FCSTD DOCUMENT  (FreeCAD 0.21R33771 (Git))
Label: key-v4_r
License: All rights reserved
LicenseURL: https://en.wikipedia.org/wiki/All_rights_reserved
objects: Sketcher::SketchObject×6, Part::Part2DObjectPython×3, Part::FeaturePython×2, Spreadsheet::Sheet×1
note: 10 computed .brp shape members not serialized (recipe doc carries the construction recipe); baked Part::Feature solids carry a one-line shape summary decoded from their .brp

FEATURE [Spreadsheet::Sheet] Spreadsheet  label="constants"
  cells = A1(slot_height)=0.6; B1='slot height; A2(base_normal)=1.5; B2='base normal; A3(base_thin)=0.3; B3='base thin ; A4(fillet_small)=0.15; B4='fillet rounding
FEATURE [Part::Part2DObjectPython] Wire  # Draft 2D object (typed FeaturePython)
  Area = 0
  ChamferSize = 0
  Closed = false
  End = (95,2.6,0)
  FilletRadius = 0
  Length = 95.9778
  MakeFace = true
  Points = (6) [(0,0,0),(19,0,0),(38,4.8,0),(57,7,0),(76,4.8,0),(95,2.6,0)]
  Start = (0,0,0)
  Subdivisions = 0
FEATURE [Part::Part2DObjectPython] Wire001  label="main matrix wire"  # Draft 2D object (typed FeaturePython)
  Area = 0
  ChamferSize = 0
  Closed = false
  End = (95,2.6,0)
  FilletRadius = 0
  Length = 323.978
  MakeFace = false
  Points = (18) [(0,0,0),(0,-19,0),(0,-38,0),(19,-38,0),(19,-19,0),(19,0,0),(38,4.8,0),(38,-14.2,0),(38,-33.2,0),(57,-31,0),(57,-12,0),(57,7,0),(76,4.8,0),+5 more]
  Start = (0,0,0)
  Subdivisions = 0
FEATURE [Part::Part2DObjectPython] Wire002  label="horizonal matrix"  # Draft 2D object (typed FeaturePython)
  Area = 0
  ChamferSize = 0
  Closed = false
  End = (95,2.6,0)
  FilletRadius = 0
  Length = 368.271
  MakeFace = true
  Points = (20) [(0,0,0),(0,-19,0),(0,-38,0),(19,-38,0),(19,-19,0),(19,0,0),(38,4.8,0),(38,-14.2,0),(38,-33.2,0),(47,-52.4,0),(66,-52.4,0),(57,-31,0),(57,-12,0),+7 more]
  Start = (0,0,0)
  Subdivisions = 0
FEATURE [Sketcher::SketchObject] Sketch001  label="smd cutout prototype"
  FullyConstrained = true
  sketch-geometry (67):
    g0: LineSegment StartX=-9.5 StartY=-9.5 StartZ=0 EndX=9.5 EndY=-9.5 EndZ=0
    g1: LineSegment StartX=9.5 StartY=-9.5 StartZ=0 EndX=9.5 EndY=9.5 EndZ=0
    g2: LineSegment StartX=9.5 StartY=9.5 StartZ=0 EndX=-9.5 EndY=9.5 EndZ=0
    g3: LineSegment StartX=-9.5 StartY=9.5 StartZ=0 EndX=-9.5 EndY=-9.5 EndZ=0
    g4: Circle CenterX=-3.81 CenterY=2.54 CenterZ=0 NormalX=0 NormalY=0 NormalZ=1 AngleXU=0 Radius=1.5
    g5: Circle CenterX=2.54 CenterY=5.08 CenterZ=0 NormalX=0 NormalY=0 NormalZ=1 AngleXU=0 Radius=1.5
    g6: Circle CenterX=0 CenterY=0 CenterZ=0 NormalX=0 NormalY=0 NormalZ=1 AngleXU=0 Radius=2
    g7: Circle CenterX=5 CenterY=0 CenterZ=0 NormalX=0 NormalY=0 NormalZ=1 AngleXU=0 Radius=1
    g8: Circle CenterX=-5 CenterY=0 CenterZ=0 NormalX=0 NormalY=0 NormalZ=1 AngleXU=0 Radius=1
    g9: GeomPoint X=-8.5 Y=1 Z=0
    g10: GeomPoint X=-8.5 Y=4 Z=0
    g11: GeomPoint X=-6 Y=4 Z=0
    g12: GeomPoint X=-2.5 Y=1 Z=0
    g13: GeomPoint X=-0.4 Y=2.9 Z=0
    g14: GeomPoint X=4.5 Y=2.9 Z=0
    g15: GeomPoint X=4.5 Y=3.6 Z=0
    g16: GeomPoint X=7.1 Y=6.7 Z=0
    g17: GeomPoint X=-4 Y=6.7 Z=0
    g18: LineSegment StartX=-8.5 StartY=1 StartZ=0 EndX=-2.5 EndY=1 EndZ=0
    g19: LineSegment StartX=-8.5 StartY=1 StartZ=0 EndX=-8.5 EndY=4 EndZ=0
    g20: LineSegment StartX=-8.5 StartY=4 StartZ=0 EndX=-6 EndY=4 EndZ=0
    g21: LineSegment StartX=-6 StartY=4 StartZ=0 EndX=-6 EndY=4.7 EndZ=0
    g22: LineSegment StartX=-4 StartY=6.7 StartZ=0 EndX=7.1 EndY=6.7 EndZ=0
    g23: LineSegment StartX=7.1 StartY=6.7 StartZ=0 EndX=7.1 EndY=3.6 EndZ=0
    g24: LineSegment StartX=7.1 StartY=3.6 StartZ=0 EndX=4.5 EndY=3.6 EndZ=0
    g25: LineSegment StartX=4.5 StartY=2.9 StartZ=0 EndX=4.5 EndY=3.6 EndZ=0
    g26: LineSegment StartX=4.5 StartY=2.9 StartZ=0 EndX=-0.4 EndY=2.9 EndZ=0
    g27: ArcOfCircle CenterX=-0.4 CenterY=0.789474 CenterZ=0 NormalX=0 NormalY=0 NormalZ=1 AngleXU=0 Radius=2.11053 StartAngle=1.5708 EndAngle=3.04168
    g28: LineSegment StartX=6.85 StartY=2.35 StartZ=0 EndX=6.85 EndY=-2.35 EndZ=0
    g29: LineSegment StartX=6.85 StartY=-2.35 StartZ=0 EndX=9.15 EndY=-2.35 EndZ=0
    g30: LineSegment StartX=9.15 StartY=-2.35 StartZ=0 EndX=9.15 EndY=2.35 EndZ=0
    g31: ArcOfCircle CenterX=-4 CenterY=4.7 CenterZ=0 NormalX=0 NormalY=0 NormalZ=1 AngleXU=0 Radius=2 StartAngle=1.5708 EndAngle=3.14159
    g32: LineSegment StartX=6.85 StartY=2.35 StartZ=0 EndX=9.15 EndY=2.35 EndZ=0
    g33: LineSegment StartX=-8.8 StartY=0.8 StartZ=0 EndX=-8.8 EndY=4.2 EndZ=0
    g34: LineSegment StartX=-8.3 StartY=4.7 StartZ=0 EndX=-7.1607 EndY=4.7 EndZ=0
    g35: LineSegment StartX=-4 StartY=7.4 StartZ=0 EndX=7.3 EndY=7.4 EndZ=0
    g36: LineSegment StartX=7.8 StartY=6.9 StartZ=0 EndX=7.8 EndY=3.55 EndZ=0
    g37: LineSegment StartX=9.5 StartY=2.55 StartZ=0 EndX=9.5 EndY=-2.55 EndZ=0
    g38: LineSegment StartX=9 StartY=-3.05 StartZ=0 EndX=6.65 EndY=-3.05 EndZ=0
    g39: LineSegment StartX=-8.3 StartY=0.3 StartZ=0 EndX=-7.19089 EndY=0.3 EndZ=0
    g40: ArcOfCircle CenterX=-5 CenterY=0 CenterZ=0 NormalX=0 NormalY=0 NormalZ=1 AngleXU=0 Radius=1.7 StartAngle=3.23263 EndAngle=4.71239
    g41: ArcOfCircle CenterX=0 CenterY=0 CenterZ=0 NormalX=0 NormalY=0 NormalZ=1 AngleXU=0 Radius=2.7 StartAngle=3.89963 EndAngle=5.52514
    g42: LineSegment StartX=-5 StartY=-1.7 StartZ=0 EndX=-2.32379 EndY=-1.7 EndZ=0
    g43: LineSegment StartX=6.15 StartY=-2.55 StartZ=0 EndX=6.15 EndY=-2.2 EndZ=0
    g44: LineSegment StartX=2.32379 StartY=-1.7 StartZ=0 EndX=5.65 EndY=-1.7 EndZ=0
    g45: ArcOfCircle CenterX=-4 CenterY=4.7 CenterZ=0 NormalX=0 NormalY=0 NormalZ=1 AngleXU=0 Radius=2.7 StartAngle=1.5708 EndAngle=2.9847
    g46: ArcOfCircle CenterX=-2.32379 CenterY=-2.2 CenterZ=0 NormalX=0 NormalY=0 NormalZ=1 AngleXU=0 Radius=0.5 StartAngle=0.758041 EndAngle=1.5708
    g47: ArcOfCircle CenterX=2.32379 CenterY=-2.2 CenterZ=0 NormalX=0 NormalY=0 NormalZ=1 AngleXU=0 Radius=0.5 StartAngle=1.5708 EndAngle=2.38355
    g48: ArcOfCircle CenterX=5.65 CenterY=-2.2 CenterZ=0 NormalX=0 NormalY=0 NormalZ=1 AngleXU=0 Radius=0.5 StartAngle=0 EndAngle=1.5708
    g49: GeomPoint X=6.15 Y=-1.7 Z=0
    g50: ArcOfCircle CenterX=6.65 CenterY=-2.55 CenterZ=0 NormalX=0 NormalY=0 NormalZ=1 AngleXU=0 Radius=0.5 StartAngle=3.14159 EndAngle=4.71239
    g51: GeomPoint X=6.15 Y=-3.05 Z=0
    g52: ArcOfCircle CenterX=9 CenterY=-2.55 CenterZ=0 NormalX=0 NormalY=0 NormalZ=1 AngleXU=0 Radius=0.5 StartAngle=4.71239 EndAngle=6.28319
    g53: GeomPoint X=9.5 Y=-3.05 Z=0
    g54: LineSegment StartX=8.3 StartY=3.05 StartZ=0 EndX=9 EndY=3.05 EndZ=0
    g55: ArcOfCircle CenterX=9 CenterY=2.55 CenterZ=0 NormalX=0 NormalY=0 NormalZ=1 AngleXU=0 Radius=0.5 StartAngle=3e-16 EndAngle=1.5708
    g56: GeomPoint X=9.5 Y=3.05 Z=0
    g57: ArcOfCircle CenterX=8.3 CenterY=3.55 CenterZ=0 NormalX=0 NormalY=0 NormalZ=1 AngleXU=0 Radius=0.5 StartAngle=3.14159 EndAngle=4.71239
    g58: GeomPoint X=7.8 Y=3.05 Z=0
    g59: ArcOfCircle CenterX=7.3 CenterY=6.9 CenterZ=0 NormalX=0 NormalY=0 NormalZ=1 AngleXU=0 Radius=0.5 StartAngle=-9e-16 EndAngle=1.5708
    g60: GeomPoint X=7.8 Y=7.4 Z=0
    g61: ArcOfCircle CenterX=-7.1607 CenterY=5.2 CenterZ=0 NormalX=0 NormalY=0 NormalZ=1 AngleXU=0 Radius=0.5 StartAngle=4.71239 EndAngle=6.12629
    g62: ArcOfCircle CenterX=-8.3 CenterY=4.2 CenterZ=0 NormalX=0 NormalY=0 NormalZ=1 AngleXU=0 Radius=0.5 StartAngle=1.5708 EndAngle=3.14159
    g63: GeomPoint X=-8.8 Y=4.7 Z=0
    g64: ArcOfCircle CenterX=-8.3 CenterY=0.8 CenterZ=0 NormalX=0 NormalY=0 NormalZ=1 AngleXU=0 Radius=0.5 StartAngle=3.14159 EndAngle=4.71239
    g65: GeomPoint X=-8.8 Y=0.3 Z=0
    g66: ArcOfCircle CenterX=-7.19089 CenterY=-0.2 CenterZ=0 NormalX=0 NormalY=0 NormalZ=1 AngleXU=0 Radius=0.5 StartAngle=0.0910348 EndAngle=1.5708
  constraints (157):
    c: Coincident(g2,g3)
    c: Horizontal(g0)
    c: Horizontal(g2)
    c: Vertical(g1)
    c: PointOnObject(g7,g-1)
    c: Equal(g4,g5)
    c: Symmetric(g7,g8,g-2)
    c: Equal(g8,g7)
    c: DistanceX(g-1,g5) = 2.54
    c: Distance(g5,g-1) = 5.08
    c: DistanceX(g2,g2) = 19
    c: Equal(g2,g3)
    c: Distance(g4,g-2) = 3.81
    c: Distance(g4,g-1) = 2.54
    c: Distance(g8,g-2) = 5
    c: Distance(g9,g-1) = 1
    c: Coincident(g18,g9)
    c: Coincident(g18,g12)
    c: Horizontal(g18)
    c: Distance(g9,g-2) = 8.5
    c: Coincident(g19,g9)
    c: Coincident(g19,g10)
    c: Vertical(g19)
    c: Distance(g10,g-1) = 4
    c: Coincident(g20,g10)
    c: Coincident(g20,g11)
    c: Horizontal(g20)
    c: Distance(g11,g-2) = 6
    c: Distance(g17,g-2) = 4
    c: DistanceY(g-1,g17) = 6.7
    c: Coincident(g21,g11)
    c: Vertical(g21)
    c: Coincident(g22,g17)
    c: Coincident(g22,g16)
    c: Horizontal(g22)
    c: DistanceX(g-1,g16) = 7.1
    c: Coincident(g23,g16)
    c: Vertical(g23)
    c: Distance(g23,g-1) = 3.6
    c: Coincident(g24,g23)
    c: Coincident(g24,g15)
    c: Coincident(g25,g14)
    c: Coincident(g25,g15)
    c: Coincident(g26,g14)
    c: Coincident(g26,g13)
    c: Horizontal(g24)
    c: Horizontal(g26)
    c: Vertical(g25)
    c: Distance(g-2,g25) = 4.5
    c: Distance(g14,g-1) = 2.9
    c: Distance(g13,g-2) = 0.4
    c: Distance(g12,g-2) = 2.5
    c: Coincident(g27,g13)
    c: Coincident(g27,g12)
    c: Diameter(g5) = 3
    c: Diameter(g8) = 2
    c: Diameter(g6) = 4
    c: Vertical(g30)
    c: Horizontal(g29)
    c: Distance(g28,g-2) = 6.85
    c: Distance(g28,g-1) = 2.35
    c: Symmetric(g28,g28,g-1)
    c: Vertical(g3)
    c: Coincident(g31,g17)
    c: Tangent(g31,g21) = 1.5708
    c: Coincident(g32,g28)
    c: Coincident(g32,g30)
    c: Horizontal(g32)
    c: Coincident(g6,g-1)
    c: Symmetric(g0,g1,g6)
    c: Coincident(g3,g0)
    c: Coincident(g2,g1)
    c: Coincident(g1,g0)
    c: DistanceX(g29,g29) = 2.3
    c: Coincident(g29,g30)
    c: Coincident(g29,g28)
    c: Tangent(g27,g26)
    c: Tangent(g31,g22)
    c: Vertical(g33)
    c: Horizontal(g34)
    c: Horizontal(g35)
    c: Vertical(g36)
    c: PointOnObject(g56,g1)
    c: PointOnObject(g53,g1)
    c: Horizontal(g38)
    c: Horizontal(g39)
    c: Distance(g20,g34) = 0.7
    c: Distance(g65,g19) = 0.3
    c: Distance(g18,g39) = 0.7
    c: Coincident(g40,g8)
    c: Coincident(g41,g6)
    c: Horizontal(g42)
    c: Vertical(g43)
    c: Tangent(g44,g42)
    c: Distance(g28,g43) = 0.7
    c: Distance(g53,g29) = 0.7
    c: Tangent(g42,g40) = -1.5708
    c: Distance(g23,g36) = 0.7
    c: Distance(g35,g22) = 0.7
    c: Coincident(g45,g31)
    c: Tangent(g45,g35) = 1.5708
    c: Tangent(g42,g46) = 1.5708
    c: Tangent(g41,g46) = 1.5708
    c: Tangent(g41,g47) = 1.5708
    c: Tangent(g44,g47) = 1.5708
    c: PointOnObject(g49,g44)
    c: PointOnObject(g49,g43)
    c: Tangent(g44,g48) = 1.5708
    c: Tangent(g43,g48) = -1.5708
    c: PointOnObject(g51,g43)
    c: PointOnObject(g51,g38)
    c: Tangent(g43,g50) = 1.5708
    c: Tangent(g38,g50) = 1.5708
    c: PointOnObject(g53,g38)
    c: PointOnObject(g53,g37)
    c: Tangent(g38,g52) = 1.5708
    c: Tangent(g37,g52) = 1.5708
    c: Horizontal(g54)
    c: Distance(g32,g54) = 0.7
    c: PointOnObject(g56,g37)
    c: PointOnObject(g56,g54)
    c: Tangent(g37,g55) = 1.5708
    c: Tangent(g54,g55) = 1.5708
    c: PointOnObject(g58,g54)
    c: PointOnObject(g58,g36)
    c: Tangent(g54,g57) = -1.5708
    c: Tangent(g36,g57) = -1.5708
    c: PointOnObject(g60,g35)
    c: PointOnObject(g60,g36)
    c: Tangent(g35,g59) = 1.5708
    c: Tangent(g36,g59) = 1.5708
    c: Tangent(g34,g61) = -1.5708
    c: Tangent(g45,g61) = 1.5708
    c: PointOnObject(g63,g34)
    c: PointOnObject(g63,g33)
    c: Tangent(g34,g62) = 1.5708
    c: Tangent(g33,g62) = 1.5708
    c: PointOnObject(g65,g39)
    c: PointOnObject(g65,g33)
    c: Tangent(g39,g64) = -1.5708
    c: Tangent(g33,g64) = 1.5708
    c: Tangent(g40,g66) = 1.5708
    c: Tangent(g39,g66) = 1.5708
    c: Radius(g46) = 0.5
    c: Equal(g66,g64)
    c: Equal(g64,g46)
    c: Equal(g46,g47)
    c: Equal(g47,g48)
    c: Equal(g48,g50)
    c: Equal(g50,g57)
    c: Equal(g57,g59)
    c: Equal(g59,g61)
    c: Equal(g61,g62)
    c: Equal(g57,g55)
    c: Equal(g52,g50)
    c: Distance(g40,g8) = 0.7
    c: Distance(g41,g6) = 0.7
FEATURE [Sketcher::SketchObject] Sketch003  label="smd cutout"
  FullyConstrained = false
  sketch-geometry (61):
    g0: GeomPoint X=-8.5 Y=1 Z=0
    g1: GeomPoint X=-8.5 Y=4 Z=0
    g2: GeomPoint X=-6 Y=4 Z=0
    g3: GeomPoint X=-2.5 Y=1 Z=0
    g4: GeomPoint X=-0.4 Y=2.9 Z=0
    g5: GeomPoint X=4.5 Y=2.9 Z=0
    g6: GeomPoint X=4.5 Y=3.6 Z=0
    g7: GeomPoint X=7.1 Y=6.7 Z=0
    g8: GeomPoint X=-4 Y=6.7 Z=0
    g9: LineSegment StartX=-8.8 StartY=0.8 StartZ=0 EndX=-8.8 EndY=4.2 EndZ=0
    g10: LineSegment StartX=-8.3 StartY=4.7 StartZ=0 EndX=-7.1607 EndY=4.7 EndZ=0
    g11: LineSegment StartX=-4 StartY=7.4 StartZ=0 EndX=7.3 EndY=7.4 EndZ=0
    g12: LineSegment StartX=7.8 StartY=6.9 StartZ=0 EndX=7.8 EndY=3.55 EndZ=0
    g13: LineSegment StartX=9.5 StartY=2.55 StartZ=0 EndX=9.5 EndY=-2.55 EndZ=0
    g14: LineSegment StartX=9 StartY=-3.05 StartZ=0 EndX=6.65 EndY=-3.05 EndZ=0
    g15: LineSegment StartX=-8.3 StartY=0.3 StartZ=0 EndX=-7.19089 EndY=0.3 EndZ=0
    g16: ArcOfCircle CenterX=-5 CenterY=0 CenterZ=0 NormalX=0 NormalY=0 NormalZ=1 AngleXU=0 Radius=1.7 StartAngle=3.23263 EndAngle=4.71239
    g17: ArcOfCircle CenterX=0 CenterY=0 CenterZ=0 NormalX=0 NormalY=0 NormalZ=1 AngleXU=0 Radius=2.7 StartAngle=3.89963 EndAngle=5.52514
    g18: LineSegment StartX=-5 StartY=-1.7 StartZ=0 EndX=-2.32379 EndY=-1.7 EndZ=0
    g19: LineSegment StartX=6.15 StartY=-2.55 StartZ=0 EndX=6.15 EndY=-2.2 EndZ=0
    g20: LineSegment StartX=2.32379 StartY=-1.7 StartZ=0 EndX=5.65 EndY=-1.7 EndZ=0
    g21: ArcOfCircle CenterX=-4 CenterY=4.7 CenterZ=0 NormalX=0 NormalY=0 NormalZ=1 AngleXU=0 Radius=2.7 StartAngle=1.5708 EndAngle=2.9847
    g22: ArcOfCircle CenterX=-2.32379 CenterY=-2.2 CenterZ=0 NormalX=0 NormalY=0 NormalZ=1 AngleXU=0 Radius=0.5 StartAngle=0.758041 EndAngle=1.5708
    g23: ArcOfCircle CenterX=2.32379 CenterY=-2.2 CenterZ=0 NormalX=0 NormalY=0 NormalZ=1 AngleXU=0 Radius=0.5 StartAngle=1.5708 EndAngle=2.38355
    g24: ArcOfCircle CenterX=5.65 CenterY=-2.2 CenterZ=0 NormalX=0 NormalY=0 NormalZ=1 AngleXU=0 Radius=0.5 StartAngle=0 EndAngle=1.5708
    g25: GeomPoint X=6.15 Y=-1.7 Z=0
    g26: ArcOfCircle CenterX=6.65 CenterY=-2.55 CenterZ=0 NormalX=0 NormalY=0 NormalZ=1 AngleXU=0 Radius=0.5 StartAngle=3.14159 EndAngle=4.71239
    g27: GeomPoint X=6.15 Y=-3.05 Z=0
    g28: ArcOfCircle CenterX=9 CenterY=-2.55 CenterZ=0 NormalX=0 NormalY=0 NormalZ=1 AngleXU=0 Radius=0.5 StartAngle=4.71239 EndAngle=6.28319
    g29: GeomPoint X=9.5 Y=-3.05 Z=0
    g30: LineSegment StartX=8.3 StartY=3.05 StartZ=0 EndX=9 EndY=3.05 EndZ=0
    g31: ArcOfCircle CenterX=9 CenterY=2.55 CenterZ=0 NormalX=0 NormalY=0 NormalZ=1 AngleXU=0 Radius=0.5 StartAngle=3e-16 EndAngle=1.5708
    g32: GeomPoint X=9.5 Y=3.05 Z=0
    g33: ArcOfCircle CenterX=8.3 CenterY=3.55 CenterZ=0 NormalX=0 NormalY=0 NormalZ=1 AngleXU=0 Radius=0.5 StartAngle=3.14159 EndAngle=4.71239
    g34: GeomPoint X=7.8 Y=3.05 Z=0
    g35: ArcOfCircle CenterX=7.3 CenterY=6.9 CenterZ=0 NormalX=0 NormalY=0 NormalZ=1 AngleXU=0 Radius=0.5 StartAngle=-9e-16 EndAngle=1.5708
    g36: GeomPoint X=7.8 Y=7.4 Z=0
    g37: ArcOfCircle CenterX=-7.1607 CenterY=5.2 CenterZ=0 NormalX=0 NormalY=0 NormalZ=1 AngleXU=0 Radius=0.5 StartAngle=4.71239 EndAngle=6.12629
    g38: ArcOfCircle CenterX=-8.3 CenterY=4.2 CenterZ=0 NormalX=0 NormalY=0 NormalZ=1 AngleXU=0 Radius=0.5 StartAngle=1.5708 EndAngle=3.14159
    g39: GeomPoint X=-8.8 Y=4.7 Z=0
    g40: ArcOfCircle CenterX=-8.3 CenterY=0.8 CenterZ=0 NormalX=0 NormalY=0 NormalZ=1 AngleXU=0 Radius=0.5 StartAngle=3.14159 EndAngle=4.71239
    g41: GeomPoint X=-8.8 Y=0.3 Z=0
    g42: ArcOfCircle CenterX=-7.19089 CenterY=-0.2 CenterZ=0 NormalX=0 NormalY=0 NormalZ=1 AngleXU=0 Radius=0.5 StartAngle=0.0910348 EndAngle=1.5708
    g43: ArcOfCircle CenterX=-5 CenterY=0 CenterZ=0 NormalX=0 NormalY=0 NormalZ=1 AngleXU=0 Radius=3.2 StartAngle=3.52599 EndAngle=4.71239
    g44: LineSegment StartX=-5 StartY=-3.2 StartZ=0 EndX=-2.72029 EndY=-3.2 EndZ=0
    g45: ArcOfCircle CenterX=0 CenterY=0 CenterZ=0 NormalX=0 NormalY=0 NormalZ=1 AngleXU=0 Radius=4.2 StartAngle=4.00784 EndAngle=5.41694
    g46: LineSegment StartX=2.72029 StartY=-3.2 StartZ=0 EndX=4.75857 EndY=-3.2 EndZ=0
    g47: ArcOfCircle CenterX=6.65 CenterY=-2.55 CenterZ=0 NormalX=0 NormalY=0 NormalZ=1 AngleXU=0 Radius=2 StartAngle=3.4726 EndAngle=4.71239
    g48: LineSegment StartX=9 StartY=-4.55 StartZ=0 EndX=6.65 EndY=-4.55 EndZ=0
    g49: ArcOfCircle CenterX=9 CenterY=-2.55 CenterZ=0 NormalX=0 NormalY=0 NormalZ=1 AngleXU=0 Radius=2 StartAngle=4.71239 EndAngle=6.28319
    g50: LineSegment StartX=11 StartY=2.55 StartZ=0 EndX=11 EndY=-2.55 EndZ=0
    g51: ArcOfCircle CenterX=9 CenterY=2.55 CenterZ=0 NormalX=0 NormalY=0 NormalZ=1 AngleXU=0 Radius=2 StartAngle=0 EndAngle=1.42023
    g52: LineSegment StartX=9.3 StartY=6.9 StartZ=0 EndX=9.3 EndY=4.52737 EndZ=0
    g53: ArcOfCircle CenterX=7.3 CenterY=6.9 CenterZ=0 NormalX=0 NormalY=0 NormalZ=1 AngleXU=0 Radius=2 StartAngle=4e-16 EndAngle=1.5708
    g54: LineSegment StartX=-4 StartY=8.9 StartZ=0 EndX=7.3 EndY=8.9 EndZ=0
    g55: ArcOfCircle CenterX=-4 CenterY=4.7 CenterZ=0 NormalX=0 NormalY=0 NormalZ=1 AngleXU=0 Radius=4.2 StartAngle=1.5708 EndAngle=2.77639
    g56: LineSegment StartX=-8.3 StartY=6.2 StartZ=0 EndX=-7.92301 EndY=6.2 EndZ=0
    g57: ArcOfCircle CenterX=-8.3 CenterY=4.2 CenterZ=0 NormalX=0 NormalY=0 NormalZ=1 AngleXU=0 Radius=2 StartAngle=1.5708 EndAngle=3.14159
    g58: LineSegment StartX=-10.3 StartY=0.8 StartZ=0 EndX=-10.3 EndY=4.2 EndZ=0
    g59: ArcOfCircle CenterX=-8.3 CenterY=0.8 CenterZ=0 NormalX=0 NormalY=0 NormalZ=1 AngleXU=0 Radius=2 StartAngle=3.14159 EndAngle=4.71239
    g60: LineSegment StartX=-8.3 StartY=-1.2 StartZ=0 EndX=-7.96648 EndY=-1.2 EndZ=0
  constraints (137):
    c: Distance(g0,g-1) = 1
    c: Distance(g0,g-2) = 8.5
    c: Distance(g1,g-1) = 4
    c: Distance(g2,g-2) = 6
    c: Distance(g8,g-2) = 4
    c: DistanceY(g-1,g8) = 6.7
    c: DistanceX(g-1,g7) = 7.1
    c: Distance(g5,g-1) = 2.9
    c: Distance(g4,g-2) = 0.4
    c: Distance(g3,g-2) = 2.5
    c: Vertical(g9)
    c: Horizontal(g10)
    c: Horizontal(g11)
    c: Vertical(g12)
    c: Horizontal(g14)
    c: Horizontal(g15)
    c: Distance(g1,g10) = 0.7
    c: Distance(g0,g15) = 0.7
    c: Horizontal(g18)
    c: Vertical(g19)
    c: Tangent(g20,g18)
    c: Tangent(g18,g16) = -1.5708
    c: Distance(g7,g12) = 0.7
    c: Tangent(g21,g11) = 1.5708
    c: Tangent(g18,g22) = 1.5708
    c: Tangent(g17,g22) = 1.5708
    c: Tangent(g17,g23) = 1.5708
    c: Tangent(g20,g23) = 1.5708
    c: PointOnObject(g25,g20)
    c: PointOnObject(g25,g19)
    c: Tangent(g20,g24) = 1.5708
    c: Tangent(g19,g24) = -1.5708
    c: PointOnObject(g27,g19)
    c: PointOnObject(g27,g14)
    c: Tangent(g19,g26) = 1.5708
    c: Tangent(g14,g26) = 1.5708
    c: PointOnObject(g29,g14)
    c: PointOnObject(g29,g13)
    c: Tangent(g14,g28) = 1.5708
    c: Tangent(g13,g28) = 1.5708
    c: Horizontal(g30)
    c: PointOnObject(g32,g13)
    c: PointOnObject(g32,g30)
    c: Tangent(g13,g31) = 1.5708
    c: Tangent(g30,g31) = 1.5708
    c: PointOnObject(g34,g30)
    c: PointOnObject(g34,g12)
    c: Tangent(g30,g33) = -1.5708
    c: Tangent(g12,g33) = -1.5708
    c: PointOnObject(g36,g11)
    c: PointOnObject(g36,g12)
    c: Tangent(g11,g35) = 1.5708
    c: Tangent(g12,g35) = 1.5708
    c: Tangent(g10,g37) = -1.5708
    c: Tangent(g21,g37) = 1.5708
    c: PointOnObject(g39,g10)
    c: PointOnObject(g39,g9)
    c: Tangent(g10,g38) = 1.5708
    c: Tangent(g9,g38) = 1.5708
    c: PointOnObject(g41,g15)
    c: PointOnObject(g41,g9)
    c: Tangent(g15,g40) = -1.5708
    c: Tangent(g9,g40) = 1.5708
    c: Tangent(g16,g42) = 1.5708
    c: Tangent(g15,g42) = 1.5708
    c: Radius(g22) = 0.5
    c: Equal(g42,g40)
    c: Equal(g40,g22)
    c: Equal(g22,g23)
    c: Equal(g23,g24)
    c: Equal(g24,g26)
    c: Equal(g26,g33)
    c: Equal(g33,g35)
    c: Equal(g35,g37)
    c: Equal(g37,g38)
    c: Equal(g33,g31)
    c: Equal(g28,g26)
    c: Tangent(g43,g44) = -1.5708
    c: Coincident(g43,g60)
    c: Coincident(g44,g45)
    c: Coincident(g45,g46)
    c: Coincident(g46,g47)
    c: Tangent(g47,g48) = 1.5708
    c: Tangent(g48,g49) = 1.5708
    c: Tangent(g49,g50) = 1.5708
    c: Tangent(g50,g51) = 1.5708
    c: Coincident(g51,g52)
    c: Tangent(g52,g53) = 1.5708
    c: Tangent(g53,g54) = 1.5708
    c: Tangent(g54,g55) = 1.5708
    c: Coincident(g55,g56)
    c: Tangent(g56,g57) = 1.5708
    c: Tangent(g57,g58) = 1.5708
    c: Tangent(g58,g59) = 1.5708
    c: Tangent(g59,g60) = -1.5708
    c: Block(g55)
    c: Block(g54)
    c: Block(g53)
    c: Block(g52)
    c: Block(g51)
    c: Block(g50)
    c: Block(g49)
    c: Block(g48)
    c: Block(g47)
    c: Block(g46)
    c: Block(g45)
    c: Block(g44)
    c: Block(g43)
    c: Block(g60)
    c: Block(g59)
    c: Block(g58)
    c: Block(g57)
    c: Block(g21)
    c: Block(g37)
    c: Block(g10)
    c: Block(g38)
    c: Block(g9)
    c: Block(g40)
    c: Block(g15)
    c: Block(g42)
    c: Block(g16)
    c: Block(g18)
    c: Block(g22)
    c: Block(g17)
    c: Block(g23)
    c: Block(g20)
    c: Block(g24)
    c: Block(g26)
    c: Block(g19)
    c: Block(g14)
    c: Block(g28)
    c: Block(g13)
    c: Block(g31)
    c: Block(g30)
    c: Block(g33)
    c: Block(g12)
    c: Block(g35)
FEATURE [Sketcher::SketchObject] Sketch004  label="smd cutout offset"
  FullyConstrained = false
  sketch-geometry (61):
    g0: GeomPoint X=-8.5 Y=1 Z=0
    g1: GeomPoint X=-8.5 Y=4 Z=0
    g2: GeomPoint X=-6 Y=4 Z=0
    g3: GeomPoint X=-2.5 Y=1 Z=0
    g4: GeomPoint X=-0.4 Y=2.9 Z=0
    g5: GeomPoint X=4.5 Y=2.9 Z=0
    g6: GeomPoint X=4.5 Y=3.6 Z=0
    g7: GeomPoint X=7.1 Y=6.7 Z=0
    g8: GeomPoint X=-4 Y=6.7 Z=0
    g9: LineSegment StartX=-8.8 StartY=0.8 StartZ=0 EndX=-8.8 EndY=4.2 EndZ=0
    g10: LineSegment StartX=-8.3 StartY=4.7 StartZ=0 EndX=-7.1607 EndY=4.7 EndZ=0
    g11: LineSegment StartX=-4 StartY=7.4 StartZ=0 EndX=7.3 EndY=7.4 EndZ=0
    g12: LineSegment StartX=7.8 StartY=6.9 StartZ=0 EndX=7.8 EndY=3.55 EndZ=0
    g13: LineSegment StartX=9.5 StartY=2.55 StartZ=0 EndX=9.5 EndY=-2.55 EndZ=0
    g14: LineSegment StartX=9 StartY=-3.05 StartZ=0 EndX=6.65 EndY=-3.05 EndZ=0
    g15: LineSegment StartX=-8.3 StartY=0.3 StartZ=0 EndX=-7.19089 EndY=0.3 EndZ=0
    g16: ArcOfCircle CenterX=-5 CenterY=0 CenterZ=0 NormalX=0 NormalY=0 NormalZ=1 AngleXU=0 Radius=1.7 StartAngle=3.23263 EndAngle=4.71239
    g17: ArcOfCircle CenterX=0 CenterY=0 CenterZ=0 NormalX=0 NormalY=0 NormalZ=1 AngleXU=0 Radius=2.7 StartAngle=3.89963 EndAngle=5.52514
    g18: LineSegment StartX=-5 StartY=-1.7 StartZ=0 EndX=-2.32379 EndY=-1.7 EndZ=0
    g19: LineSegment StartX=6.15 StartY=-2.55 StartZ=0 EndX=6.15 EndY=-2.2 EndZ=0
    g20: LineSegment StartX=2.32379 StartY=-1.7 StartZ=0 EndX=5.65 EndY=-1.7 EndZ=0
    g21: ArcOfCircle CenterX=-4 CenterY=4.7 CenterZ=0 NormalX=0 NormalY=0 NormalZ=1 AngleXU=0 Radius=2.7 StartAngle=1.5708 EndAngle=2.9847
    g22: ArcOfCircle CenterX=-2.32379 CenterY=-2.2 CenterZ=0 NormalX=0 NormalY=0 NormalZ=1 AngleXU=0 Radius=0.5 StartAngle=0.758041 EndAngle=1.5708
    g23: ArcOfCircle CenterX=2.32379 CenterY=-2.2 CenterZ=0 NormalX=0 NormalY=0 NormalZ=1 AngleXU=0 Radius=0.5 StartAngle=1.5708 EndAngle=2.38355
    g24: ArcOfCircle CenterX=5.65 CenterY=-2.2 CenterZ=0 NormalX=0 NormalY=0 NormalZ=1 AngleXU=0 Radius=0.5 StartAngle=0 EndAngle=1.5708
    g25: GeomPoint X=6.15 Y=-1.7 Z=0
    g26: ArcOfCircle CenterX=6.65 CenterY=-2.55 CenterZ=0 NormalX=0 NormalY=0 NormalZ=1 AngleXU=0 Radius=0.5 StartAngle=3.14159 EndAngle=4.71239
    g27: GeomPoint X=6.15 Y=-3.05 Z=0
    g28: ArcOfCircle CenterX=9 CenterY=-2.55 CenterZ=0 NormalX=0 NormalY=0 NormalZ=1 AngleXU=0 Radius=0.5 StartAngle=4.71239 EndAngle=6.28319
    g29: GeomPoint X=9.5 Y=-3.05 Z=0
    g30: LineSegment StartX=8.3 StartY=3.05 StartZ=0 EndX=9 EndY=3.05 EndZ=0
    g31: ArcOfCircle CenterX=9 CenterY=2.55 CenterZ=0 NormalX=0 NormalY=0 NormalZ=1 AngleXU=0 Radius=0.5 StartAngle=3e-16 EndAngle=1.5708
    g32: GeomPoint X=9.5 Y=3.05 Z=0
    g33: ArcOfCircle CenterX=8.3 CenterY=3.55 CenterZ=0 NormalX=0 NormalY=0 NormalZ=1 AngleXU=0 Radius=0.5 StartAngle=3.14159 EndAngle=4.71239
    g34: GeomPoint X=7.8 Y=3.05 Z=0
    g35: ArcOfCircle CenterX=7.3 CenterY=6.9 CenterZ=0 NormalX=0 NormalY=0 NormalZ=1 AngleXU=0 Radius=0.5 StartAngle=-9e-16 EndAngle=1.5708
    g36: GeomPoint X=7.8 Y=7.4 Z=0
    g37: ArcOfCircle CenterX=-7.1607 CenterY=5.2 CenterZ=0 NormalX=0 NormalY=0 NormalZ=1 AngleXU=0 Radius=0.5 StartAngle=4.71239 EndAngle=6.12629
    g38: ArcOfCircle CenterX=-8.3 CenterY=4.2 CenterZ=0 NormalX=0 NormalY=0 NormalZ=1 AngleXU=0 Radius=0.5 StartAngle=1.5708 EndAngle=3.14159
    g39: GeomPoint X=-8.8 Y=4.7 Z=0
    g40: ArcOfCircle CenterX=-8.3 CenterY=0.8 CenterZ=0 NormalX=0 NormalY=0 NormalZ=1 AngleXU=0 Radius=0.5 StartAngle=3.14159 EndAngle=4.71239
    g41: GeomPoint X=-8.8 Y=0.3 Z=0
    g42: ArcOfCircle CenterX=-7.19089 CenterY=-0.2 CenterZ=0 NormalX=0 NormalY=0 NormalZ=1 AngleXU=0 Radius=0.5 StartAngle=0.0910348 EndAngle=1.5708
    g43: ArcOfCircle CenterX=-5 CenterY=0 CenterZ=0 NormalX=0 NormalY=0 NormalZ=1 AngleXU=0 Radius=3.2 StartAngle=3.52599 EndAngle=4.71239
    g44: LineSegment StartX=-5 StartY=-3.2 StartZ=0 EndX=-2.72029 EndY=-3.2 EndZ=0
    g45: ArcOfCircle CenterX=0 CenterY=0 CenterZ=0 NormalX=0 NormalY=0 NormalZ=1 AngleXU=0 Radius=4.2 StartAngle=4.00784 EndAngle=5.41694
    g46: LineSegment StartX=2.72029 StartY=-3.2 StartZ=0 EndX=4.75857 EndY=-3.2 EndZ=0
    g47: ArcOfCircle CenterX=6.65 CenterY=-2.55 CenterZ=0 NormalX=0 NormalY=0 NormalZ=1 AngleXU=0 Radius=2 StartAngle=3.4726 EndAngle=4.71239
    g48: LineSegment StartX=9 StartY=-4.55 StartZ=0 EndX=6.65 EndY=-4.55 EndZ=0
    g49: ArcOfCircle CenterX=9 CenterY=-2.55 CenterZ=0 NormalX=0 NormalY=0 NormalZ=1 AngleXU=0 Radius=2 StartAngle=4.71239 EndAngle=6.28319
    g50: LineSegment StartX=11 StartY=2.55 StartZ=0 EndX=11 EndY=-2.55 EndZ=0
    g51: ArcOfCircle CenterX=9 CenterY=2.55 CenterZ=0 NormalX=0 NormalY=0 NormalZ=1 AngleXU=0 Radius=2 StartAngle=0 EndAngle=1.42023
    g52: LineSegment StartX=9.3 StartY=6.9 StartZ=0 EndX=9.3 EndY=4.52737 EndZ=0
    g53: ArcOfCircle CenterX=7.3 CenterY=6.9 CenterZ=0 NormalX=0 NormalY=0 NormalZ=1 AngleXU=0 Radius=2 StartAngle=4e-16 EndAngle=1.5708
    g54: LineSegment StartX=-4 StartY=8.9 StartZ=0 EndX=7.3 EndY=8.9 EndZ=0
    g55: ArcOfCircle CenterX=-4 CenterY=4.7 CenterZ=0 NormalX=0 NormalY=0 NormalZ=1 AngleXU=0 Radius=4.2 StartAngle=1.5708 EndAngle=2.77639
    g56: LineSegment StartX=-8.3 StartY=6.2 StartZ=0 EndX=-7.92301 EndY=6.2 EndZ=0
    g57: ArcOfCircle CenterX=-8.3 CenterY=4.2 CenterZ=0 NormalX=0 NormalY=0 NormalZ=1 AngleXU=0 Radius=2 StartAngle=1.5708 EndAngle=3.14159
    g58: LineSegment StartX=-10.3 StartY=0.8 StartZ=0 EndX=-10.3 EndY=4.2 EndZ=0
    g59: ArcOfCircle CenterX=-8.3 CenterY=0.8 CenterZ=0 NormalX=0 NormalY=0 NormalZ=1 AngleXU=0 Radius=2 StartAngle=3.14159 EndAngle=4.71239
    g60: LineSegment StartX=-8.3 StartY=-1.2 StartZ=0 EndX=-7.96648 EndY=-1.2 EndZ=0
  constraints (137):
    c: Distance(g0,g-1) = 1
    c: Distance(g0,g-2) = 8.5
    c: Distance(g1,g-1) = 4
    c: Distance(g2,g-2) = 6
    c: Distance(g8,g-2) = 4
    c: DistanceY(g-1,g8) = 6.7
    c: DistanceX(g-1,g7) = 7.1
    c: Distance(g5,g-1) = 2.9
    c: Distance(g4,g-2) = 0.4
    c: Distance(g3,g-2) = 2.5
    c: Vertical(g9)
    c: Horizontal(g10)
    c: Horizontal(g11)
    c: Vertical(g12)
    c: Horizontal(g14)
    c: Horizontal(g15)
    c: Distance(g1,g10) = 0.7
    c: Distance(g0,g15) = 0.7
    c: Horizontal(g18)
    c: Vertical(g19)
    c: Tangent(g20,g18)
    c: Tangent(g18,g16) = -1.5708
    c: Distance(g7,g12) = 0.7
    c: Tangent(g21,g11) = 1.5708
    c: Tangent(g18,g22) = 1.5708
    c: Tangent(g17,g22) = 1.5708
    c: Tangent(g17,g23) = 1.5708
    c: Tangent(g20,g23) = 1.5708
    c: PointOnObject(g25,g20)
    c: PointOnObject(g25,g19)
    c: Tangent(g20,g24) = 1.5708
    c: Tangent(g19,g24) = -1.5708
    c: PointOnObject(g27,g19)
    c: PointOnObject(g27,g14)
    c: Tangent(g19,g26) = 1.5708
    c: Tangent(g14,g26) = 1.5708
    c: PointOnObject(g29,g14)
    c: PointOnObject(g29,g13)
    c: Tangent(g14,g28) = 1.5708
    c: Tangent(g13,g28) = 1.5708
    c: Horizontal(g30)
    c: PointOnObject(g32,g13)
    c: PointOnObject(g32,g30)
    c: Tangent(g13,g31) = 1.5708
    c: Tangent(g30,g31) = 1.5708
    c: PointOnObject(g34,g30)
    c: PointOnObject(g34,g12)
    c: Tangent(g30,g33) = -1.5708
    c: Tangent(g12,g33) = -1.5708
    c: PointOnObject(g36,g11)
    c: PointOnObject(g36,g12)
    c: Tangent(g11,g35) = 1.5708
    c: Tangent(g12,g35) = 1.5708
    c: Tangent(g10,g37) = -1.5708
    c: Tangent(g21,g37) = 1.5708
    c: PointOnObject(g39,g10)
    c: PointOnObject(g39,g9)
    c: Tangent(g10,g38) = 1.5708
    c: Tangent(g9,g38) = 1.5708
    c: PointOnObject(g41,g15)
    c: PointOnObject(g41,g9)
    c: Tangent(g15,g40) = -1.5708
    c: Tangent(g9,g40) = 1.5708
    c: Tangent(g16,g42) = 1.5708
    c: Tangent(g15,g42) = 1.5708
    c: Radius(g22) = 0.5
    c: Equal(g42,g40)
    c: Equal(g40,g22)
    c: Equal(g22,g23)
    c: Equal(g23,g24)
    c: Equal(g24,g26)
    c: Equal(g26,g33)
    c: Equal(g33,g35)
    c: Equal(g35,g37)
    c: Equal(g37,g38)
    c: Equal(g33,g31)
    c: Equal(g28,g26)
    c: Tangent(g43,g44) = -1.5708
    c: Coincident(g43,g60)
    c: Coincident(g44,g45)
    c: Coincident(g45,g46)
    c: Coincident(g46,g47)
    c: Tangent(g47,g48) = 1.5708
    c: Tangent(g48,g49) = 1.5708
    c: Tangent(g49,g50) = 1.5708
    c: Tangent(g50,g51) = 1.5708
    c: Coincident(g51,g52)
    c: Tangent(g52,g53) = 1.5708
    c: Tangent(g53,g54) = 1.5708
    c: Tangent(g54,g55) = 1.5708
    c: Coincident(g55,g56)
    c: Tangent(g56,g57) = 1.5708
    c: Tangent(g57,g58) = 1.5708
    c: Tangent(g58,g59) = 1.5708
    c: Tangent(g59,g60) = -1.5708
    c: Block(g55)
    c: Block(g54)
    c: Block(g53)
    c: Block(g52)
    c: Block(g51)
    c: Block(g50)
    c: Block(g49)
    c: Block(g48)
    c: Block(g47)
    c: Block(g46)
    c: Block(g45)
    c: Block(g44)
    c: Block(g43)
    c: Block(g60)
    c: Block(g59)
    c: Block(g58)
    c: Block(g57)
    c: Block(g21)
    c: Block(g37)
    c: Block(g10)
    c: Block(g38)
    c: Block(g9)
    c: Block(g40)
    c: Block(g15)
    c: Block(g42)
    c: Block(g16)
    c: Block(g18)
    c: Block(g22)
    c: Block(g17)
    c: Block(g23)
    c: Block(g20)
    c: Block(g24)
    c: Block(g26)
    c: Block(g19)
    c: Block(g14)
    c: Block(g28)
    c: Block(g13)
    c: Block(g31)
    c: Block(g30)
    c: Block(g33)
    c: Block(g12)
    c: Block(g35)
FEATURE [Part::FeaturePython] PointArray  # Draft array (typed FeaturePython)
  Base = -> Sketch004
  Count = 20
  PointObject = -> Wire002
FEATURE [Sketcher::SketchObject] Sketch  label="smd cutout offset horizontal"
  FullyConstrained = false
  sketch-geometry (312):
    g0: ArcOfCircle CenterX=-5 CenterY=0 CenterZ=0 NormalX=0 NormalY=0 NormalZ=1 AngleXU=0 Radius=3.2 StartAngle=3.52599 EndAngle=4.71239
    g1: LineSegment StartX=-5 StartY=-3.2 StartZ=0 EndX=-2.72029 EndY=-3.2 EndZ=0
    g2: ArcOfCircle CenterX=0 CenterY=0 CenterZ=0 NormalX=0 NormalY=0 NormalZ=1 AngleXU=0 Radius=4.2 StartAngle=4.00784 EndAngle=5.41694
    g3: LineSegment StartX=2.72029 StartY=-3.2 StartZ=0 EndX=4.75857 EndY=-3.2 EndZ=0
    g4: ArcOfCircle CenterX=6.65 CenterY=-2.55 CenterZ=0 NormalX=0 NormalY=0 NormalZ=1 AngleXU=0 Radius=2 StartAngle=3.4726 EndAngle=4.71239
    g5: LineSegment StartX=9 StartY=-4.55 StartZ=0 EndX=6.65 EndY=-4.55 EndZ=0
    g6: ArcOfCircle CenterX=9 CenterY=-2.55 CenterZ=0 NormalX=0 NormalY=0 NormalZ=1 AngleXU=0 Radius=2 StartAngle=4.71239 EndAngle=6.28319
    g7: LineSegment StartX=11 StartY=-1.2 StartZ=0 EndX=11 EndY=-2.55 EndZ=0
    g8: LineSegment StartX=9.3 StartY=6.9 StartZ=0 EndX=9.3 EndY=5.62829 EndZ=0
    g9: ArcOfCircle CenterX=7.3 CenterY=6.9 CenterZ=0 NormalX=0 NormalY=0 NormalZ=1 AngleXU=0 Radius=2 StartAngle=4e-16 EndAngle=1.5708
    g10: LineSegment StartX=-4 StartY=8.9 StartZ=0 EndX=7.3 EndY=8.9 EndZ=0
    g11: ArcOfCircle CenterX=-4 CenterY=4.7 CenterZ=0 NormalX=0 NormalY=0 NormalZ=1 AngleXU=0 Radius=4.2 StartAngle=1.5708 EndAngle=2.77639
    g12: LineSegment StartX=-8.3 StartY=6.2 StartZ=0 EndX=-7.92301 EndY=6.2 EndZ=0
    g13: ArcOfCircle CenterX=-8.3 CenterY=4.2 CenterZ=0 NormalX=0 NormalY=0 NormalZ=1 AngleXU=0 Radius=2 StartAngle=1.5708 EndAngle=3.14159
    g14: LineSegment StartX=-10.3 StartY=0.8 StartZ=0 EndX=-10.3 EndY=4.2 EndZ=0
    g15: ArcOfCircle CenterX=-8.3 CenterY=0.8 CenterZ=0 NormalX=0 NormalY=0 NormalZ=1 AngleXU=0 Radius=2 StartAngle=3.14159 EndAngle=4.71239
    g16: LineSegment StartX=-8.3 StartY=-1.2 StartZ=0 EndX=-7.96648 EndY=-1.2 EndZ=0
    g17: ArcOfCircle CenterX=-5 CenterY=-19 CenterZ=0 NormalX=0 NormalY=0 NormalZ=1 AngleXU=0 Radius=3.2 StartAngle=3.52599 EndAngle=4.71239
    g18: LineSegment StartX=-5 StartY=-22.2 StartZ=0 EndX=-2.72029 EndY=-22.2 EndZ=0
    g19: ArcOfCircle CenterX=0 CenterY=-19 CenterZ=0 NormalX=0 NormalY=0 NormalZ=1 AngleXU=0 Radius=4.2 StartAngle=4.00784 EndAngle=5.41694
    g20: LineSegment StartX=2.72029 StartY=-22.2 StartZ=0 EndX=4.75857 EndY=-22.2 EndZ=0
    g21: ArcOfCircle CenterX=6.65 CenterY=-21.55 CenterZ=0 NormalX=0 NormalY=0 NormalZ=1 AngleXU=0 Radius=2 StartAngle=3.4726 EndAngle=4.71239
    g22: LineSegment StartX=9 StartY=-23.55 StartZ=0 EndX=6.65 EndY=-23.55 EndZ=0
    g23: ArcOfCircle CenterX=9 CenterY=-21.55 CenterZ=0 NormalX=0 NormalY=0 NormalZ=1 AngleXU=0 Radius=2 StartAngle=4.71239 EndAngle=6.28319
    g24: LineSegment StartX=11 StartY=-20.2 StartZ=0 EndX=11 EndY=-21.55 EndZ=0
    g25: LineSegment StartX=9.3 StartY=-12.1 StartZ=0 EndX=9.3 EndY=-13.3717 EndZ=0
    g26: ArcOfCircle CenterX=7.3 CenterY=-12.1 CenterZ=0 NormalX=0 NormalY=0 NormalZ=1 AngleXU=0 Radius=2 StartAngle=4e-16 EndAngle=1.5708
    g27: LineSegment StartX=-4 StartY=-10.1 StartZ=0 EndX=7.3 EndY=-10.1 EndZ=0
    g28: ArcOfCircle CenterX=-4 CenterY=-14.3 CenterZ=0 NormalX=0 NormalY=0 NormalZ=1 AngleXU=0 Radius=4.2 StartAngle=1.5708 EndAngle=2.77639
    g29: LineSegment StartX=-8.3 StartY=-12.8 StartZ=0 EndX=-7.92301 EndY=-12.8 EndZ=0
    g30: ArcOfCircle CenterX=-8.3 CenterY=-14.8 CenterZ=0 NormalX=0 NormalY=0 NormalZ=1 AngleXU=0 Radius=2 StartAngle=1.5708 EndAngle=3.14159
    g31: LineSegment StartX=-10.3 StartY=-18.2 StartZ=0 EndX=-10.3 EndY=-14.8 EndZ=0
    g32: ArcOfCircle CenterX=-8.3 CenterY=-18.2 CenterZ=0 NormalX=0 NormalY=0 NormalZ=1 AngleXU=0 Radius=2 StartAngle=3.14159 EndAngle=4.71239
    g33: LineSegment StartX=-8.3 StartY=-20.2 StartZ=0 EndX=-7.96648 EndY=-20.2 EndZ=0
    g34: ArcOfCircle CenterX=-5 CenterY=-38 CenterZ=0 NormalX=0 NormalY=0 NormalZ=1 AngleXU=0 Radius=3.2 StartAngle=3.52599 EndAngle=4.71239
    g35: LineSegment StartX=-5 StartY=-41.2 StartZ=0 EndX=-2.72029 EndY=-41.2 EndZ=0
    g36: ArcOfCircle CenterX=0 CenterY=-38 CenterZ=0 NormalX=0 NormalY=0 NormalZ=1 AngleXU=0 Radius=4.2 StartAngle=4.00784 EndAngle=5.41694
    g37: LineSegment StartX=2.72029 StartY=-41.2 StartZ=0 EndX=4.75857 EndY=-41.2 EndZ=0
    g38: ArcOfCircle CenterX=6.65 CenterY=-40.55 CenterZ=0 NormalX=0 NormalY=0 NormalZ=1 AngleXU=0 Radius=2 StartAngle=3.4726 EndAngle=4.71239
    g39: LineSegment StartX=9 StartY=-42.55 StartZ=0 EndX=6.65 EndY=-42.55 EndZ=0
    g40: ArcOfCircle CenterX=9 CenterY=-40.55 CenterZ=0 NormalX=0 NormalY=0 NormalZ=1 AngleXU=0 Radius=2 StartAngle=4.71239 EndAngle=6.28319
    g41: LineSegment StartX=11 StartY=-39.2 StartZ=0 EndX=11 EndY=-40.55 EndZ=0
    g42: LineSegment StartX=9.3 StartY=-31.1 StartZ=0 EndX=9.3 EndY=-32.3717 EndZ=0
    g43: ArcOfCircle CenterX=7.3 CenterY=-31.1 CenterZ=0 NormalX=0 NormalY=0 NormalZ=1 AngleXU=0 Radius=2 StartAngle=4e-16 EndAngle=1.5708
    g44: LineSegment StartX=-4 StartY=-29.1 StartZ=0 EndX=7.3 EndY=-29.1 EndZ=0
    g45: ArcOfCircle CenterX=-4 CenterY=-33.3 CenterZ=0 NormalX=0 NormalY=0 NormalZ=1 AngleXU=0 Radius=4.2 StartAngle=1.5708 EndAngle=2.77639
    g46: LineSegment StartX=-8.3 StartY=-31.8 StartZ=0 EndX=-7.92301 EndY=-31.8 EndZ=0
    g47: ArcOfCircle CenterX=-8.3 CenterY=-33.8 CenterZ=0 NormalX=0 NormalY=0 NormalZ=1 AngleXU=0 Radius=2 StartAngle=1.5708 EndAngle=3.14159
    g48: LineSegment StartX=-10.3 StartY=-37.2 StartZ=0 EndX=-10.3 EndY=-33.8 EndZ=0
    g49: ArcOfCircle CenterX=-8.3 CenterY=-37.2 CenterZ=0 NormalX=0 NormalY=0 NormalZ=1 AngleXU=0 Radius=2 StartAngle=3.14159 EndAngle=4.71239
    g50: LineSegment StartX=-8.3 StartY=-39.2 StartZ=0 EndX=-7.96648 EndY=-39.2 EndZ=0
    g51: ArcOfCircle CenterX=14 CenterY=-38 CenterZ=0 NormalX=0 NormalY=0 NormalZ=1 AngleXU=0 Radius=3.2 StartAngle=3.52599 EndAngle=4.71239
    g52: LineSegment StartX=14 StartY=-41.2 StartZ=0 EndX=16.2797 EndY=-41.2 EndZ=0
    g53: ArcOfCircle CenterX=19 CenterY=-38 CenterZ=0 NormalX=0 NormalY=0 NormalZ=1 AngleXU=0 Radius=4.2 StartAngle=4.00784 EndAngle=5.41694
    g54: LineSegment StartX=21.7203 StartY=-41.2 StartZ=0 EndX=23.7586 EndY=-41.2 EndZ=0
    g55: ArcOfCircle CenterX=25.65 CenterY=-40.55 CenterZ=0 NormalX=0 NormalY=0 NormalZ=1 AngleXU=0 Radius=2 StartAngle=3.4726 EndAngle=4.71239
    g56: LineSegment StartX=28 StartY=-42.55 StartZ=0 EndX=25.65 EndY=-42.55 EndZ=0
    g57: ArcOfCircle CenterX=28 CenterY=-40.55 CenterZ=0 NormalX=0 NormalY=0 NormalZ=1 AngleXU=0 Radius=2 StartAngle=4.71239 EndAngle=6.28319
    g58: LineSegment StartX=30 StartY=-35.45 StartZ=0 EndX=30 EndY=-40.55 EndZ=0
    g59: ArcOfCircle CenterX=28 CenterY=-35.45 CenterZ=0 NormalX=0 NormalY=0 NormalZ=1 AngleXU=0 Radius=2 StartAngle=0 EndAngle=0.552715
    g60: ArcOfCircle CenterX=26.3 CenterY=-31.1 CenterZ=0 NormalX=0 NormalY=0 NormalZ=1 AngleXU=0 Radius=2 StartAngle=0.795399 EndAngle=1.5708
    g61: LineSegment StartX=15 StartY=-29.1 StartZ=0 EndX=26.3 EndY=-29.1 EndZ=0
    g62: ArcOfCircle CenterX=15 CenterY=-33.3 CenterZ=0 NormalX=0 NormalY=0 NormalZ=1 AngleXU=0 Radius=4.2 StartAngle=1.5708 EndAngle=2.77639
    g63: LineSegment StartX=10.7 StartY=-31.8 StartZ=0 EndX=11.077 EndY=-31.8 EndZ=0
    g64: ArcOfCircle CenterX=10.7 CenterY=-33.8 CenterZ=0 NormalX=0 NormalY=0 NormalZ=1 AngleXU=0 Radius=2 StartAngle=1.5708 EndAngle=2.34619
    g65: LineSegment StartX=11 StartY=-39.2 StartZ=0 EndX=11.0335 EndY=-39.2 EndZ=0
    g66: ArcOfCircle CenterX=14 CenterY=-19 CenterZ=0 NormalX=0 NormalY=0 NormalZ=1 AngleXU=0 Radius=3.2 StartAngle=3.52599 EndAngle=4.71239
    g67: LineSegment StartX=14 StartY=-22.2 StartZ=0 EndX=16.2797 EndY=-22.2 EndZ=0
    g68: ArcOfCircle CenterX=19 CenterY=-19 CenterZ=0 NormalX=0 NormalY=0 NormalZ=1 AngleXU=0 Radius=4.2 StartAngle=4.00784 EndAngle=5.41694
    g69: LineSegment StartX=21.7203 StartY=-22.2 StartZ=0 EndX=23.7586 EndY=-22.2 EndZ=0
    g70: ArcOfCircle CenterX=25.65 CenterY=-21.55 CenterZ=0 NormalX=0 NormalY=0 NormalZ=1 AngleXU=0 Radius=2 StartAngle=3.4726 EndAngle=4.71239
    g71: LineSegment StartX=28 StartY=-23.55 StartZ=0 EndX=25.65 EndY=-23.55 EndZ=0
    g72: ArcOfCircle CenterX=28 CenterY=-21.55 CenterZ=0 NormalX=0 NormalY=0 NormalZ=1 AngleXU=0 Radius=2 StartAngle=4.71239 EndAngle=6.28319
    g73: LineSegment StartX=30 StartY=-16.45 StartZ=0 EndX=30 EndY=-21.55 EndZ=0
    g74: ArcOfCircle CenterX=28 CenterY=-16.45 CenterZ=0 NormalX=0 NormalY=0 NormalZ=1 AngleXU=0 Radius=2 StartAngle=0 EndAngle=0.552715
    g75: ArcOfCircle CenterX=26.3 CenterY=-12.1 CenterZ=0 NormalX=0 NormalY=0 NormalZ=1 AngleXU=0 Radius=2 StartAngle=0.795399 EndAngle=1.5708
    g76: LineSegment StartX=15 StartY=-10.1 StartZ=0 EndX=26.3 EndY=-10.1 EndZ=0
    g77: ArcOfCircle CenterX=15 CenterY=-14.3 CenterZ=0 NormalX=0 NormalY=0 NormalZ=1 AngleXU=0 Radius=4.2 StartAngle=1.5708 EndAngle=2.77639
    g78: LineSegment StartX=10.7 StartY=-12.8 StartZ=0 EndX=11.077 EndY=-12.8 EndZ=0
    g79: ArcOfCircle CenterX=10.7 CenterY=-14.8 CenterZ=0 NormalX=0 NormalY=0 NormalZ=1 AngleXU=0 Radius=2 StartAngle=1.5708 EndAngle=2.34619
    g80: LineSegment StartX=11 StartY=-20.2 StartZ=0 EndX=11.0335 EndY=-20.2 EndZ=0
    g81: ArcOfCircle CenterX=14 CenterY=0 CenterZ=0 NormalX=0 NormalY=0 NormalZ=1 AngleXU=0 Radius=3.2 StartAngle=3.52599 EndAngle=4.71239
    g82: LineSegment StartX=14 StartY=-3.2 StartZ=0 EndX=16.2797 EndY=-3.2 EndZ=0
    g83: ArcOfCircle CenterX=19 CenterY=0 CenterZ=0 NormalX=0 NormalY=0 NormalZ=1 AngleXU=0 Radius=4.2 StartAngle=4.00784 EndAngle=5.41694
    g84: LineSegment StartX=21.7203 StartY=-3.2 StartZ=0 EndX=23.7586 EndY=-3.2 EndZ=0
    g85: ArcOfCircle CenterX=25.65 CenterY=-2.55 CenterZ=0 NormalX=0 NormalY=0 NormalZ=1 AngleXU=0 Radius=2 StartAngle=3.4726 EndAngle=4.71239
    g86: LineSegment StartX=28 StartY=-4.55 StartZ=0 EndX=25.65 EndY=-4.55 EndZ=0
    g87: ArcOfCircle CenterX=28 CenterY=-2.55 CenterZ=0 NormalX=0 NormalY=0 NormalZ=1 AngleXU=0 Radius=2 StartAngle=4.71239 EndAngle=6.28319
    g88: LineSegment StartX=30 StartY=2.55 StartZ=0 EndX=30 EndY=-2.55 EndZ=0
    g89: ArcOfCircle CenterX=28 CenterY=2.55 CenterZ=0 NormalX=0 NormalY=0 NormalZ=1 AngleXU=0 Radius=2 StartAngle=0 EndAngle=0.552715
    g90: ArcOfCircle CenterX=26.3 CenterY=6.9 CenterZ=0 NormalX=0 NormalY=0 NormalZ=1 AngleXU=0 Radius=2 StartAngle=0.795399 EndAngle=1.5708
    g91: LineSegment StartX=15 StartY=8.9 StartZ=0 EndX=26.3 EndY=8.9 EndZ=0
    g92: ArcOfCircle CenterX=15 CenterY=4.7 CenterZ=0 NormalX=0 NormalY=0 NormalZ=1 AngleXU=0 Radius=4.2 StartAngle=1.5708 EndAngle=2.77639
    g93: LineSegment StartX=10.7 StartY=6.2 StartZ=0 EndX=11.077 EndY=6.2 EndZ=0
    g94: ArcOfCircle CenterX=10.7 CenterY=4.2 CenterZ=0 NormalX=0 NormalY=0 NormalZ=1 AngleXU=0 Radius=2 StartAngle=1.5708 EndAngle=2.34619
    g95: LineSegment StartX=11 StartY=-1.2 StartZ=0 EndX=11.0335 EndY=-1.2 EndZ=0
    g96: ArcOfCircle CenterX=33 CenterY=4.8 CenterZ=0 NormalX=0 NormalY=0 NormalZ=1 AngleXU=0 Radius=3.2 StartAngle=3.52599 EndAngle=4.71239
    g97: LineSegment StartX=33 StartY=1.6 StartZ=0 EndX=35.2797 EndY=1.6 EndZ=0
    g98: ArcOfCircle CenterX=38 CenterY=4.8 CenterZ=0 NormalX=0 NormalY=0 NormalZ=1 AngleXU=0 Radius=4.2 StartAngle=4.00784 EndAngle=5.41694
    g99: LineSegment StartX=40.7203 StartY=1.6 StartZ=0 EndX=42.7586 EndY=1.6 EndZ=0
    g100: ArcOfCircle CenterX=44.65 CenterY=2.25 CenterZ=0 NormalX=0 NormalY=0 NormalZ=1 AngleXU=0 Radius=2 StartAngle=3.4726 EndAngle=4.71239
    g101: LineSegment StartX=47 StartY=0.25 StartZ=0 EndX=44.65 EndY=0.25 EndZ=0
    g102: ArcOfCircle CenterX=47 CenterY=2.25 CenterZ=0 NormalX=0 NormalY=0 NormalZ=1 AngleXU=0 Radius=2 StartAngle=4.71239 EndAngle=6.28319
    g103: LineSegment StartX=49 StartY=5.8 StartZ=0 EndX=49 EndY=2.25 EndZ=0
    g104: ArcOfCircle CenterX=45.3 CenterY=11.7 CenterZ=0 NormalX=0 NormalY=0 NormalZ=1 AngleXU=0 Radius=2 StartAngle=0.391193 EndAngle=1.5708
    g105: LineSegment StartX=34 StartY=13.7 StartZ=0 EndX=45.3 EndY=13.7 EndZ=0
    g106: ArcOfCircle CenterX=34 CenterY=9.5 CenterZ=0 NormalX=0 NormalY=0 NormalZ=1 AngleXU=0 Radius=4.2 StartAngle=1.5708 EndAngle=2.77639
    g107: LineSegment StartX=29.7 StartY=11 StartZ=0 EndX=30.077 EndY=11 EndZ=0
    g108: ArcOfCircle CenterX=29.7 CenterY=9 CenterZ=0 NormalX=0 NormalY=0 NormalZ=1 AngleXU=0 Radius=2 StartAngle=1.5708 EndAngle=3.14159
    g109: LineSegment StartX=27.7 StartY=8.32829 StartZ=0 EndX=27.7 EndY=9 EndZ=0
    g110: LineSegment StartX=29.7 StartY=3.6 StartZ=0 EndX=30.0335 EndY=3.6 EndZ=0
    g111: ArcOfCircle CenterX=33 CenterY=-14.2 CenterZ=0 NormalX=0 NormalY=0 NormalZ=1 AngleXU=0 Radius=3.2 StartAngle=3.52599 EndAngle=4.71239
    g112: LineSegment StartX=33 StartY=-17.4 StartZ=0 EndX=35.2797 EndY=-17.4 EndZ=0
    g113: ArcOfCircle CenterX=38 CenterY=-14.2 CenterZ=0 NormalX=0 NormalY=0 NormalZ=1 AngleXU=0 Radius=4.2 StartAngle=4.00784 EndAngle=5.41694
    g114: LineSegment StartX=40.7203 StartY=-17.4 StartZ=0 EndX=42.7586 EndY=-17.4 EndZ=0
    g115: ArcOfCircle CenterX=44.65 CenterY=-16.75 CenterZ=0 NormalX=0 NormalY=0 NormalZ=1 AngleXU=0 Radius=2 StartAngle=3.4726 EndAngle=4.71239
    g116: LineSegment StartX=47 StartY=-18.75 StartZ=0 EndX=44.65 EndY=-18.75 EndZ=0
    g117: ArcOfCircle CenterX=47 CenterY=-16.75 CenterZ=0 NormalX=0 NormalY=0 NormalZ=1 AngleXU=0 Radius=2 StartAngle=4.71239 EndAngle=6.28319
    g118: LineSegment StartX=49 StartY=-13.2 StartZ=0 EndX=49 EndY=-16.75 EndZ=0
    g119: ArcOfCircle CenterX=45.3 CenterY=-7.3 CenterZ=0 NormalX=0 NormalY=0 NormalZ=1 AngleXU=0 Radius=2 StartAngle=0.391193 EndAngle=1.5708
    g120: LineSegment StartX=34 StartY=-5.3 StartZ=0 EndX=45.3 EndY=-5.3 EndZ=0
    g121: ArcOfCircle CenterX=34 CenterY=-9.5 CenterZ=0 NormalX=0 NormalY=0 NormalZ=1 AngleXU=0 Radius=4.2 StartAngle=1.5708 EndAngle=2.77639
    g122: LineSegment StartX=29.7 StartY=-8 StartZ=0 EndX=30.077 EndY=-8 EndZ=0
    g123: ArcOfCircle CenterX=29.7 CenterY=-10 CenterZ=0 NormalX=0 NormalY=0 NormalZ=1 AngleXU=0 Radius=2 StartAngle=1.5708 EndAngle=3.14159
    g124: LineSegment StartX=27.7 StartY=-10.6717 StartZ=0 EndX=27.7 EndY=-10 EndZ=0
    g125: LineSegment StartX=29.7 StartY=-15.4 StartZ=0 EndX=30.0335 EndY=-15.4 EndZ=0
    g126: ArcOfCircle CenterX=33 CenterY=-33.2 CenterZ=0 NormalX=0 NormalY=0 NormalZ=1 AngleXU=0 Radius=3.2 StartAngle=3.52599 EndAngle=4.71239
    g127: LineSegment StartX=33 StartY=-36.4 StartZ=0 EndX=35.2797 EndY=-36.4 EndZ=0
    g128: ArcOfCircle CenterX=38 CenterY=-33.2 CenterZ=0 NormalX=0 NormalY=0 NormalZ=1 AngleXU=0 Radius=4.2 StartAngle=4.00784 EndAngle=5.41694
    g129: LineSegment StartX=40.7203 StartY=-36.4 StartZ=0 EndX=42.7586 EndY=-36.4 EndZ=0
    g130: ArcOfCircle CenterX=44.65 CenterY=-35.75 CenterZ=0 NormalX=0 NormalY=0 NormalZ=1 AngleXU=0 Radius=2 StartAngle=3.4726 EndAngle=4.71239
    g131: LineSegment StartX=47 StartY=-37.75 StartZ=0 EndX=44.65 EndY=-37.75 EndZ=0
    g132: ArcOfCircle CenterX=47 CenterY=-35.75 CenterZ=0 NormalX=0 NormalY=0 NormalZ=1 AngleXU=0 Radius=2 StartAngle=4.71239 EndAngle=6.28319
    g133: LineSegment StartX=49 StartY=-32.2 StartZ=0 EndX=49 EndY=-35.75 EndZ=0
    g134: ArcOfCircle CenterX=45.3 CenterY=-26.3 CenterZ=0 NormalX=0 NormalY=0 NormalZ=1 AngleXU=0 Radius=2 StartAngle=0.391193 EndAngle=1.5708
    g135: LineSegment StartX=34 StartY=-24.3 StartZ=0 EndX=45.3 EndY=-24.3 EndZ=0
    g136: ArcOfCircle CenterX=34 CenterY=-28.5 CenterZ=0 NormalX=0 NormalY=0 NormalZ=1 AngleXU=0 Radius=4.2 StartAngle=1.5708 EndAngle=2.77639
    g137: LineSegment StartX=29.7 StartY=-27 StartZ=0 EndX=30.077 EndY=-27 EndZ=0
    g138: ArcOfCircle CenterX=29.7 CenterY=-29 CenterZ=0 NormalX=0 NormalY=0 NormalZ=1 AngleXU=0 Radius=2 StartAngle=1.5708 EndAngle=3.14159
    g139: LineSegment StartX=27.7 StartY=-29.6717 StartZ=0 EndX=27.7 EndY=-29 EndZ=0
    g140: LineSegment StartX=29.7 StartY=-34.4 StartZ=0 EndX=30.0335 EndY=-34.4 EndZ=0
    g141: ArcOfCircle CenterX=42 CenterY=-52.4 CenterZ=0 NormalX=0 NormalY=0 NormalZ=1 AngleXU=0 Radius=3.2 StartAngle=3.52599 EndAngle=4.71239
    g142: LineSegment StartX=42 StartY=-55.6 StartZ=0 EndX=44.2797 EndY=-55.6 EndZ=0
    g143: ArcOfCircle CenterX=47 CenterY=-52.4 CenterZ=0 NormalX=0 NormalY=0 NormalZ=1 AngleXU=0 Radius=4.2 StartAngle=4.00784 EndAngle=5.41694
    g144: LineSegment StartX=49.7203 StartY=-55.6 StartZ=0 EndX=51.7586 EndY=-55.6 EndZ=0
    g145: ArcOfCircle CenterX=53.65 CenterY=-54.95 CenterZ=0 NormalX=0 NormalY=0 NormalZ=1 AngleXU=0 Radius=2 StartAngle=3.4726 EndAngle=4.71239
    g146: LineSegment StartX=56 StartY=-56.95 StartZ=0 EndX=53.65 EndY=-56.95 EndZ=0
    g147: ArcOfCircle CenterX=56 CenterY=-54.95 CenterZ=0 NormalX=0 NormalY=0 NormalZ=1 AngleXU=0 Radius=2 StartAngle=4.71239 EndAngle=6.28319
    g148: LineSegment StartX=58 StartY=-53.6 StartZ=0 EndX=58 EndY=-54.95 EndZ=0
    g149: LineSegment StartX=56.3 StartY=-45.5 StartZ=0 EndX=56.3 EndY=-46.7717 EndZ=0
    g150: ArcOfCircle CenterX=54.3 CenterY=-45.5 CenterZ=0 NormalX=0 NormalY=0 NormalZ=1 AngleXU=0 Radius=2 StartAngle=4e-16 EndAngle=1.5708
    g151: LineSegment StartX=43 StartY=-43.5 StartZ=0 EndX=54.3 EndY=-43.5 EndZ=0
    g152: ArcOfCircle CenterX=43 CenterY=-47.7 CenterZ=0 NormalX=0 NormalY=0 NormalZ=1 AngleXU=0 Radius=4.2 StartAngle=1.5708 EndAngle=2.77639
    g153: LineSegment StartX=38.7 StartY=-46.2 StartZ=0 EndX=39.077 EndY=-46.2 EndZ=0
    g154: ArcOfCircle CenterX=38.7 CenterY=-48.2 CenterZ=0 NormalX=0 NormalY=0 NormalZ=1 AngleXU=0 Radius=2 StartAngle=1.5708 EndAngle=3.14159
    g155: LineSegment StartX=36.7 StartY=-51.6 StartZ=0 EndX=36.7 EndY=-48.2 EndZ=0
    g156: ArcOfCircle CenterX=38.7 CenterY=-51.6 CenterZ=0 NormalX=0 NormalY=0 NormalZ=1 AngleXU=0 Radius=2 StartAngle=3.14159 EndAngle=4.71239
    g157: LineSegment StartX=38.7 StartY=-53.6 StartZ=0 EndX=39.0335 EndY=-53.6 EndZ=0
    g158: ArcOfCircle CenterX=61 CenterY=-52.4 CenterZ=0 NormalX=0 NormalY=0 NormalZ=1 AngleXU=0 Radius=3.2 StartAngle=3.52599 EndAngle=4.71239
    g159: LineSegment StartX=61 StartY=-55.6 StartZ=0 EndX=63.2797 EndY=-55.6 EndZ=0
    g160: ArcOfCircle CenterX=66 CenterY=-52.4 CenterZ=0 NormalX=0 NormalY=0 NormalZ=1 AngleXU=0 Radius=4.2 StartAngle=4.00784 EndAngle=5.41694
    g161: LineSegment StartX=68.7203 StartY=-55.6 StartZ=0 EndX=70.7586 EndY=-55.6 EndZ=0
    g162: ArcOfCircle CenterX=72.65 CenterY=-54.95 CenterZ=0 NormalX=0 NormalY=0 NormalZ=1 AngleXU=0 Radius=2 StartAngle=3.4726 EndAngle=4.71239
    g163: LineSegment StartX=75 StartY=-56.95 StartZ=0 EndX=72.65 EndY=-56.95 EndZ=0
    g164: ArcOfCircle CenterX=75 CenterY=-54.95 CenterZ=0 NormalX=0 NormalY=0 NormalZ=1 AngleXU=0 Radius=2 StartAngle=4.71239 EndAngle=6.28319
    g165: LineSegment StartX=77 StartY=-49.85 StartZ=0 EndX=77 EndY=-54.95 EndZ=0
    g166: ArcOfCircle CenterX=75 CenterY=-49.85 CenterZ=0 NormalX=0 NormalY=0 NormalZ=1 AngleXU=0 Radius=2 StartAngle=0 EndAngle=1.42023
    g167: LineSegment StartX=75.3 StartY=-45.5 StartZ=0 EndX=75.3 EndY=-47.8726 EndZ=0
    g168: ArcOfCircle CenterX=73.3 CenterY=-45.5 CenterZ=0 NormalX=0 NormalY=0 NormalZ=1 AngleXU=0 Radius=2 StartAngle=4e-16 EndAngle=1.5708
    g169: LineSegment StartX=62 StartY=-43.5 StartZ=0 EndX=73.3 EndY=-43.5 EndZ=0
    g170: ArcOfCircle CenterX=62 CenterY=-47.7 CenterZ=0 NormalX=0 NormalY=0 NormalZ=1 AngleXU=0 Radius=4.2 StartAngle=1.5708 EndAngle=2.77639
    g171: LineSegment StartX=57.7 StartY=-46.2 StartZ=0 EndX=58.077 EndY=-46.2 EndZ=0
    g172: ArcOfCircle CenterX=57.7 CenterY=-48.2 CenterZ=0 NormalX=0 NormalY=0 NormalZ=1 AngleXU=0 Radius=2 StartAngle=1.5708 EndAngle=2.34619
    g173: LineSegment StartX=58 StartY=-53.6 StartZ=0 EndX=58.0335 EndY=-53.6 EndZ=0
    g174: ArcOfCircle CenterX=52 CenterY=-31 CenterZ=0 NormalX=0 NormalY=0 NormalZ=1 AngleXU=0 Radius=3.2 StartAngle=3.52599 EndAngle=4.71239
    g175: LineSegment StartX=52 StartY=-34.2 StartZ=0 EndX=54.2797 EndY=-34.2 EndZ=0
    g176: ArcOfCircle CenterX=57 CenterY=-31 CenterZ=0 NormalX=0 NormalY=0 NormalZ=1 AngleXU=0 Radius=4.2 StartAngle=4.00784 EndAngle=5.41694
    g177: LineSegment StartX=59.7203 StartY=-34.2 StartZ=0 EndX=61.7586 EndY=-34.2 EndZ=0
    g178: ArcOfCircle CenterX=63.65 CenterY=-33.55 CenterZ=0 NormalX=0 NormalY=0 NormalZ=1 AngleXU=0 Radius=2 StartAngle=3.4726 EndAngle=4.71239
    g179: LineSegment StartX=66 StartY=-35.55 StartZ=0 EndX=63.65 EndY=-35.55 EndZ=0
    g180: ArcOfCircle CenterX=66 CenterY=-33.55 CenterZ=0 NormalX=0 NormalY=0 NormalZ=1 AngleXU=0 Radius=2 StartAngle=4.71239 EndAngle=5.84422
    g181: ArcOfCircle CenterX=66 CenterY=-28.45 CenterZ=0 NormalX=0 NormalY=0 NormalZ=1 AngleXU=0 Radius=2 StartAngle=0.794834 EndAngle=1.42023
    g182: LineSegment StartX=66.3 StartY=-24.1 StartZ=0 EndX=66.3 EndY=-26.4726 EndZ=0
    g183: ArcOfCircle CenterX=64.3 CenterY=-24.1 CenterZ=0 NormalX=0 NormalY=0 NormalZ=1 AngleXU=0 Radius=2 StartAngle=4e-16 EndAngle=1.5708
    g184: LineSegment StartX=53 StartY=-22.1 StartZ=0 EndX=64.3 EndY=-22.1 EndZ=0
    g185: ArcOfCircle CenterX=53 CenterY=-26.3 CenterZ=0 NormalX=0 NormalY=0 NormalZ=1 AngleXU=0 Radius=4.2 StartAngle=1.5708 EndAngle=2.77639
    g186: LineSegment StartX=48.7 StartY=-24.8 StartZ=0 EndX=49.077 EndY=-24.8 EndZ=0
    g187: ArcOfCircle CenterX=48.7 CenterY=-26.8 CenterZ=0 NormalX=0 NormalY=0 NormalZ=1 AngleXU=0 Radius=2 StartAngle=1.5708 EndAngle=2.45837
    g188: LineSegment StartX=49 StartY=-32.2 StartZ=0 EndX=49.0335 EndY=-32.2 EndZ=0
    g189: ArcOfCircle CenterX=52 CenterY=-12 CenterZ=0 NormalX=0 NormalY=0 NormalZ=1 AngleXU=0 Radius=3.2 StartAngle=3.52599 EndAngle=4.71239
    g190: LineSegment StartX=52 StartY=-15.2 StartZ=0 EndX=54.2797 EndY=-15.2 EndZ=0
    g191: ArcOfCircle CenterX=57 CenterY=-12 CenterZ=0 NormalX=0 NormalY=0 NormalZ=1 AngleXU=0 Radius=4.2 StartAngle=4.00784 EndAngle=5.41694
    g192: LineSegment StartX=59.7203 StartY=-15.2 StartZ=0 EndX=61.7586 EndY=-15.2 EndZ=0
    g193: ArcOfCircle CenterX=63.65 CenterY=-14.55 CenterZ=0 NormalX=0 NormalY=0 NormalZ=1 AngleXU=0 Radius=2 StartAngle=3.4726 EndAngle=4.71239
    g194: LineSegment StartX=66 StartY=-16.55 StartZ=0 EndX=63.65 EndY=-16.55 EndZ=0
    g195: ArcOfCircle CenterX=66 CenterY=-14.55 CenterZ=0 NormalX=0 NormalY=0 NormalZ=1 AngleXU=0 Radius=2 StartAngle=4.71239 EndAngle=5.84422
    g196: ArcOfCircle CenterX=66 CenterY=-9.45 CenterZ=0 NormalX=0 NormalY=0 NormalZ=1 AngleXU=0 Radius=2 StartAngle=0.794834 EndAngle=1.42023
    g197: LineSegment StartX=66.3 StartY=-5.1 StartZ=0 EndX=66.3 EndY=-7.47263 EndZ=0
    g198: ArcOfCircle CenterX=64.3 CenterY=-5.1 CenterZ=0 NormalX=0 NormalY=0 NormalZ=1 AngleXU=0 Radius=2 StartAngle=4e-16 EndAngle=1.5708
    g199: LineSegment StartX=53 StartY=-3.1 StartZ=0 EndX=64.3 EndY=-3.1 EndZ=0
    g200: ArcOfCircle CenterX=53 CenterY=-7.3 CenterZ=0 NormalX=0 NormalY=0 NormalZ=1 AngleXU=0 Radius=4.2 StartAngle=1.5708 EndAngle=2.77639
    g201: LineSegment StartX=48.7 StartY=-5.8 StartZ=0 EndX=49.077 EndY=-5.8 EndZ=0
    g202: ArcOfCircle CenterX=48.7 CenterY=-7.8 CenterZ=0 NormalX=0 NormalY=0 NormalZ=1 AngleXU=0 Radius=2 StartAngle=1.5708 EndAngle=2.45837
    g203: LineSegment StartX=49 StartY=-13.2 StartZ=0 EndX=49.0335 EndY=-13.2 EndZ=0
    g204: ArcOfCircle CenterX=52 CenterY=7 CenterZ=0 NormalX=0 NormalY=0 NormalZ=1 AngleXU=0 Radius=3.2 StartAngle=3.52599 EndAngle=4.71239
    g205: LineSegment StartX=52 StartY=3.8 StartZ=0 EndX=54.2797 EndY=3.8 EndZ=0
    g206: ArcOfCircle CenterX=57 CenterY=7 CenterZ=0 NormalX=0 NormalY=0 NormalZ=1 AngleXU=0 Radius=4.2 StartAngle=4.00784 EndAngle=5.41694
    g207: LineSegment StartX=59.7203 StartY=3.8 StartZ=0 EndX=61.7586 EndY=3.8 EndZ=0
    g208: ArcOfCircle CenterX=63.65 CenterY=4.45 CenterZ=0 NormalX=0 NormalY=0 NormalZ=1 AngleXU=0 Radius=2 StartAngle=3.4726 EndAngle=4.71239
    g209: LineSegment StartX=66 StartY=2.45 StartZ=0 EndX=63.65 EndY=2.45 EndZ=0
    g210: ArcOfCircle CenterX=66 CenterY=4.45 CenterZ=0 NormalX=0 NormalY=0 NormalZ=1 AngleXU=0 Radius=2 StartAngle=4.71239 EndAngle=5.84422
    g211: ArcOfCircle CenterX=66 CenterY=9.55 CenterZ=0 NormalX=0 NormalY=0 NormalZ=1 AngleXU=0 Radius=2 StartAngle=0.794834 EndAngle=1.42023
    g212: LineSegment StartX=66.3 StartY=13.9 StartZ=0 EndX=66.3 EndY=11.5274 EndZ=0
    g213: ArcOfCircle CenterX=64.3 CenterY=13.9 CenterZ=0 NormalX=0 NormalY=0 NormalZ=1 AngleXU=0 Radius=2 StartAngle=4e-16 EndAngle=1.5708
    g214: LineSegment StartX=53 StartY=15.9 StartZ=0 EndX=64.3 EndY=15.9 EndZ=0
    g215: ArcOfCircle CenterX=53 CenterY=11.7 CenterZ=0 NormalX=0 NormalY=0 NormalZ=1 AngleXU=0 Radius=4.2 StartAngle=1.5708 EndAngle=2.77639
    g216: LineSegment StartX=48.7 StartY=13.2 StartZ=0 EndX=49.077 EndY=13.2 EndZ=0
    g217: ArcOfCircle CenterX=48.7 CenterY=11.2 CenterZ=0 NormalX=0 NormalY=0 NormalZ=1 AngleXU=0 Radius=2 StartAngle=1.5708 EndAngle=2.45837
    g218: LineSegment StartX=49 StartY=5.8 StartZ=0 EndX=49.0335 EndY=5.8 EndZ=0
    g219: ArcOfCircle CenterX=71 CenterY=4.8 CenterZ=0 NormalX=0 NormalY=0 NormalZ=1 AngleXU=0 Radius=3.2 StartAngle=3.52599 EndAngle=4.71239
    g220: LineSegment StartX=71 StartY=1.6 StartZ=0 EndX=73.2797 EndY=1.6 EndZ=0
    g221: ArcOfCircle CenterX=76 CenterY=4.8 CenterZ=0 NormalX=0 NormalY=0 NormalZ=1 AngleXU=0 Radius=4.2 StartAngle=4.00784 EndAngle=5.41694
    g222: LineSegment StartX=78.7203 StartY=1.6 StartZ=0 EndX=80.7586 EndY=1.6 EndZ=0
    g223: ArcOfCircle CenterX=82.65 CenterY=2.25 CenterZ=0 NormalX=0 NormalY=0 NormalZ=1 AngleXU=0 Radius=2 StartAngle=3.4726 EndAngle=4.71239
    g224: LineSegment StartX=85 StartY=0.25 StartZ=0 EndX=82.65 EndY=0.25 EndZ=0
    g225: ArcOfCircle CenterX=85 CenterY=2.25 CenterZ=0 NormalX=0 NormalY=0 NormalZ=1 AngleXU=0 Radius=2 StartAngle=4.71239 EndAngle=5.84422
    g226: ArcOfCircle CenterX=85 CenterY=7.35 CenterZ=0 NormalX=0 NormalY=0 NormalZ=1 AngleXU=0 Radius=2 StartAngle=0.794834 EndAngle=1.42023
    g227: LineSegment StartX=85.3 StartY=11.7 StartZ=0 EndX=85.3 EndY=9.32737 EndZ=0
    g228: ArcOfCircle CenterX=83.3 CenterY=11.7 CenterZ=0 NormalX=0 NormalY=0 NormalZ=1 AngleXU=0 Radius=2 StartAngle=4e-16 EndAngle=1.5708
    g229: LineSegment StartX=72 StartY=13.7 StartZ=0 EndX=83.3 EndY=13.7 EndZ=0
    g230: ArcOfCircle CenterX=72 CenterY=9.5 CenterZ=0 NormalX=0 NormalY=0 NormalZ=1 AngleXU=0 Radius=4.2 StartAngle=1.5708 EndAngle=2.77639
    g231: LineSegment StartX=67.7 StartY=11 StartZ=0 EndX=68.077 EndY=11 EndZ=0
    g232: ArcOfCircle CenterX=67.7 CenterY=9 CenterZ=0 NormalX=0 NormalY=0 NormalZ=1 AngleXU=0 Radius=2 StartAngle=1.5708 EndAngle=1.72096
    g233: LineSegment StartX=67.8104 StartY=3.6 StartZ=0 EndX=68.0335 EndY=3.6 EndZ=0
    g234: ArcOfCircle CenterX=71 CenterY=-14.2 CenterZ=0 NormalX=0 NormalY=0 NormalZ=1 AngleXU=0 Radius=3.2 StartAngle=3.52599 EndAngle=4.71239
    g235: LineSegment StartX=71 StartY=-17.4 StartZ=0 EndX=73.2797 EndY=-17.4 EndZ=0
    g236: ArcOfCircle CenterX=76 CenterY=-14.2 CenterZ=0 NormalX=0 NormalY=0 NormalZ=1 AngleXU=0 Radius=4.2 StartAngle=4.00784 EndAngle=5.41694
    g237: LineSegment StartX=78.7203 StartY=-17.4 StartZ=0 EndX=80.7586 EndY=-17.4 EndZ=0
    g238: ArcOfCircle CenterX=82.65 CenterY=-16.75 CenterZ=0 NormalX=0 NormalY=0 NormalZ=1 AngleXU=0 Radius=2 StartAngle=3.4726 EndAngle=4.71239
    g239: LineSegment StartX=85 StartY=-18.75 StartZ=0 EndX=82.65 EndY=-18.75 EndZ=0
    g240: ArcOfCircle CenterX=85 CenterY=-16.75 CenterZ=0 NormalX=0 NormalY=0 NormalZ=1 AngleXU=0 Radius=2 StartAngle=4.71239 EndAngle=5.84422
    g241: ArcOfCircle CenterX=85 CenterY=-11.65 CenterZ=0 NormalX=0 NormalY=0 NormalZ=1 AngleXU=0 Radius=2 StartAngle=0.794834 EndAngle=1.42023
    g242: LineSegment StartX=85.3 StartY=-7.3 StartZ=0 EndX=85.3 EndY=-9.67263 EndZ=0
    g243: ArcOfCircle CenterX=83.3 CenterY=-7.3 CenterZ=0 NormalX=0 NormalY=0 NormalZ=1 AngleXU=0 Radius=2 StartAngle=4e-16 EndAngle=1.5708
    g244: LineSegment StartX=72 StartY=-5.3 StartZ=0 EndX=83.3 EndY=-5.3 EndZ=0
    g245: ArcOfCircle CenterX=72 CenterY=-9.5 CenterZ=0 NormalX=0 NormalY=0 NormalZ=1 AngleXU=0 Radius=4.2 StartAngle=1.5708 EndAngle=2.77639
    g246: LineSegment StartX=67.7 StartY=-8 StartZ=0 EndX=68.077 EndY=-8 EndZ=0
    g247: ArcOfCircle CenterX=67.7 CenterY=-10 CenterZ=0 NormalX=0 NormalY=0 NormalZ=1 AngleXU=0 Radius=2 StartAngle=1.5708 EndAngle=1.72096
    g248: LineSegment StartX=67.8104 StartY=-15.4 StartZ=0 EndX=68.0335 EndY=-15.4 EndZ=0
    g249: ArcOfCircle CenterX=71 CenterY=-33.2 CenterZ=0 NormalX=0 NormalY=0 NormalZ=1 AngleXU=0 Radius=3.2 StartAngle=3.52599 EndAngle=4.71239
    g250: LineSegment StartX=71 StartY=-36.4 StartZ=0 EndX=73.2797 EndY=-36.4 EndZ=0
    g251: ArcOfCircle CenterX=76 CenterY=-33.2 CenterZ=0 NormalX=0 NormalY=0 NormalZ=1 AngleXU=0 Radius=4.2 StartAngle=4.00784 EndAngle=5.41694
    g252: LineSegment StartX=78.7203 StartY=-36.4 StartZ=0 EndX=80.7586 EndY=-36.4 EndZ=0
    g253: ArcOfCircle CenterX=82.65 CenterY=-35.75 CenterZ=0 NormalX=0 NormalY=0 NormalZ=1 AngleXU=0 Radius=2 StartAngle=3.4726 EndAngle=4.71239
    g254: LineSegment StartX=85 StartY=-37.75 StartZ=0 EndX=82.65 EndY=-37.75 EndZ=0
    g255: ArcOfCircle CenterX=85 CenterY=-35.75 CenterZ=0 NormalX=0 NormalY=0 NormalZ=1 AngleXU=0 Radius=2 StartAngle=4.71239 EndAngle=5.84422
    g256: ArcOfCircle CenterX=85 CenterY=-30.65 CenterZ=0 NormalX=0 NormalY=0 NormalZ=1 AngleXU=0 Radius=2 StartAngle=0.794834 EndAngle=1.42023
    g257: LineSegment StartX=85.3 StartY=-26.3 StartZ=0 EndX=85.3 EndY=-28.6726 EndZ=0
    g258: ArcOfCircle CenterX=83.3 CenterY=-26.3 CenterZ=0 NormalX=0 NormalY=0 NormalZ=1 AngleXU=0 Radius=2 StartAngle=4e-16 EndAngle=1.5708
    g259: LineSegment StartX=72 StartY=-24.3 StartZ=0 EndX=83.3 EndY=-24.3 EndZ=0
    g260: ArcOfCircle CenterX=72 CenterY=-28.5 CenterZ=0 NormalX=0 NormalY=0 NormalZ=1 AngleXU=0 Radius=4.2 StartAngle=1.5708 EndAngle=2.77639
    g261: LineSegment StartX=67.7 StartY=-27 StartZ=0 EndX=68.077 EndY=-27 EndZ=0
    g262: ArcOfCircle CenterX=67.7 CenterY=-29 CenterZ=0 NormalX=0 NormalY=0 NormalZ=1 AngleXU=0 Radius=2 StartAngle=1.5708 EndAngle=1.72096
    g263: LineSegment StartX=67.8104 StartY=-34.4 StartZ=0 EndX=68.0335 EndY=-34.4 EndZ=0
    g264: ArcOfCircle CenterX=90 CenterY=-35.4 CenterZ=0 NormalX=0 NormalY=0 NormalZ=1 AngleXU=0 Radius=3.2 StartAngle=3.52599 EndAngle=4.71239
    g265: LineSegment StartX=90 StartY=-38.6 StartZ=0 EndX=92.2797 EndY=-38.6 EndZ=0
    g266: ArcOfCircle CenterX=95 CenterY=-35.4 CenterZ=0 NormalX=0 NormalY=0 NormalZ=1 AngleXU=0 Radius=4.2 StartAngle=4.00784 EndAngle=5.41694
    g267: LineSegment StartX=97.7203 StartY=-38.6 StartZ=0 EndX=99.7586 EndY=-38.6 EndZ=0
    g268: ArcOfCircle CenterX=101.65 CenterY=-37.95 CenterZ=0 NormalX=0 NormalY=0 NormalZ=1 AngleXU=0 Radius=2 StartAngle=3.4726 EndAngle=4.71239
    g269: LineSegment StartX=104 StartY=-39.95 StartZ=0 EndX=101.65 EndY=-39.95 EndZ=0
    g270: ArcOfCircle CenterX=104 CenterY=-37.95 CenterZ=0 NormalX=0 NormalY=0 NormalZ=1 AngleXU=0 Radius=2 StartAngle=4.71239 EndAngle=6.28319
    g271: LineSegment StartX=106 StartY=-32.85 StartZ=0 EndX=106 EndY=-37.95 EndZ=0
    g272: ArcOfCircle CenterX=104 CenterY=-32.85 CenterZ=0 NormalX=0 NormalY=0 NormalZ=1 AngleXU=0 Radius=2 StartAngle=0 EndAngle=1.42023
    g273: LineSegment StartX=104.3 StartY=-28.5 StartZ=0 EndX=104.3 EndY=-30.8726 EndZ=0
    g274: ArcOfCircle CenterX=102.3 CenterY=-28.5 CenterZ=0 NormalX=0 NormalY=0 NormalZ=1 AngleXU=0 Radius=2 StartAngle=4e-16 EndAngle=1.5708
    g275: LineSegment StartX=91 StartY=-26.5 StartZ=0 EndX=102.3 EndY=-26.5 EndZ=0
    g276: ArcOfCircle CenterX=91 CenterY=-30.7 CenterZ=0 NormalX=0 NormalY=0 NormalZ=1 AngleXU=0 Radius=4.2 StartAngle=1.5708 EndAngle=2.77639
    g277: LineSegment StartX=86.7 StartY=-29.2 StartZ=0 EndX=87.077 EndY=-29.2 EndZ=0
    g278: ArcOfCircle CenterX=86.7 CenterY=-31.2 CenterZ=0 NormalX=0 NormalY=0 NormalZ=1 AngleXU=0 Radius=2 StartAngle=1.5708 EndAngle=1.72096
    g279: LineSegment StartX=86.8104 StartY=-36.6 StartZ=0 EndX=87.0335 EndY=-36.6 EndZ=0
    g280: ArcOfCircle CenterX=90 CenterY=-16.4 CenterZ=0 NormalX=0 NormalY=0 NormalZ=1 AngleXU=0 Radius=3.2 StartAngle=3.52599 EndAngle=4.71239
    g281: LineSegment StartX=90 StartY=-19.6 StartZ=0 EndX=92.2797 EndY=-19.6 EndZ=0
    g282: ArcOfCircle CenterX=95 CenterY=-16.4 CenterZ=0 NormalX=0 NormalY=0 NormalZ=1 AngleXU=0 Radius=4.2 StartAngle=4.00784 EndAngle=5.41694
    g283: LineSegment StartX=97.7203 StartY=-19.6 StartZ=0 EndX=99.7586 EndY=-19.6 EndZ=0
    g284: ArcOfCircle CenterX=101.65 CenterY=-18.95 CenterZ=0 NormalX=0 NormalY=0 NormalZ=1 AngleXU=0 Radius=2 StartAngle=3.4726 EndAngle=4.71239
    g285: LineSegment StartX=104 StartY=-20.95 StartZ=0 EndX=101.65 EndY=-20.95 EndZ=0
    g286: ArcOfCircle CenterX=104 CenterY=-18.95 CenterZ=0 NormalX=0 NormalY=0 NormalZ=1 AngleXU=0 Radius=2 StartAngle=4.71239 EndAngle=6.28319
    g287: LineSegment StartX=106 StartY=-13.85 StartZ=0 EndX=106 EndY=-18.95 EndZ=0
    g288: ArcOfCircle CenterX=104 CenterY=-13.85 CenterZ=0 NormalX=0 NormalY=0 NormalZ=1 AngleXU=0 Radius=2 StartAngle=0 EndAngle=1.42023
    g289: LineSegment StartX=104.3 StartY=-9.5 StartZ=0 EndX=104.3 EndY=-11.8726 EndZ=0
    g290: ArcOfCircle CenterX=102.3 CenterY=-9.5 CenterZ=0 NormalX=0 NormalY=0 NormalZ=1 AngleXU=0 Radius=2 StartAngle=4e-16 EndAngle=1.5708
    g291: LineSegment StartX=91 StartY=-7.5 StartZ=0 EndX=102.3 EndY=-7.5 EndZ=0
    g292: ArcOfCircle CenterX=91 CenterY=-11.7 CenterZ=0 NormalX=0 NormalY=0 NormalZ=1 AngleXU=0 Radius=4.2 StartAngle=1.5708 EndAngle=2.77639
    g293: LineSegment StartX=86.7 StartY=-10.2 StartZ=0 EndX=87.077 EndY=-10.2 EndZ=0
    g294: ArcOfCircle CenterX=86.7 CenterY=-12.2 CenterZ=0 NormalX=0 NormalY=0 NormalZ=1 AngleXU=0 Radius=2 StartAngle=1.5708 EndAngle=1.72096
    g295: LineSegment StartX=86.8104 StartY=-17.6 StartZ=0 EndX=87.0335 EndY=-17.6 EndZ=0
    g296: ArcOfCircle CenterX=90 CenterY=2.6 CenterZ=0 NormalX=0 NormalY=0 NormalZ=1 AngleXU=0 Radius=3.2 StartAngle=3.52599 EndAngle=4.71239
    g297: LineSegment StartX=90 StartY=-0.6 StartZ=0 EndX=92.2797 EndY=-0.6 EndZ=0
    g298: ArcOfCircle CenterX=95 CenterY=2.6 CenterZ=0 NormalX=0 NormalY=0 NormalZ=1 AngleXU=0 Radius=4.2 StartAngle=4.00784 EndAngle=5.41694
    g299: LineSegment StartX=97.7203 StartY=-0.6 StartZ=0 EndX=99.7586 EndY=-0.6 EndZ=0
    g300: ArcOfCircle CenterX=101.65 CenterY=0.05 CenterZ=0 NormalX=0 NormalY=0 NormalZ=1 AngleXU=0 Radius=2 StartAngle=3.4726 EndAngle=4.71239
    g301: LineSegment StartX=104 StartY=-1.95 StartZ=0 EndX=101.65 EndY=-1.95 EndZ=0
    g302: ArcOfCircle CenterX=104 CenterY=0.05 CenterZ=0 NormalX=0 NormalY=0 NormalZ=1 AngleXU=0 Radius=2 StartAngle=4.71239 EndAngle=6.28319
    g303: LineSegment StartX=106 StartY=5.15 StartZ=0 EndX=106 EndY=0.05 EndZ=0
    g304: ArcOfCircle CenterX=104 CenterY=5.15 CenterZ=0 NormalX=0 NormalY=0 NormalZ=1 AngleXU=0 Radius=2 StartAngle=0 EndAngle=1.42023
    g305: LineSegment StartX=104.3 StartY=9.5 StartZ=0 EndX=104.3 EndY=7.12737 EndZ=0
    g306: ArcOfCircle CenterX=102.3 CenterY=9.5 CenterZ=0 NormalX=0 NormalY=0 NormalZ=1 AngleXU=0 Radius=2 StartAngle=4e-16 EndAngle=1.5708
    g307: LineSegment StartX=91 StartY=11.5 StartZ=0 EndX=102.3 EndY=11.5 EndZ=0
    g308: ArcOfCircle CenterX=91 CenterY=7.3 CenterZ=0 NormalX=0 NormalY=0 NormalZ=1 AngleXU=0 Radius=4.2 StartAngle=1.5708 EndAngle=2.77639
    g309: LineSegment StartX=86.7 StartY=8.8 StartZ=0 EndX=87.077 EndY=8.8 EndZ=0
    g310: ArcOfCircle CenterX=86.7 CenterY=6.8 CenterZ=0 NormalX=0 NormalY=0 NormalZ=1 AngleXU=0 Radius=2 StartAngle=1.5708 EndAngle=1.72096
    g311: LineSegment StartX=86.8104 StartY=1.4 StartZ=0 EndX=87.0335 EndY=1.4 EndZ=0
  constraints (467):
    c: Coincident(g0,g1)
    c: Horizontal(g1)
    c: Coincident(g1,g2)
    c: Coincident(g2,g3)
    c: Horizontal(g3)
    c: Coincident(g3,g4)
    c: Coincident(g4,g5)
    c: Horizontal(g5)
    c: Coincident(g5,g6)
    c: Coincident(g6,g7)
    c: Vertical(g7)
    c: Vertical(g8)
    c: Coincident(g8,g9)
    c: Coincident(g9,g10)
    c: Horizontal(g10)
    c: Coincident(g10,g11)
    c: Coincident(g11,g12)
    c: Horizontal(g12)
    c: Coincident(g12,g13)
    c: Coincident(g13,g14)
    c: Vertical(g14)
    c: Coincident(g14,g15)
    c: Coincident(g15,g16)
    c: Horizontal(g16)
    c: Coincident(g16,g0)
    c: Coincident(g17,g18)
    c: Horizontal(g18)
    c: Coincident(g18,g19)
    c: Coincident(g19,g20)
    c: Horizontal(g20)
    c: Coincident(g20,g21)
    c: Coincident(g21,g22)
    c: Horizontal(g22)
    c: Coincident(g22,g23)
    c: Coincident(g23,g24)
    c: Vertical(g24)
    c: Vertical(g25)
    c: Coincident(g25,g26)
    c: Coincident(g26,g27)
    c: Horizontal(g27)
    c: Coincident(g27,g28)
    c: Coincident(g28,g29)
    c: Horizontal(g29)
    c: Coincident(g29,g30)
    c: Coincident(g30,g31)
    c: Vertical(g31)
    c: Coincident(g31,g32)
    c: Coincident(g32,g33)
    c: Horizontal(g33)
    c: Coincident(g33,g17)
    c: Coincident(g34,g35)
    c: Horizontal(g35)
    c: Coincident(g35,g36)
    c: Coincident(g36,g37)
    c: Horizontal(g37)
    c: Coincident(g37,g38)
    c: Coincident(g38,g39)
    c: Horizontal(g39)
    c: Coincident(g39,g40)
    c: Coincident(g40,g41)
    c: Vertical(g41)
    c: Vertical(g42)
    c: Coincident(g42,g43)
    c: Coincident(g43,g44)
    c: Horizontal(g44)
    c: Coincident(g44,g45)
    c: Coincident(g45,g46)
    c: Horizontal(g46)
    c: Coincident(g46,g47)
    c: Coincident(g47,g48)
    c: Vertical(g48)
    c: Coincident(g48,g49)
    c: Coincident(g49,g50)
    c: Horizontal(g50)
    c: Coincident(g50,g34)
    c: Coincident(g51,g52)
    c: Horizontal(g52)
    c: Coincident(g52,g53)
    c: Coincident(g53,g54)
    c: Horizontal(g54)
    c: Coincident(g54,g55)
    c: Coincident(g55,g56)
    c: Horizontal(g56)
    c: Coincident(g56,g57)
    c: Coincident(g57,g58)
    c: Vertical(g58)
    c: Coincident(g58,g59)
    c: Coincident(g60,g61)
    c: Horizontal(g61)
    c: Coincident(g61,g62)
    c: Coincident(g62,g63)
    c: Horizontal(g63)
    c: Coincident(g63,g64)
    c: Horizontal(g65)
    c: Coincident(g65,g51)
    c: Coincident(g66,g67)
    c: Horizontal(g67)
    c: Coincident(g67,g68)
    c: Coincident(g68,g69)
    c: Horizontal(g69)
    c: Coincident(g69,g70)
    c: Coincident(g70,g71)
    c: Horizontal(g71)
    c: Coincident(g71,g72)
    c: Coincident(g72,g73)
    c: Vertical(g73)
    c: Coincident(g73,g74)
    c: Coincident(g75,g76)
    c: Horizontal(g76)
    c: Coincident(g76,g77)
    c: Coincident(g77,g78)
    c: Horizontal(g78)
    c: Coincident(g78,g79)
    c: Horizontal(g80)
    c: Coincident(g80,g66)
    c: Coincident(g81,g82)
    c: Horizontal(g82)
    c: Coincident(g82,g83)
    c: Coincident(g83,g84)
    c: Horizontal(g84)
    c: Coincident(g84,g85)
    c: Coincident(g85,g86)
    c: Horizontal(g86)
    c: Coincident(g86,g87)
    c: Coincident(g87,g88)
    c: Vertical(g88)
    c: Coincident(g88,g89)
    c: Coincident(g90,g91)
    c: Horizontal(g91)
    c: Coincident(g91,g92)
    c: Coincident(g92,g93)
    c: Horizontal(g93)
    c: Coincident(g93,g94)
    c: Horizontal(g95)
    c: Coincident(g95,g81)
    c: Coincident(g96,g97)
    c: Horizontal(g97)
    c: Coincident(g97,g98)
    c: Coincident(g98,g99)
    c: Horizontal(g99)
    c: Coincident(g99,g100)
    c: Coincident(g100,g101)
    c: Horizontal(g101)
    c: Coincident(g101,g102)
    c: Coincident(g102,g103)
    c: Vertical(g103)
    c: Coincident(g104,g105)
    c: Horizontal(g105)
    c: Coincident(g105,g106)
    c: Coincident(g106,g107)
    c: Horizontal(g107)
    c: Coincident(g107,g108)
    c: Coincident(g108,g109)
    c: Vertical(g109)
    c: Horizontal(g110)
    c: Coincident(g110,g96)
    c: Coincident(g111,g112)
    c: Horizontal(g112)
    c: Coincident(g112,g113)
    c: Coincident(g113,g114)
    c: Horizontal(g114)
    c: Coincident(g114,g115)
    c: Coincident(g115,g116)
    c: Horizontal(g116)
    c: Coincident(g116,g117)
    c: Coincident(g117,g118)
    c: Vertical(g118)
    c: Coincident(g119,g120)
    c: Horizontal(g120)
    c: Coincident(g120,g121)
    c: Coincident(g121,g122)
    c: Horizontal(g122)
    c: Coincident(g122,g123)
    c: Coincident(g123,g124)
    c: Vertical(g124)
    c: Horizontal(g125)
    c: Coincident(g125,g111)
    c: Coincident(g126,g127)
    c: Horizontal(g127)
    c: Coincident(g127,g128)
    c: Coincident(g128,g129)
    c: Horizontal(g129)
    c: Coincident(g129,g130)
    c: Coincident(g130,g131)
    c: Horizontal(g131)
    c: Coincident(g131,g132)
    c: Coincident(g132,g133)
    c: Vertical(g133)
    c: Coincident(g134,g135)
    c: Horizontal(g135)
    c: Coincident(g135,g136)
    c: Coincident(g136,g137)
    c: Horizontal(g137)
    c: Coincident(g137,g138)
    c: Coincident(g138,g139)
    c: Vertical(g139)
    c: Horizontal(g140)
    c: Coincident(g140,g126)
    c: Coincident(g141,g142)
    c: Horizontal(g142)
    c: Coincident(g142,g143)
    c: Coincident(g143,g144)
    c: Horizontal(g144)
    c: Coincident(g144,g145)
    c: Coincident(g145,g146)
    c: Horizontal(g146)
    c: Coincident(g146,g147)
    c: Coincident(g147,g148)
    c: Vertical(g148)
    c: Vertical(g149)
    c: Coincident(g149,g150)
    c: Coincident(g150,g151)
    c: Horizontal(g151)
    c: Coincident(g151,g152)
    c: Coincident(g152,g153)
    c: Horizontal(g153)
    c: Coincident(g153,g154)
    c: Coincident(g154,g155)
    c: Vertical(g155)
    c: Coincident(g155,g156)
    c: Coincident(g156,g157)
    c: Horizontal(g157)
    c: Coincident(g157,g141)
    c: Coincident(g158,g159)
    c: Horizontal(g159)
    c: Coincident(g159,g160)
    c: Coincident(g160,g161)
    c: Horizontal(g161)
    c: Coincident(g161,g162)
    c: Coincident(g162,g163)
    c: Horizontal(g163)
    c: Coincident(g163,g164)
    c: Coincident(g164,g165)
    c: Vertical(g165)
    c: Coincident(g165,g166)
    c: Coincident(g166,g167)
    c: Vertical(g167)
    c: Coincident(g167,g168)
    c: Coincident(g168,g169)
    c: Horizontal(g169)
    c: Coincident(g169,g170)
    c: Coincident(g170,g171)
    c: Horizontal(g171)
    c: Coincident(g171,g172)
    c: Horizontal(g173)
    c: Coincident(g173,g158)
    c: Coincident(g174,g175)
    c: Horizontal(g175)
    c: Coincident(g175,g176)
    c: Coincident(g176,g177)
    c: Horizontal(g177)
    c: Coincident(g177,g178)
    c: Coincident(g178,g179)
    c: Horizontal(g179)
    c: Coincident(g179,g180)
    c: Coincident(g181,g182)
    c: Vertical(g182)
    c: Coincident(g182,g183)
    c: Coincident(g183,g184)
    c: Horizontal(g184)
    c: Coincident(g184,g185)
    c: Coincident(g185,g186)
    c: Horizontal(g186)
    c: Coincident(g186,g187)
    c: Horizontal(g188)
    c: Coincident(g188,g174)
    c: Coincident(g189,g190)
    c: Horizontal(g190)
    c: Coincident(g190,g191)
    c: Coincident(g191,g192)
    c: Horizontal(g192)
    c: Coincident(g192,g193)
    c: Coincident(g193,g194)
    c: Horizontal(g194)
    c: Coincident(g194,g195)
    c: Coincident(g196,g197)
    c: Vertical(g197)
    c: Coincident(g197,g198)
    c: Coincident(g198,g199)
    c: Horizontal(g199)
    c: Coincident(g199,g200)
    c: Coincident(g200,g201)
    c: Horizontal(g201)
    c: Coincident(g201,g202)
    c: Horizontal(g203)
    c: Coincident(g203,g189)
    c: Coincident(g204,g205)
    c: Horizontal(g205)
    c: Coincident(g205,g206)
    c: Coincident(g206,g207)
    c: Horizontal(g207)
    c: Coincident(g207,g208)
    c: Coincident(g208,g209)
    c: Horizontal(g209)
    c: Coincident(g209,g210)
    c: Coincident(g211,g212)
    c: Vertical(g212)
    c: Coincident(g212,g213)
    c: Coincident(g213,g214)
    c: Horizontal(g214)
    c: Coincident(g214,g215)
    c: Coincident(g215,g216)
    c: Horizontal(g216)
    c: Coincident(g216,g217)
    c: Horizontal(g218)
    c: Coincident(g218,g204)
    c: Coincident(g219,g220)
    c: Horizontal(g220)
    c: Coincident(g220,g221)
    c: Coincident(g221,g222)
    c: Horizontal(g222)
    c: Coincident(g222,g223)
    c: Coincident(g223,g224)
    c: Horizontal(g224)
    c: Coincident(g224,g225)
    c: Coincident(g226,g227)
    c: Vertical(g227)
    c: Coincident(g227,g228)
    c: Coincident(g228,g229)
    c: Horizontal(g229)
    c: Coincident(g229,g230)
    c: Coincident(g230,g231)
    c: Horizontal(g231)
    c: Coincident(g231,g232)
    c: Horizontal(g233)
    c: Coincident(g233,g219)
    c: Coincident(g234,g235)
    c: Horizontal(g235)
    c: Coincident(g235,g236)
    c: Coincident(g236,g237)
    c: Horizontal(g237)
    c: Coincident(g237,g238)
    c: Coincident(g238,g239)
    c: Horizontal(g239)
    c: Coincident(g239,g240)
    c: Coincident(g241,g242)
    c: Vertical(g242)
    c: Coincident(g242,g243)
    c: Coincident(g243,g244)
    c: Horizontal(g244)
    c: Coincident(g244,g245)
    c: Coincident(g245,g246)
    c: Horizontal(g246)
    c: Coincident(g246,g247)
    c: Horizontal(g248)
    c: Coincident(g248,g234)
    c: Coincident(g249,g250)
    c: Horizontal(g250)
    c: Coincident(g250,g251)
    c: Coincident(g251,g252)
    c: Horizontal(g252)
    c: Coincident(g252,g253)
    c: Coincident(g253,g254)
    c: Horizontal(g254)
    c: Coincident(g254,g255)
    c: Coincident(g256,g257)
    c: Vertical(g257)
    c: Coincident(g257,g258)
    c: Coincident(g258,g259)
    c: Horizontal(g259)
    c: Coincident(g259,g260)
    c: Coincident(g260,g261)
    c: Horizontal(g261)
    c: Coincident(g261,g262)
    c: Horizontal(g263)
    c: Coincident(g263,g249)
    c: Coincident(g264,g265)
    c: Horizontal(g265)
    c: Coincident(g265,g266)
    c: Coincident(g266,g267)
    c: Horizontal(g267)
    c: Coincident(g267,g268)
    c: Coincident(g268,g269)
    c: Horizontal(g269)
    c: Coincident(g269,g270)
    c: Coincident(g270,g271)
    c: Vertical(g271)
    c: Coincident(g271,g272)
    c: Coincident(g272,g273)
    c: Vertical(g273)
    c: Coincident(g273,g274)
    c: Coincident(g274,g275)
    c: Horizontal(g275)
    c: Coincident(g275,g276)
    c: Coincident(g276,g277)
    c: Horizontal(g277)
    c: Coincident(g277,g278)
    c: Horizontal(g279)
    c: Coincident(g279,g264)
    c: Coincident(g280,g281)
    c: Horizontal(g281)
    c: Coincident(g281,g282)
    c: Coincident(g282,g283)
    c: Horizontal(g283)
    c: Coincident(g283,g284)
    c: Coincident(g284,g285)
    c: Horizontal(g285)
    c: Coincident(g285,g286)
    c: Coincident(g286,g287)
    c: Vertical(g287)
    c: Coincident(g287,g288)
    c: Coincident(g288,g289)
    c: Vertical(g289)
    c: Coincident(g289,g290)
    c: Coincident(g290,g291)
    c: Horizontal(g291)
    c: Coincident(g291,g292)
    c: Coincident(g292,g293)
    c: Horizontal(g293)
    c: Coincident(g293,g294)
    c: Horizontal(g295)
    c: Coincident(g295,g280)
    c: Coincident(g296,g297)
    c: Horizontal(g297)
    c: Coincident(g297,g298)
    c: Coincident(g298,g299)
    c: Horizontal(g299)
    c: Coincident(g299,g300)
    c: Coincident(g300,g301)
    c: Horizontal(g301)
    c: Coincident(g301,g302)
    c: Coincident(g302,g303)
    c: Vertical(g303)
    c: Coincident(g303,g304)
    c: Coincident(g304,g305)
    c: Vertical(g305)
    c: Coincident(g305,g306)
    c: Coincident(g306,g307)
    c: Horizontal(g307)
    c: Coincident(g307,g308)
    c: Coincident(g308,g309)
    c: Horizontal(g309)
    c: Coincident(g309,g310)
    c: Horizontal(g311)
    c: Coincident(g311,g296)
    c: Coincident(g8,g94)
    c: Coincident(g95,g7)
    c: Coincident(g109,g90)
    c: PointOnObject(g89,g110)
    c: Coincident(g217,g104)
    c: Coincident(g218,g103)
    c: Coincident(g211,g232)
    c: Coincident(g233,g210)
    c: Coincident(g226,g310)
    c: Coincident(g311,g225)
    c: Coincident(g241,g294)
    c: Coincident(g240,g295)
    c: Coincident(g195,g248)
    c: Coincident(g196,g247)
    c: Coincident(g118,g203)
    c: Coincident(g119,g202)
    c: PointOnObject(g74,g125)
    c: Coincident(g75,g124)
    c: Coincident(g25,g79)
    c: Coincident(g24,g80)
    c: Coincident(g41,g65)
    c: Coincident(g64,g42)
    c: Coincident(g60,g139)
    c: PointOnObject(g59,g140)
    c: Coincident(g133,g188)
    c: Coincident(g187,g134)
    c: Coincident(g262,g181)
    c: Coincident(g263,g180)
    c: Coincident(g278,g256)
    c: Coincident(g255,g279)
    c: Coincident(g149,g172)
    c: Coincident(g148,g173)
FEATURE [Sketcher::SketchObject] Sketch005
  FullyConstrained = false
  sketch-geometry (1):
    g0: LineSegment StartX=-66.423 StartY=17.6018 StartZ=0 EndX=18.1002 EndY=-66.9214 EndZ=0
  constraints (1):
    c: Angle(g0,g-2) = 2.35619
FEATURE [Part::FeaturePython] Array  label="diagonal array"  # Draft array (typed FeaturePython)
  AlwaysSyncPlacement = false
  Angle = 360
  ArrayType = 0
  Axis = (0,0,1)
  Base = -> Sketch005
  Center = (0,0,0)
  Count = 99
  ExpandArray = false
  Fuse = false
  IntervalAxis = (0,0,0)
  IntervalX = (2.12,0,0)
  IntervalY = (0,100,0)
  IntervalZ = (0,0,100)
  NumberCircles = 3
  NumberPolar = 5
  NumberX = 99
  NumberY = 1
  NumberZ = 1
  PlacementList = 99 placements: arithmetic series from (0,0,0) step (2.12,0,0) to (207.76,0,0)
  RadialDistance = 50
  ScaleList = (99) [(1,1,1),(1,1,1),(1,1,1),(1,1,1),(1,1,1),(1,1,1),(1,1,1),(1,1,1),(1,1,1),(1,1,1),(1,1,1),(1,1,1),(1,1,1),(1,1,1),(1,1,1),(1,1,1),(1,1,1),(1,1,1),+81 more]
  Symmetry = 1
  TangentialDistance = 25
FEATURE [Sketcher::SketchObject] Sketch006  label="fill "
  FullyConstrained = false
  sketch-geometry (631):
    g0: LineSegment StartX=-66.423 StartY=17.6018 StartZ=0 EndX=18.1002 EndY=-66.9214 EndZ=0
    g1: LineSegment StartX=-64.303 StartY=17.6018 StartZ=0 EndX=-10.3 EndY=-36.4012 EndZ=0
    g2: LineSegment StartX=-62.183 StartY=17.6018 StartZ=0 EndX=-10.3 EndY=-34.2812 EndZ=0
    g3: LineSegment StartX=-60.063 StartY=17.6018 StartZ=0 EndX=-9.88325 EndY=-32.578 EndZ=0
    g4: LineSegment StartX=-57.943 StartY=17.6018 StartZ=0 EndX=-8.52817 EndY=-31.8131 EndZ=0
    g5: LineSegment StartX=-55.823 StartY=17.6018 StartZ=0 EndX=-7.39452 EndY=-30.8267 EndZ=0
    g6: LineSegment StartX=-53.703 StartY=17.6018 StartZ=0 EndX=-6.30935 EndY=-29.7919 EndZ=0
    g7: LineSegment StartX=-51.583 StartY=17.6018 StartZ=0 EndX=-4.80363 EndY=-29.1776 EndZ=0
    g8: LineSegment StartX=-49.463 StartY=17.6018 StartZ=0 EndX=-2.76123 EndY=-29.1 EndZ=0
    g9: LineSegment StartX=-47.343 StartY=17.6018 StartZ=0 EndX=-0.641226 EndY=-29.1 EndZ=0
    g10: LineSegment StartX=-45.223 StartY=17.6018 StartZ=0 EndX=-10.3 EndY=-17.3212 EndZ=0
    g11: LineSegment StartX=-43.103 StartY=17.6018 StartZ=0 EndX=-10.3 EndY=-15.2012 EndZ=0
    g12: LineSegment StartX=-40.983 StartY=17.6018 StartZ=0 EndX=-9.84782 EndY=-13.5334 EndZ=0
    g13: LineSegment StartX=-38.863 StartY=17.6018 StartZ=0 EndX=-8.4552 EndY=-12.806 EndZ=0
    g14: LineSegment StartX=-36.743 StartY=17.6018 StartZ=0 EndX=-7.36053 EndY=-11.7807 EndZ=0
    g15: LineSegment StartX=-34.623 StartY=17.6018 StartZ=0 EndX=-6.26082 EndY=-10.7604 EndZ=0
    g16: LineSegment StartX=-32.503 StartY=17.6018 StartZ=0 EndX=-4.7362 EndY=-10.165 EndZ=0
    g17: LineSegment StartX=-30.383 StartY=17.6018 StartZ=0 EndX=-2.68123 EndY=-10.1 EndZ=0
    g18: LineSegment StartX=-28.263 StartY=17.6018 StartZ=0 EndX=-0.561226 EndY=-10.1 EndZ=0
    g19: LineSegment StartX=-26.143 StartY=17.6018 StartZ=0 EndX=-10.3 EndY=1.75877 EndZ=0
    g20: LineSegment StartX=-24.023 StartY=17.6018 StartZ=0 EndX=-10.3 EndY=3.87877 EndZ=0
    g21: LineSegment StartX=-21.903 StartY=17.6018 StartZ=0 EndX=-9.81124 EndY=5.51002 EndZ=0
    g22: LineSegment StartX=-19.783 StartY=17.6018 StartZ=0 EndX=-8.37964 EndY=6.19841 EndZ=0
    g23: LineSegment StartX=-17.663 StartY=17.6018 StartZ=0 EndX=-7.32597 EndY=7.26474 EndZ=0
    g24: LineSegment StartX=-15.543 StartY=17.6018 StartZ=0 EndX=-6.21171 EndY=8.27048 EndZ=0
    g25: LineSegment StartX=-13.423 StartY=17.6018 StartZ=0 EndX=-4.6678 EndY=8.84657 EndZ=0
    g26: LineSegment StartX=-11.303 StartY=17.6018 StartZ=0 EndX=-2.60123 EndY=8.9 EndZ=0
    g27: LineSegment StartX=-9.18299 StartY=17.6018 StartZ=0 EndX=-0.481226 EndY=8.9 EndZ=0
    g28: LineSegment StartX=-7.06299 StartY=17.6018 StartZ=0 EndX=1.63877 EndY=8.9 EndZ=0
    g29: LineSegment StartX=-4.94299 StartY=17.6018 StartZ=0 EndX=3.75877 EndY=8.9 EndZ=0
    g30: LineSegment StartX=-2.82299 StartY=17.6018 StartZ=0 EndX=5.87877 EndY=8.9 EndZ=0
    g31: LineSegment StartX=-0.702992 StartY=17.6018 StartZ=0 EndX=8.22612 EndY=8.67265 EndZ=0
    g32: LineSegment StartX=1.41701 StartY=17.6018 StartZ=0 EndX=11.7091 EndY=7.30964 EndZ=0
    g33: LineSegment StartX=3.53701 StartY=17.6018 StartZ=0 EndX=12.838 EndY=8.30079 EndZ=0
    g34: LineSegment StartX=5.65701 StartY=17.6018 StartZ=0 EndX=14.4016 EndY=8.85716 EndZ=0
    g35: LineSegment StartX=7.77701 StartY=17.6018 StartZ=0 EndX=16.4788 EndY=8.9 EndZ=0
    g36: LineSegment StartX=9.89701 StartY=17.6018 StartZ=0 EndX=18.5988 EndY=8.9 EndZ=0
    g37: LineSegment StartX=12.017 StartY=17.6018 StartZ=0 EndX=20.7188 EndY=8.9 EndZ=0
    g38: LineSegment StartX=14.137 StartY=17.6018 StartZ=0 EndX=22.8388 EndY=8.9 EndZ=0
    g39: LineSegment StartX=16.257 StartY=17.6018 StartZ=0 EndX=24.9588 EndY=8.9 EndZ=0
    g40: LineSegment StartX=18.377 StartY=17.6018 StartZ=0 EndX=27.4256 EndY=8.55321 EndZ=0
    g41: LineSegment StartX=20.497 StartY=17.6018 StartZ=0 EndX=28.0175 EndY=10.0813 EndZ=0
    g42: LineSegment StartX=22.617 StartY=17.6018 StartZ=0 EndX=29.2664 EndY=10.9524 EndZ=0
    g43: LineSegment StartX=24.737 StartY=17.6018 StartZ=0 EndX=30.5068 EndY=11.8319 EndZ=0
    g44: LineSegment StartX=26.857 StartY=17.6018 StartZ=0 EndX=31.5485 EndY=12.9103 EndZ=0
    g45: LineSegment StartX=28.977 StartY=17.6018 StartZ=0 EndX=32.9996 EndY=13.5791 EndZ=0
    g46: LineSegment StartX=31.097 StartY=17.6018 StartZ=0 EndX=34.9988 EndY=13.7 EndZ=0
    g47: LineSegment StartX=33.217 StartY=17.6018 StartZ=0 EndX=37.1188 EndY=13.7 EndZ=0
    g48: LineSegment StartX=35.337 StartY=17.6018 StartZ=0 EndX=39.2388 EndY=13.7 EndZ=0
    g49: LineSegment StartX=37.457 StartY=17.6018 StartZ=0 EndX=41.3588 EndY=13.7 EndZ=0
    g50: LineSegment StartX=39.577 StartY=17.6018 StartZ=0 EndX=43.4788 EndY=13.7 EndZ=0
    g51: LineSegment StartX=41.697 StartY=17.6018 StartZ=0 EndX=45.6254 EndY=13.6733 EndZ=0
    g52: LineSegment StartX=43.817 StartY=17.6018 StartZ=0 EndX=48.2664 EndY=13.1524 EndZ=0
    g53: LineSegment StartX=45.937 StartY=17.6018 StartZ=0 EndX=49.5068 EndY=14.0319 EndZ=0
    g54: LineSegment StartX=48.057 StartY=17.6018 StartZ=0 EndX=50.5485 EndY=15.1103 EndZ=0
    g55: LineSegment StartX=50.177 StartY=17.6018 StartZ=0 EndX=51.9996 EndY=15.7791 EndZ=0
    g56: LineSegment StartX=52.297 StartY=17.6018 StartZ=0 EndX=53.9988 EndY=15.9 EndZ=0
    g57: LineSegment StartX=54.417 StartY=17.6018 StartZ=0 EndX=56.1188 EndY=15.9 EndZ=0
    g58: LineSegment StartX=56.537 StartY=17.6018 StartZ=0 EndX=58.2388 EndY=15.9 EndZ=0
    g59: LineSegment StartX=58.657 StartY=17.6018 StartZ=0 EndX=60.3588 EndY=15.9 EndZ=0
    g60: LineSegment StartX=60.777 StartY=17.6018 StartZ=0 EndX=62.4788 EndY=15.9 EndZ=0
    g61: LineSegment StartX=62.897 StartY=17.6018 StartZ=0 EndX=64.6254 EndY=15.8733 EndZ=0
    g62: LineSegment StartX=65.017 StartY=17.6018 StartZ=0 EndX=69.6427 EndY=12.9761 EndZ=0
    g63: LineSegment StartX=67.137 StartY=17.6018 StartZ=0 EndX=71.1299 EndY=13.6089 EndZ=0
    g64: LineSegment StartX=69.257 StartY=17.6018 StartZ=0 EndX=73.1588 EndY=13.7 EndZ=0
    g65: LineSegment StartX=71.377 StartY=17.6018 StartZ=0 EndX=75.2788 EndY=13.7 EndZ=0
    g66: LineSegment StartX=73.497 StartY=17.6018 StartZ=0 EndX=77.3988 EndY=13.7 EndZ=0
    g67: LineSegment StartX=75.617 StartY=17.6018 StartZ=0 EndX=79.5188 EndY=13.7 EndZ=0
    g68: LineSegment StartX=77.737 StartY=17.6018 StartZ=0 EndX=81.6388 EndY=13.7 EndZ=0
    g69: LineSegment StartX=79.857 StartY=17.6018 StartZ=0 EndX=83.8304 EndY=13.6284 EndZ=0
    g70: LineSegment StartX=81.977 StartY=17.6018 StartZ=0 EndX=88.7392 EndY=10.8396 EndZ=0
    g71: LineSegment StartX=84.097 StartY=17.6018 StartZ=0 EndX=90.2638 EndY=11.435 EndZ=0
    g72: LineSegment StartX=86.217 StartY=17.6018 StartZ=0 EndX=92.3188 EndY=11.5 EndZ=0
    g73: LineSegment StartX=88.337 StartY=17.6018 StartZ=0 EndX=94.4388 EndY=11.5 EndZ=0
    g74: LineSegment StartX=90.457 StartY=17.6018 StartZ=0 EndX=96.5588 EndY=11.5 EndZ=0
    g75: LineSegment StartX=92.577 StartY=17.6018 StartZ=0 EndX=98.6788 EndY=11.5 EndZ=0
    g76: LineSegment StartX=94.697 StartY=17.6018 StartZ=0 EndX=100.799 EndY=11.5 EndZ=0
    g77: LineSegment StartX=96.817 StartY=17.6018 StartZ=0 EndX=103.075 EndY=11.3437 EndZ=0
    g78: LineSegment StartX=98.937 StartY=17.6018 StartZ=0 EndX=183.46 EndY=-66.9214 EndZ=0
    g79: LineSegment StartX=101.057 StartY=17.6018 StartZ=0 EndX=185.58 EndY=-66.9214 EndZ=0
    g80: LineSegment StartX=103.177 StartY=17.6018 StartZ=0 EndX=187.7 EndY=-66.9214 EndZ=0
    g81: LineSegment StartX=105.297 StartY=17.6018 StartZ=0 EndX=189.82 EndY=-66.9214 EndZ=0
    g82: LineSegment StartX=107.417 StartY=17.6018 StartZ=0 EndX=191.94 EndY=-66.9214 EndZ=0
    g83: LineSegment StartX=109.537 StartY=17.6018 StartZ=0 EndX=194.06 EndY=-66.9214 EndZ=0
    g84: LineSegment StartX=111.657 StartY=17.6018 StartZ=0 EndX=196.18 EndY=-66.9214 EndZ=0
    g85: LineSegment StartX=113.777 StartY=17.6018 StartZ=0 EndX=198.3 EndY=-66.9214 EndZ=0
    g86: LineSegment StartX=115.897 StartY=17.6018 StartZ=0 EndX=200.42 EndY=-66.9214 EndZ=0
    g87: LineSegment StartX=118.017 StartY=17.6018 StartZ=0 EndX=202.54 EndY=-66.9214 EndZ=0
    g88: LineSegment StartX=120.137 StartY=17.6018 StartZ=0 EndX=204.66 EndY=-66.9214 EndZ=0
    g89: LineSegment StartX=122.257 StartY=17.6018 StartZ=0 EndX=206.78 EndY=-66.9214 EndZ=0
    g90: LineSegment StartX=124.377 StartY=17.6018 StartZ=0 EndX=208.9 EndY=-66.9214 EndZ=0
    g91: LineSegment StartX=126.497 StartY=17.6018 StartZ=0 EndX=211.02 EndY=-66.9214 EndZ=0
    g92: LineSegment StartX=128.617 StartY=17.6018 StartZ=0 EndX=213.14 EndY=-66.9214 EndZ=0
    g93: LineSegment StartX=130.737 StartY=17.6018 StartZ=0 EndX=215.26 EndY=-66.9214 EndZ=0
    g94: LineSegment StartX=132.857 StartY=17.6018 StartZ=0 EndX=217.38 EndY=-66.9214 EndZ=0
    g95: LineSegment StartX=134.977 StartY=17.6018 StartZ=0 EndX=219.5 EndY=-66.9214 EndZ=0
    g96: LineSegment StartX=137.097 StartY=17.6018 StartZ=0 EndX=221.62 EndY=-66.9214 EndZ=0
    g97: LineSegment StartX=139.217 StartY=17.6018 StartZ=0 EndX=223.74 EndY=-66.9214 EndZ=0
    g98: LineSegment StartX=141.337 StartY=17.6018 StartZ=0 EndX=225.86 EndY=-66.9214 EndZ=0
    g99: ArcOfCircle CenterX=-5 CenterY=0 CenterZ=0 NormalX=0 NormalY=0 NormalZ=1 AngleXU=0 Radius=3.2 StartAngle=3.52599 EndAngle=4.71239
    g100: LineSegment StartX=-5 StartY=-3.2 StartZ=0 EndX=-2.72029 EndY=-3.2 EndZ=0
    g101: ArcOfCircle CenterX=0 CenterY=0 CenterZ=0 NormalX=0 NormalY=0 NormalZ=1 AngleXU=0 Radius=4.2 StartAngle=4.00784 EndAngle=5.41694
    g102: LineSegment StartX=2.72029 StartY=-3.2 StartZ=0 EndX=4.75857 EndY=-3.2 EndZ=0
    g103: ArcOfCircle CenterX=6.65 CenterY=-2.55 CenterZ=0 NormalX=0 NormalY=0 NormalZ=1 AngleXU=0 Radius=2 StartAngle=3.4726 EndAngle=4.71239
    g104: LineSegment StartX=9 StartY=-4.55 StartZ=0 EndX=6.65 EndY=-4.55 EndZ=0
    g105: ArcOfCircle CenterX=9 CenterY=-2.55 CenterZ=0 NormalX=0 NormalY=0 NormalZ=1 AngleXU=0 Radius=2 StartAngle=4.71239 EndAngle=6.28319
    g106: LineSegment StartX=11 StartY=-1.2 StartZ=0 EndX=11 EndY=-2.55 EndZ=0
    g107: LineSegment StartX=9.3 StartY=6.9 StartZ=0 EndX=9.3 EndY=5.62829 EndZ=0
    g108: ArcOfCircle CenterX=7.3 CenterY=6.9 CenterZ=0 NormalX=0 NormalY=0 NormalZ=1 AngleXU=0 Radius=2 StartAngle=4e-16 EndAngle=1.5708
    g109: LineSegment StartX=-4 StartY=8.9 StartZ=0 EndX=7.3 EndY=8.9 EndZ=0
    g110: ArcOfCircle CenterX=-4 CenterY=4.7 CenterZ=0 NormalX=0 NormalY=0 NormalZ=1 AngleXU=0 Radius=4.2 StartAngle=1.5708 EndAngle=2.77639
    g111: LineSegment StartX=-8.3 StartY=6.2 StartZ=0 EndX=-7.92301 EndY=6.2 EndZ=0
    g112: ArcOfCircle CenterX=-8.3 CenterY=4.2 CenterZ=0 NormalX=0 NormalY=0 NormalZ=1 AngleXU=0 Radius=2 StartAngle=1.5708 EndAngle=3.14159
    g113: LineSegment StartX=-10.3 StartY=0.8 StartZ=0 EndX=-10.3 EndY=4.2 EndZ=0
    g114: ArcOfCircle CenterX=-8.3 CenterY=0.8 CenterZ=0 NormalX=0 NormalY=0 NormalZ=1 AngleXU=0 Radius=2 StartAngle=3.14159 EndAngle=4.71239
    g115: LineSegment StartX=-8.3 StartY=-1.2 StartZ=0 EndX=-7.96648 EndY=-1.2 EndZ=0
    g116: ArcOfCircle CenterX=-5 CenterY=-19 CenterZ=0 NormalX=0 NormalY=0 NormalZ=1 AngleXU=0 Radius=3.2 StartAngle=3.52599 EndAngle=4.71239
    g117: LineSegment StartX=-5 StartY=-22.2 StartZ=0 EndX=-2.72029 EndY=-22.2 EndZ=0
    g118: ArcOfCircle CenterX=0 CenterY=-19 CenterZ=0 NormalX=0 NormalY=0 NormalZ=1 AngleXU=0 Radius=4.2 StartAngle=4.00784 EndAngle=5.41694
    g119: LineSegment StartX=2.72029 StartY=-22.2 StartZ=0 EndX=4.75857 EndY=-22.2 EndZ=0
    g120: ArcOfCircle CenterX=6.65 CenterY=-21.55 CenterZ=0 NormalX=0 NormalY=0 NormalZ=1 AngleXU=0 Radius=2 StartAngle=3.4726 EndAngle=4.71239
    g121: LineSegment StartX=9 StartY=-23.55 StartZ=0 EndX=6.65 EndY=-23.55 EndZ=0
    g122: ArcOfCircle CenterX=9 CenterY=-21.55 CenterZ=0 NormalX=0 NormalY=0 NormalZ=1 AngleXU=0 Radius=2 StartAngle=4.71239 EndAngle=6.28319
    g123: LineSegment StartX=11 StartY=-20.2 StartZ=0 EndX=11 EndY=-21.55 EndZ=0
    g124: LineSegment StartX=9.3 StartY=-12.1 StartZ=0 EndX=9.3 EndY=-13.3717 EndZ=0
    g125: ArcOfCircle CenterX=7.3 CenterY=-12.1 CenterZ=0 NormalX=0 NormalY=0 NormalZ=1 AngleXU=0 Radius=2 StartAngle=4e-16 EndAngle=1.5708
    g126: LineSegment StartX=-4 StartY=-10.1 StartZ=0 EndX=7.3 EndY=-10.1 EndZ=0
    g127: ArcOfCircle CenterX=-4 CenterY=-14.3 CenterZ=0 NormalX=0 NormalY=0 NormalZ=1 AngleXU=0 Radius=4.2 StartAngle=1.5708 EndAngle=2.77639
    g128: LineSegment StartX=-8.3 StartY=-12.8 StartZ=0 EndX=-7.92301 EndY=-12.8 EndZ=0
    g129: ArcOfCircle CenterX=-8.3 CenterY=-14.8 CenterZ=0 NormalX=0 NormalY=0 NormalZ=1 AngleXU=0 Radius=2 StartAngle=1.5708 EndAngle=3.14159
    g130: LineSegment StartX=-10.3 StartY=-18.2 StartZ=0 EndX=-10.3 EndY=-14.8 EndZ=0
    g131: ArcOfCircle CenterX=-8.3 CenterY=-18.2 CenterZ=0 NormalX=0 NormalY=0 NormalZ=1 AngleXU=0 Radius=2 StartAngle=3.14159 EndAngle=4.71239
    g132: LineSegment StartX=-8.3 StartY=-20.2 StartZ=0 EndX=-7.96648 EndY=-20.2 EndZ=0
    g133: ArcOfCircle CenterX=-5 CenterY=-38 CenterZ=0 NormalX=0 NormalY=0 NormalZ=1 AngleXU=0 Radius=3.2 StartAngle=3.52599 EndAngle=4.71239
    g134: LineSegment StartX=-5 StartY=-41.2 StartZ=0 EndX=-2.72029 EndY=-41.2 EndZ=0
    g135: ArcOfCircle CenterX=0 CenterY=-38 CenterZ=0 NormalX=0 NormalY=0 NormalZ=1 AngleXU=0 Radius=4.2 StartAngle=4.00784 EndAngle=5.41694
    g136: LineSegment StartX=2.72029 StartY=-41.2 StartZ=0 EndX=4.75857 EndY=-41.2 EndZ=0
    g137: ArcOfCircle CenterX=6.65 CenterY=-40.55 CenterZ=0 NormalX=0 NormalY=0 NormalZ=1 AngleXU=0 Radius=2 StartAngle=3.4726 EndAngle=4.71239
    g138: LineSegment StartX=9 StartY=-42.55 StartZ=0 EndX=6.65 EndY=-42.55 EndZ=0
    g139: ArcOfCircle CenterX=9 CenterY=-40.55 CenterZ=0 NormalX=0 NormalY=0 NormalZ=1 AngleXU=0 Radius=2 StartAngle=4.71239 EndAngle=6.28319
    g140: LineSegment StartX=11 StartY=-39.2 StartZ=0 EndX=11 EndY=-40.55 EndZ=0
    g141: LineSegment StartX=9.3 StartY=-31.1 StartZ=0 EndX=9.3 EndY=-32.3717 EndZ=0
    g142: ArcOfCircle CenterX=7.3 CenterY=-31.1 CenterZ=0 NormalX=0 NormalY=0 NormalZ=1 AngleXU=0 Radius=2 StartAngle=4e-16 EndAngle=1.5708
    g143: LineSegment StartX=-4 StartY=-29.1 StartZ=0 EndX=7.3 EndY=-29.1 EndZ=0
    g144: ArcOfCircle CenterX=-4 CenterY=-33.3 CenterZ=0 NormalX=0 NormalY=0 NormalZ=1 AngleXU=0 Radius=4.2 StartAngle=1.5708 EndAngle=2.77639
    g145: LineSegment StartX=-8.3 StartY=-31.8 StartZ=0 EndX=-7.92301 EndY=-31.8 EndZ=0
    g146: ArcOfCircle CenterX=-8.3 CenterY=-33.8 CenterZ=0 NormalX=0 NormalY=0 NormalZ=1 AngleXU=0 Radius=2 StartAngle=1.5708 EndAngle=3.14159
    g147: LineSegment StartX=-10.3 StartY=-37.2 StartZ=0 EndX=-10.3 EndY=-33.8 EndZ=0
    g148: ArcOfCircle CenterX=-8.3 CenterY=-37.2 CenterZ=0 NormalX=0 NormalY=0 NormalZ=1 AngleXU=0 Radius=2 StartAngle=3.14159 EndAngle=4.71239
    g149: LineSegment StartX=-8.3 StartY=-39.2 StartZ=0 EndX=-7.96648 EndY=-39.2 EndZ=0
    g150: ArcOfCircle CenterX=14 CenterY=-38 CenterZ=0 NormalX=0 NormalY=0 NormalZ=1 AngleXU=0 Radius=3.2 StartAngle=3.52599 EndAngle=4.71239
    g151: LineSegment StartX=14 StartY=-41.2 StartZ=0 EndX=16.2797 EndY=-41.2 EndZ=0
    g152: ArcOfCircle CenterX=19 CenterY=-38 CenterZ=0 NormalX=0 NormalY=0 NormalZ=1 AngleXU=0 Radius=4.2 StartAngle=4.00784 EndAngle=5.41694
    g153: LineSegment StartX=21.7203 StartY=-41.2 StartZ=0 EndX=23.7586 EndY=-41.2 EndZ=0
    g154: ArcOfCircle CenterX=25.65 CenterY=-40.55 CenterZ=0 NormalX=0 NormalY=0 NormalZ=1 AngleXU=0 Radius=2 StartAngle=3.4726 EndAngle=4.71239
    g155: LineSegment StartX=28 StartY=-42.55 StartZ=0 EndX=25.65 EndY=-42.55 EndZ=0
    g156: ArcOfCircle CenterX=28 CenterY=-40.55 CenterZ=0 NormalX=0 NormalY=0 NormalZ=1 AngleXU=0 Radius=2 StartAngle=4.71239 EndAngle=6.28319
    g157: LineSegment StartX=30 StartY=-35.45 StartZ=0 EndX=30 EndY=-40.55 EndZ=0
    g158: ArcOfCircle CenterX=28 CenterY=-35.45 CenterZ=0 NormalX=0 NormalY=0 NormalZ=1 AngleXU=0 Radius=2 StartAngle=0 EndAngle=0.552715
    g159: ArcOfCircle CenterX=26.3 CenterY=-31.1 CenterZ=0 NormalX=0 NormalY=0 NormalZ=1 AngleXU=0 Radius=2 StartAngle=0.795399 EndAngle=1.5708
    g160: LineSegment StartX=15 StartY=-29.1 StartZ=0 EndX=26.3 EndY=-29.1 EndZ=0
    g161: ArcOfCircle CenterX=15 CenterY=-33.3 CenterZ=0 NormalX=0 NormalY=0 NormalZ=1 AngleXU=0 Radius=4.2 StartAngle=1.5708 EndAngle=2.77639
    g162: LineSegment StartX=10.7 StartY=-31.8 StartZ=0 EndX=11.077 EndY=-31.8 EndZ=0
    g163: ArcOfCircle CenterX=10.7 CenterY=-33.8 CenterZ=0 NormalX=0 NormalY=0 NormalZ=1 AngleXU=0 Radius=2 StartAngle=1.5708 EndAngle=2.34619
    g164: LineSegment StartX=11 StartY=-39.2 StartZ=0 EndX=11.0335 EndY=-39.2 EndZ=0
    g165: ArcOfCircle CenterX=14 CenterY=-19 CenterZ=0 NormalX=0 NormalY=0 NormalZ=1 AngleXU=0 Radius=3.2 StartAngle=3.52599 EndAngle=4.71239
    g166: LineSegment StartX=14 StartY=-22.2 StartZ=0 EndX=16.2797 EndY=-22.2 EndZ=0
    g167: ArcOfCircle CenterX=19 CenterY=-19 CenterZ=0 NormalX=0 NormalY=0 NormalZ=1 AngleXU=0 Radius=4.2 StartAngle=4.00784 EndAngle=5.41694
    g168: LineSegment StartX=21.7203 StartY=-22.2 StartZ=0 EndX=23.7586 EndY=-22.2 EndZ=0
    g169: ArcOfCircle CenterX=25.65 CenterY=-21.55 CenterZ=0 NormalX=0 NormalY=0 NormalZ=1 AngleXU=0 Radius=2 StartAngle=3.4726 EndAngle=4.71239
    g170: LineSegment StartX=28 StartY=-23.55 StartZ=0 EndX=25.65 EndY=-23.55 EndZ=0
    g171: ArcOfCircle CenterX=28 CenterY=-21.55 CenterZ=0 NormalX=0 NormalY=0 NormalZ=1 AngleXU=0 Radius=2 StartAngle=4.71239 EndAngle=6.28319
    g172: LineSegment StartX=30 StartY=-16.45 StartZ=0 EndX=30 EndY=-21.55 EndZ=0
    g173: ArcOfCircle CenterX=28 CenterY=-16.45 CenterZ=0 NormalX=0 NormalY=0 NormalZ=1 AngleXU=0 Radius=2 StartAngle=0 EndAngle=0.552715
    g174: ArcOfCircle CenterX=26.3 CenterY=-12.1 CenterZ=0 NormalX=0 NormalY=0 NormalZ=1 AngleXU=0 Radius=2 StartAngle=0.795399 EndAngle=1.5708
    g175: LineSegment StartX=15 StartY=-10.1 StartZ=0 EndX=26.3 EndY=-10.1 EndZ=0
    g176: ArcOfCircle CenterX=15 CenterY=-14.3 CenterZ=0 NormalX=0 NormalY=0 NormalZ=1 AngleXU=0 Radius=4.2 StartAngle=1.5708 EndAngle=2.77639
    g177: LineSegment StartX=10.7 StartY=-12.8 StartZ=0 EndX=11.077 EndY=-12.8 EndZ=0
    g178: ArcOfCircle CenterX=10.7 CenterY=-14.8 CenterZ=0 NormalX=0 NormalY=0 NormalZ=1 AngleXU=0 Radius=2 StartAngle=1.5708 EndAngle=2.34619
    g179: LineSegment StartX=11 StartY=-20.2 StartZ=0 EndX=11.0335 EndY=-20.2 EndZ=0
    g180: ArcOfCircle CenterX=14 CenterY=0 CenterZ=0 NormalX=0 NormalY=0 NormalZ=1 AngleXU=0 Radius=3.2 StartAngle=3.52599 EndAngle=4.71239
    g181: LineSegment StartX=14 StartY=-3.2 StartZ=0 EndX=16.2797 EndY=-3.2 EndZ=0
    g182: ArcOfCircle CenterX=19 CenterY=0 CenterZ=0 NormalX=0 NormalY=0 NormalZ=1 AngleXU=0 Radius=4.2 StartAngle=4.00784 EndAngle=5.41694
    g183: LineSegment StartX=21.7203 StartY=-3.2 StartZ=0 EndX=23.7586 EndY=-3.2 EndZ=0
    g184: ArcOfCircle CenterX=25.65 CenterY=-2.55 CenterZ=0 NormalX=0 NormalY=0 NormalZ=1 AngleXU=0 Radius=2 StartAngle=3.4726 EndAngle=4.71239
    g185: LineSegment StartX=28 StartY=-4.55 StartZ=0 EndX=25.65 EndY=-4.55 EndZ=0
    g186: ArcOfCircle CenterX=28 CenterY=-2.55 CenterZ=0 NormalX=0 NormalY=0 NormalZ=1 AngleXU=0 Radius=2 StartAngle=4.71239 EndAngle=6.28319
    g187: LineSegment StartX=30 StartY=2.55 StartZ=0 EndX=30 EndY=-2.55 EndZ=0
    g188: ArcOfCircle CenterX=28 CenterY=2.55 CenterZ=0 NormalX=0 NormalY=0 NormalZ=1 AngleXU=0 Radius=2 StartAngle=0 EndAngle=0.552715
    g189: ArcOfCircle CenterX=26.3 CenterY=6.9 CenterZ=0 NormalX=0 NormalY=0 NormalZ=1 AngleXU=0 Radius=2 StartAngle=0.795399 EndAngle=1.5708
    g190: LineSegment StartX=15 StartY=8.9 StartZ=0 EndX=26.3 EndY=8.9 EndZ=0
    g191: ArcOfCircle CenterX=15 CenterY=4.7 CenterZ=0 NormalX=0 NormalY=0 NormalZ=1 AngleXU=0 Radius=4.2 StartAngle=1.5708 EndAngle=2.77639
    g192: LineSegment StartX=10.7 StartY=6.2 StartZ=0 EndX=11.077 EndY=6.2 EndZ=0
    g193: ArcOfCircle CenterX=10.7 CenterY=4.2 CenterZ=0 NormalX=0 NormalY=0 NormalZ=1 AngleXU=0 Radius=2 StartAngle=1.5708 EndAngle=2.34619
    g194: LineSegment StartX=11 StartY=-1.2 StartZ=0 EndX=11.0335 EndY=-1.2 EndZ=0
    g195: ArcOfCircle CenterX=33 CenterY=4.8 CenterZ=0 NormalX=0 NormalY=0 NormalZ=1 AngleXU=0 Radius=3.2 StartAngle=3.52599 EndAngle=4.71239
    g196: LineSegment StartX=33 StartY=1.6 StartZ=0 EndX=35.2797 EndY=1.6 EndZ=0
    g197: ArcOfCircle CenterX=38 CenterY=4.8 CenterZ=0 NormalX=0 NormalY=0 NormalZ=1 AngleXU=0 Radius=4.2 StartAngle=4.00784 EndAngle=5.41694
    g198: LineSegment StartX=40.7203 StartY=1.6 StartZ=0 EndX=42.7586 EndY=1.6 EndZ=0
    g199: ArcOfCircle CenterX=44.65 CenterY=2.25 CenterZ=0 NormalX=0 NormalY=0 NormalZ=1 AngleXU=0 Radius=2 StartAngle=3.4726 EndAngle=4.71239
    g200: LineSegment StartX=47 StartY=0.25 StartZ=0 EndX=44.65 EndY=0.25 EndZ=0
    g201: ArcOfCircle CenterX=47 CenterY=2.25 CenterZ=0 NormalX=0 NormalY=0 NormalZ=1 AngleXU=0 Radius=2 StartAngle=4.71239 EndAngle=6.28319
    g202: LineSegment StartX=49 StartY=5.8 StartZ=0 EndX=49 EndY=2.25 EndZ=0
    g203: ArcOfCircle CenterX=45.3 CenterY=11.7 CenterZ=0 NormalX=0 NormalY=0 NormalZ=1 AngleXU=0 Radius=2 StartAngle=0.391193 EndAngle=1.5708
    g204: LineSegment StartX=34 StartY=13.7 StartZ=0 EndX=45.3 EndY=13.7 EndZ=0
    g205: ArcOfCircle CenterX=34 CenterY=9.5 CenterZ=0 NormalX=0 NormalY=0 NormalZ=1 AngleXU=0 Radius=4.2 StartAngle=1.5708 EndAngle=2.77639
    g206: LineSegment StartX=29.7 StartY=11 StartZ=0 EndX=30.077 EndY=11 EndZ=0
    g207: ArcOfCircle CenterX=29.7 CenterY=9 CenterZ=0 NormalX=0 NormalY=0 NormalZ=1 AngleXU=0 Radius=2 StartAngle=1.5708 EndAngle=3.14159
    g208: LineSegment StartX=27.7 StartY=8.32829 StartZ=0 EndX=27.7 EndY=9 EndZ=0
    g209: LineSegment StartX=29.7 StartY=3.6 StartZ=0 EndX=30.0335 EndY=3.6 EndZ=0
    g210: ArcOfCircle CenterX=33 CenterY=-14.2 CenterZ=0 NormalX=0 NormalY=0 NormalZ=1 AngleXU=0 Radius=3.2 StartAngle=3.52599 EndAngle=4.71239
    g211: LineSegment StartX=33 StartY=-17.4 StartZ=0 EndX=35.2797 EndY=-17.4 EndZ=0
    g212: ArcOfCircle CenterX=38 CenterY=-14.2 CenterZ=0 NormalX=0 NormalY=0 NormalZ=1 AngleXU=0 Radius=4.2 StartAngle=4.00784 EndAngle=5.41694
    g213: LineSegment StartX=40.7203 StartY=-17.4 StartZ=0 EndX=42.7586 EndY=-17.4 EndZ=0
    g214: ArcOfCircle CenterX=44.65 CenterY=-16.75 CenterZ=0 NormalX=0 NormalY=0 NormalZ=1 AngleXU=0 Radius=2 StartAngle=3.4726 EndAngle=4.71239
    g215: LineSegment StartX=47 StartY=-18.75 StartZ=0 EndX=44.65 EndY=-18.75 EndZ=0
    g216: ArcOfCircle CenterX=47 CenterY=-16.75 CenterZ=0 NormalX=0 NormalY=0 NormalZ=1 AngleXU=0 Radius=2 StartAngle=4.71239 EndAngle=6.28319
    g217: LineSegment StartX=49 StartY=-13.2 StartZ=0 EndX=49 EndY=-16.75 EndZ=0
    g218: ArcOfCircle CenterX=45.3 CenterY=-7.3 CenterZ=0 NormalX=0 NormalY=0 NormalZ=1 AngleXU=0 Radius=2 StartAngle=0.391193 EndAngle=1.5708
    g219: LineSegment StartX=34 StartY=-5.3 StartZ=0 EndX=45.3 EndY=-5.3 EndZ=0
    g220: ArcOfCircle CenterX=34 CenterY=-9.5 CenterZ=0 NormalX=0 NormalY=0 NormalZ=1 AngleXU=0 Radius=4.2 StartAngle=1.5708 EndAngle=2.77639
    g221: LineSegment StartX=29.7 StartY=-8 StartZ=0 EndX=30.077 EndY=-8 EndZ=0
    g222: ArcOfCircle CenterX=29.7 CenterY=-10 CenterZ=0 NormalX=0 NormalY=0 NormalZ=1 AngleXU=0 Radius=2 StartAngle=1.5708 EndAngle=3.14159
    g223: LineSegment StartX=27.7 StartY=-10.6717 StartZ=0 EndX=27.7 EndY=-10 EndZ=0
    g224: LineSegment StartX=29.7 StartY=-15.4 StartZ=0 EndX=30.0335 EndY=-15.4 EndZ=0
    g225: ArcOfCircle CenterX=33 CenterY=-33.2 CenterZ=0 NormalX=0 NormalY=0 NormalZ=1 AngleXU=0 Radius=3.2 StartAngle=3.52599 EndAngle=4.71239
    g226: LineSegment StartX=33 StartY=-36.4 StartZ=0 EndX=35.2797 EndY=-36.4 EndZ=0
    g227: ArcOfCircle CenterX=38 CenterY=-33.2 CenterZ=0 NormalX=0 NormalY=0 NormalZ=1 AngleXU=0 Radius=4.2 StartAngle=4.00784 EndAngle=5.41694
    g228: LineSegment StartX=40.7203 StartY=-36.4 StartZ=0 EndX=42.7586 EndY=-36.4 EndZ=0
    g229: ArcOfCircle CenterX=44.65 CenterY=-35.75 CenterZ=0 NormalX=0 NormalY=0 NormalZ=1 AngleXU=0 Radius=2 StartAngle=3.4726 EndAngle=4.71239
    g230: LineSegment StartX=47 StartY=-37.75 StartZ=0 EndX=44.65 EndY=-37.75 EndZ=0
    g231: ArcOfCircle CenterX=47 CenterY=-35.75 CenterZ=0 NormalX=0 NormalY=0 NormalZ=1 AngleXU=0 Radius=2 StartAngle=4.71239 EndAngle=6.28319
    g232: LineSegment StartX=49 StartY=-32.2 StartZ=0 EndX=49 EndY=-35.75 EndZ=0
    g233: ArcOfCircle CenterX=45.3 CenterY=-26.3 CenterZ=0 NormalX=0 NormalY=0 NormalZ=1 AngleXU=0 Radius=2 StartAngle=0.391193 EndAngle=1.5708
    g234: LineSegment StartX=34 StartY=-24.3 StartZ=0 EndX=45.3 EndY=-24.3 EndZ=0
    g235: ArcOfCircle CenterX=34 CenterY=-28.5 CenterZ=0 NormalX=0 NormalY=0 NormalZ=1 AngleXU=0 Radius=4.2 StartAngle=1.5708 EndAngle=2.77639
    g236: LineSegment StartX=29.7 StartY=-27 StartZ=0 EndX=30.077 EndY=-27 EndZ=0
    g237: ArcOfCircle CenterX=29.7 CenterY=-29 CenterZ=0 NormalX=0 NormalY=0 NormalZ=1 AngleXU=0 Radius=2 StartAngle=1.5708 EndAngle=3.14159
    g238: LineSegment StartX=27.7 StartY=-29.6717 StartZ=0 EndX=27.7 EndY=-29 EndZ=0
    g239: LineSegment StartX=29.7 StartY=-34.4 StartZ=0 EndX=30.0335 EndY=-34.4 EndZ=0
    g240: ArcOfCircle CenterX=42 CenterY=-52.4 CenterZ=0 NormalX=0 NormalY=0 NormalZ=1 AngleXU=0 Radius=3.2 StartAngle=3.52599 EndAngle=4.71239
    g241: LineSegment StartX=42 StartY=-55.6 StartZ=0 EndX=44.2797 EndY=-55.6 EndZ=0
    g242: ArcOfCircle CenterX=47 CenterY=-52.4 CenterZ=0 NormalX=0 NormalY=0 NormalZ=1 AngleXU=0 Radius=4.2 StartAngle=4.00784 EndAngle=5.41694
    g243: LineSegment StartX=49.7203 StartY=-55.6 StartZ=0 EndX=51.7586 EndY=-55.6 EndZ=0
    g244: ArcOfCircle CenterX=53.65 CenterY=-54.95 CenterZ=0 NormalX=0 NormalY=0 NormalZ=1 AngleXU=0 Radius=2 StartAngle=3.4726 EndAngle=4.71239
    g245: LineSegment StartX=56 StartY=-56.95 StartZ=0 EndX=53.65 EndY=-56.95 EndZ=0
    g246: ArcOfCircle CenterX=56 CenterY=-54.95 CenterZ=0 NormalX=0 NormalY=0 NormalZ=1 AngleXU=0 Radius=2 StartAngle=4.71239 EndAngle=6.28319
    g247: LineSegment StartX=58 StartY=-53.6 StartZ=0 EndX=58 EndY=-54.95 EndZ=0
    g248: LineSegment StartX=56.3 StartY=-45.5 StartZ=0 EndX=56.3 EndY=-46.7717 EndZ=0
    g249: ArcOfCircle CenterX=54.3 CenterY=-45.5 CenterZ=0 NormalX=0 NormalY=0 NormalZ=1 AngleXU=0 Radius=2 StartAngle=4e-16 EndAngle=1.5708
    g250: LineSegment StartX=43 StartY=-43.5 StartZ=0 EndX=54.3 EndY=-43.5 EndZ=0
    g251: ArcOfCircle CenterX=43 CenterY=-47.7 CenterZ=0 NormalX=0 NormalY=0 NormalZ=1 AngleXU=0 Radius=4.2 StartAngle=1.5708 EndAngle=2.77639
    g252: LineSegment StartX=38.7 StartY=-46.2 StartZ=0 EndX=39.077 EndY=-46.2 EndZ=0
    g253: ArcOfCircle CenterX=38.7 CenterY=-48.2 CenterZ=0 NormalX=0 NormalY=0 NormalZ=1 AngleXU=0 Radius=2 StartAngle=1.5708 EndAngle=3.14159
    g254: LineSegment StartX=36.7 StartY=-51.6 StartZ=0 EndX=36.7 EndY=-48.2 EndZ=0
    g255: ArcOfCircle CenterX=38.7 CenterY=-51.6 CenterZ=0 NormalX=0 NormalY=0 NormalZ=1 AngleXU=0 Radius=2 StartAngle=3.14159 EndAngle=4.71239
    g256: LineSegment StartX=38.7 StartY=-53.6 StartZ=0 EndX=39.0335 EndY=-53.6 EndZ=0
    g257: ArcOfCircle CenterX=61 CenterY=-52.4 CenterZ=0 NormalX=0 NormalY=0 NormalZ=1 AngleXU=0 Radius=3.2 StartAngle=3.52599 EndAngle=4.71239
    g258: LineSegment StartX=61 StartY=-55.6 StartZ=0 EndX=63.2797 EndY=-55.6 EndZ=0
    g259: ArcOfCircle CenterX=66 CenterY=-52.4 CenterZ=0 NormalX=0 NormalY=0 NormalZ=1 AngleXU=0 Radius=4.2 StartAngle=4.00784 EndAngle=5.41694
    g260: LineSegment StartX=68.7203 StartY=-55.6 StartZ=0 EndX=70.7586 EndY=-55.6 EndZ=0
    g261: ArcOfCircle CenterX=72.65 CenterY=-54.95 CenterZ=0 NormalX=0 NormalY=0 NormalZ=1 AngleXU=0 Radius=2 StartAngle=3.4726 EndAngle=4.71239
    g262: LineSegment StartX=75 StartY=-56.95 StartZ=0 EndX=72.65 EndY=-56.95 EndZ=0
    g263: ArcOfCircle CenterX=75 CenterY=-54.95 CenterZ=0 NormalX=0 NormalY=0 NormalZ=1 AngleXU=0 Radius=2 StartAngle=4.71239 EndAngle=6.28319
    g264: LineSegment StartX=77 StartY=-49.85 StartZ=0 EndX=77 EndY=-54.95 EndZ=0
    g265: ArcOfCircle CenterX=75 CenterY=-49.85 CenterZ=0 NormalX=0 NormalY=0 NormalZ=1 AngleXU=0 Radius=2 StartAngle=0 EndAngle=1.42023
    g266: LineSegment StartX=75.3 StartY=-45.5 StartZ=0 EndX=75.3 EndY=-47.8726 EndZ=0
    g267: ArcOfCircle CenterX=73.3 CenterY=-45.5 CenterZ=0 NormalX=0 NormalY=0 NormalZ=1 AngleXU=0 Radius=2 StartAngle=4e-16 EndAngle=1.5708
    g268: LineSegment StartX=62 StartY=-43.5 StartZ=0 EndX=73.3 EndY=-43.5 EndZ=0
    g269: ArcOfCircle CenterX=62 CenterY=-47.7 CenterZ=0 NormalX=0 NormalY=0 NormalZ=1 AngleXU=0 Radius=4.2 StartAngle=1.5708 EndAngle=2.77639
    g270: LineSegment StartX=57.7 StartY=-46.2 StartZ=0 EndX=58.077 EndY=-46.2 EndZ=0
    g271: ArcOfCircle CenterX=57.7 CenterY=-48.2 CenterZ=0 NormalX=0 NormalY=0 NormalZ=1 AngleXU=0 Radius=2 StartAngle=1.5708 EndAngle=2.34619
    g272: LineSegment StartX=58 StartY=-53.6 StartZ=0 EndX=58.0335 EndY=-53.6 EndZ=0
    g273: ArcOfCircle CenterX=52 CenterY=-31 CenterZ=0 NormalX=0 NormalY=0 NormalZ=1 AngleXU=0 Radius=3.2 StartAngle=3.52599 EndAngle=4.71239
    g274: LineSegment StartX=52 StartY=-34.2 StartZ=0 EndX=54.2797 EndY=-34.2 EndZ=0
    g275: ArcOfCircle CenterX=57 CenterY=-31 CenterZ=0 NormalX=0 NormalY=0 NormalZ=1 AngleXU=0 Radius=4.2 StartAngle=4.00784 EndAngle=5.41694
    g276: LineSegment StartX=59.7203 StartY=-34.2 StartZ=0 EndX=61.7586 EndY=-34.2 EndZ=0
    g277: ArcOfCircle CenterX=63.65 CenterY=-33.55 CenterZ=0 NormalX=0 NormalY=0 NormalZ=1 AngleXU=0 Radius=2 StartAngle=3.4726 EndAngle=4.71239
    g278: LineSegment StartX=66 StartY=-35.55 StartZ=0 EndX=63.65 EndY=-35.55 EndZ=0
    g279: ArcOfCircle CenterX=66 CenterY=-33.55 CenterZ=0 NormalX=0 NormalY=0 NormalZ=1 AngleXU=0 Radius=2 StartAngle=4.71239 EndAngle=5.84422
    g280: ArcOfCircle CenterX=66 CenterY=-28.45 CenterZ=0 NormalX=0 NormalY=0 NormalZ=1 AngleXU=0 Radius=2 StartAngle=0.794834 EndAngle=1.42023
    g281: LineSegment StartX=66.3 StartY=-24.1 StartZ=0 EndX=66.3 EndY=-26.4726 EndZ=0
    g282: ArcOfCircle CenterX=64.3 CenterY=-24.1 CenterZ=0 NormalX=0 NormalY=0 NormalZ=1 AngleXU=0 Radius=2 StartAngle=4e-16 EndAngle=1.5708
    g283: LineSegment StartX=53 StartY=-22.1 StartZ=0 EndX=64.3 EndY=-22.1 EndZ=0
    g284: ArcOfCircle CenterX=53 CenterY=-26.3 CenterZ=0 NormalX=0 NormalY=0 NormalZ=1 AngleXU=0 Radius=4.2 StartAngle=1.5708 EndAngle=2.77639
    g285: LineSegment StartX=48.7 StartY=-24.8 StartZ=0 EndX=49.077 EndY=-24.8 EndZ=0
    g286: ArcOfCircle CenterX=48.7 CenterY=-26.8 CenterZ=0 NormalX=0 NormalY=0 NormalZ=1 AngleXU=0 Radius=2 StartAngle=1.5708 EndAngle=2.45837
    g287: LineSegment StartX=49 StartY=-32.2 StartZ=0 EndX=49.0335 EndY=-32.2 EndZ=0
    g288: ArcOfCircle CenterX=52 CenterY=-12 CenterZ=0 NormalX=0 NormalY=0 NormalZ=1 AngleXU=0 Radius=3.2 StartAngle=3.52599 EndAngle=4.71239
    g289: LineSegment StartX=52 StartY=-15.2 StartZ=0 EndX=54.2797 EndY=-15.2 EndZ=0
    g290: ArcOfCircle CenterX=57 CenterY=-12 CenterZ=0 NormalX=0 NormalY=0 NormalZ=1 AngleXU=0 Radius=4.2 StartAngle=4.00784 EndAngle=5.41694
    g291: LineSegment StartX=59.7203 StartY=-15.2 StartZ=0 EndX=61.7586 EndY=-15.2 EndZ=0
    g292: ArcOfCircle CenterX=63.65 CenterY=-14.55 CenterZ=0 NormalX=0 NormalY=0 NormalZ=1 AngleXU=0 Radius=2 StartAngle=3.4726 EndAngle=4.71239
    g293: LineSegment StartX=66 StartY=-16.55 StartZ=0 EndX=63.65 EndY=-16.55 EndZ=0
    g294: ArcOfCircle CenterX=66 CenterY=-14.55 CenterZ=0 NormalX=0 NormalY=0 NormalZ=1 AngleXU=0 Radius=2 StartAngle=4.71239 EndAngle=5.84422
    g295: ArcOfCircle CenterX=66 CenterY=-9.45 CenterZ=0 NormalX=0 NormalY=0 NormalZ=1 AngleXU=0 Radius=2 StartAngle=0.794834 EndAngle=1.42023
    g296: LineSegment StartX=66.3 StartY=-5.1 StartZ=0 EndX=66.3 EndY=-7.47263 EndZ=0
    g297: ArcOfCircle CenterX=64.3 CenterY=-5.1 CenterZ=0 NormalX=0 NormalY=0 NormalZ=1 AngleXU=0 Radius=2 StartAngle=4e-16 EndAngle=1.5708
    g298: LineSegment StartX=53 StartY=-3.1 StartZ=0 EndX=64.3 EndY=-3.1 EndZ=0
    g299: ArcOfCircle CenterX=53 CenterY=-7.3 CenterZ=0 NormalX=0 NormalY=0 NormalZ=1 AngleXU=0 Radius=4.2 StartAngle=1.5708 EndAngle=2.77639
    g300: LineSegment StartX=48.7 StartY=-5.8 StartZ=0 EndX=49.077 EndY=-5.8 EndZ=0
    g301: ArcOfCircle CenterX=48.7 CenterY=-7.8 CenterZ=0 NormalX=0 NormalY=0 NormalZ=1 AngleXU=0 Radius=2 StartAngle=1.5708 EndAngle=2.45837
    g302: LineSegment StartX=49 StartY=-13.2 StartZ=0 EndX=49.0335 EndY=-13.2 EndZ=0
    g303: ArcOfCircle CenterX=52 CenterY=7 CenterZ=0 NormalX=0 NormalY=0 NormalZ=1 AngleXU=0 Radius=3.2 StartAngle=3.52599 EndAngle=4.71239
    g304: LineSegment StartX=52 StartY=3.8 StartZ=0 EndX=54.2797 EndY=3.8 EndZ=0
    g305: ArcOfCircle CenterX=57 CenterY=7 CenterZ=0 NormalX=0 NormalY=0 NormalZ=1 AngleXU=0 Radius=4.2 StartAngle=4.00784 EndAngle=5.41694
    g306: LineSegment StartX=59.7203 StartY=3.8 StartZ=0 EndX=61.7586 EndY=3.8 EndZ=0
    g307: ArcOfCircle CenterX=63.65 CenterY=4.45 CenterZ=0 NormalX=0 NormalY=0 NormalZ=1 AngleXU=0 Radius=2 StartAngle=3.4726 EndAngle=4.71239
    g308: LineSegment StartX=66 StartY=2.45 StartZ=0 EndX=63.65 EndY=2.45 EndZ=0
    g309: ArcOfCircle CenterX=66 CenterY=4.45 CenterZ=0 NormalX=0 NormalY=0 NormalZ=1 AngleXU=0 Radius=2 StartAngle=4.71239 EndAngle=5.84422
    g310: ArcOfCircle CenterX=66 CenterY=9.55 CenterZ=0 NormalX=0 NormalY=0 NormalZ=1 AngleXU=0 Radius=2 StartAngle=0.794834 EndAngle=1.42023
    g311: LineSegment StartX=66.3 StartY=13.9 StartZ=0 EndX=66.3 EndY=11.5274 EndZ=0
    g312: ArcOfCircle CenterX=64.3 CenterY=13.9 CenterZ=0 NormalX=0 NormalY=0 NormalZ=1 AngleXU=0 Radius=2 StartAngle=4e-16 EndAngle=1.5708
    g313: LineSegment StartX=53 StartY=15.9 StartZ=0 EndX=64.3 EndY=15.9 EndZ=0
    g314: ArcOfCircle CenterX=53 CenterY=11.7 CenterZ=0 NormalX=0 NormalY=0 NormalZ=1 AngleXU=0 Radius=4.2 StartAngle=1.5708 EndAngle=2.77639
    g315: LineSegment StartX=48.7 StartY=13.2 StartZ=0 EndX=49.077 EndY=13.2 EndZ=0
    g316: ArcOfCircle CenterX=48.7 CenterY=11.2 CenterZ=0 NormalX=0 NormalY=0 NormalZ=1 AngleXU=0 Radius=2 StartAngle=1.5708 EndAngle=2.45837
    g317: LineSegment StartX=49 StartY=5.8 StartZ=0 EndX=49.0335 EndY=5.8 EndZ=0
    g318: ArcOfCircle CenterX=71 CenterY=4.8 CenterZ=0 NormalX=0 NormalY=0 NormalZ=1 AngleXU=0 Radius=3.2 StartAngle=3.52599 EndAngle=4.71239
    g319: LineSegment StartX=71 StartY=1.6 StartZ=0 EndX=73.2797 EndY=1.6 EndZ=0
    g320: ArcOfCircle CenterX=76 CenterY=4.8 CenterZ=0 NormalX=0 NormalY=0 NormalZ=1 AngleXU=0 Radius=4.2 StartAngle=4.00784 EndAngle=5.41694
    g321: LineSegment StartX=78.7203 StartY=1.6 StartZ=0 EndX=80.7586 EndY=1.6 EndZ=0
    g322: ArcOfCircle CenterX=82.65 CenterY=2.25 CenterZ=0 NormalX=0 NormalY=0 NormalZ=1 AngleXU=0 Radius=2 StartAngle=3.4726 EndAngle=4.71239
    g323: LineSegment StartX=85 StartY=0.25 StartZ=0 EndX=82.65 EndY=0.25 EndZ=0
    g324: ArcOfCircle CenterX=85 CenterY=2.25 CenterZ=0 NormalX=0 NormalY=0 NormalZ=1 AngleXU=0 Radius=2 StartAngle=4.71239 EndAngle=5.84422
    g325: ArcOfCircle CenterX=85 CenterY=7.35 CenterZ=0 NormalX=0 NormalY=0 NormalZ=1 AngleXU=0 Radius=2 StartAngle=0.794834 EndAngle=1.42023
    g326: LineSegment StartX=85.3 StartY=11.7 StartZ=0 EndX=85.3 EndY=9.32737 EndZ=0
    g327: ArcOfCircle CenterX=83.3 CenterY=11.7 CenterZ=0 NormalX=0 NormalY=0 NormalZ=1 AngleXU=0 Radius=2 StartAngle=4e-16 EndAngle=1.5708
    g328: LineSegment StartX=72 StartY=13.7 StartZ=0 EndX=83.3 EndY=13.7 EndZ=0
    g329: ArcOfCircle CenterX=72 CenterY=9.5 CenterZ=0 NormalX=0 NormalY=0 NormalZ=1 AngleXU=0 Radius=4.2 StartAngle=1.5708 EndAngle=2.77639
    g330: LineSegment StartX=67.7 StartY=11 StartZ=0 EndX=68.077 EndY=11 EndZ=0
    g331: ArcOfCircle CenterX=67.7 CenterY=9 CenterZ=0 NormalX=0 NormalY=0 NormalZ=1 AngleXU=0 Radius=2 StartAngle=1.5708 EndAngle=1.72096
    g332: LineSegment StartX=67.8104 StartY=3.6 StartZ=0 EndX=68.0335 EndY=3.6 EndZ=0
    g333: ArcOfCircle CenterX=71 CenterY=-14.2 CenterZ=0 NormalX=0 NormalY=0 NormalZ=1 AngleXU=0 Radius=3.2 StartAngle=3.52599 EndAngle=4.71239
    g334: LineSegment StartX=71 StartY=-17.4 StartZ=0 EndX=73.2797 EndY=-17.4 EndZ=0
    g335: ArcOfCircle CenterX=76 CenterY=-14.2 CenterZ=0 NormalX=0 NormalY=0 NormalZ=1 AngleXU=0 Radius=4.2 StartAngle=4.00784 EndAngle=5.41694
    g336: LineSegment StartX=78.7203 StartY=-17.4 StartZ=0 EndX=80.7586 EndY=-17.4 EndZ=0
    g337: ArcOfCircle CenterX=82.65 CenterY=-16.75 CenterZ=0 NormalX=0 NormalY=0 NormalZ=1 AngleXU=0 Radius=2 StartAngle=3.4726 EndAngle=4.71239
    g338: LineSegment StartX=85 StartY=-18.75 StartZ=0 EndX=82.65 EndY=-18.75 EndZ=0
    g339: ArcOfCircle CenterX=85 CenterY=-16.75 CenterZ=0 NormalX=0 NormalY=0 NormalZ=1 AngleXU=0 Radius=2 StartAngle=4.71239 EndAngle=5.84422
    g340: ArcOfCircle CenterX=85 CenterY=-11.65 CenterZ=0 NormalX=0 NormalY=0 NormalZ=1 AngleXU=0 Radius=2 StartAngle=0.794834 EndAngle=1.42023
    g341: LineSegment StartX=85.3 StartY=-7.3 StartZ=0 EndX=85.3 EndY=-9.67263 EndZ=0
    g342: ArcOfCircle CenterX=83.3 CenterY=-7.3 CenterZ=0 NormalX=0 NormalY=0 NormalZ=1 AngleXU=0 Radius=2 StartAngle=4e-16 EndAngle=1.5708
    g343: LineSegment StartX=72 StartY=-5.3 StartZ=0 EndX=83.3 EndY=-5.3 EndZ=0
    g344: ArcOfCircle CenterX=72 CenterY=-9.5 CenterZ=0 NormalX=0 NormalY=0 NormalZ=1 AngleXU=0 Radius=4.2 StartAngle=1.5708 EndAngle=2.77639
    g345: LineSegment StartX=67.7 StartY=-8 StartZ=0 EndX=68.077 EndY=-8 EndZ=0
    g346: ArcOfCircle CenterX=67.7 CenterY=-10 CenterZ=0 NormalX=0 NormalY=0 NormalZ=1 AngleXU=0 Radius=2 StartAngle=1.5708 EndAngle=1.72096
    g347: LineSegment StartX=67.8104 StartY=-15.4 StartZ=0 EndX=68.0335 EndY=-15.4 EndZ=0
    g348: ArcOfCircle CenterX=71 CenterY=-33.2 CenterZ=0 NormalX=0 NormalY=0 NormalZ=1 AngleXU=0 Radius=3.2 StartAngle=3.52599 EndAngle=4.71239
    g349: LineSegment StartX=71 StartY=-36.4 StartZ=0 EndX=73.2797 EndY=-36.4 EndZ=0
    g350: ArcOfCircle CenterX=76 CenterY=-33.2 CenterZ=0 NormalX=0 NormalY=0 NormalZ=1 AngleXU=0 Radius=4.2 StartAngle=4.00784 EndAngle=5.41694
    g351: LineSegment StartX=78.7203 StartY=-36.4 StartZ=0 EndX=80.7586 EndY=-36.4 EndZ=0
    g352: ArcOfCircle CenterX=82.65 CenterY=-35.75 CenterZ=0 NormalX=0 NormalY=0 NormalZ=1 AngleXU=0 Radius=2 StartAngle=3.4726 EndAngle=4.71239
    g353: LineSegment StartX=85 StartY=-37.75 StartZ=0 EndX=82.65 EndY=-37.75 EndZ=0
    g354: ArcOfCircle CenterX=85 CenterY=-35.75 CenterZ=0 NormalX=0 NormalY=0 NormalZ=1 AngleXU=0 Radius=2 StartAngle=4.71239 EndAngle=5.84422
    g355: ArcOfCircle CenterX=85 CenterY=-30.65 CenterZ=0 NormalX=0 NormalY=0 NormalZ=1 AngleXU=0 Radius=2 StartAngle=0.794834 EndAngle=1.42023
    g356: LineSegment StartX=85.3 StartY=-26.3 StartZ=0 EndX=85.3 EndY=-28.6726 EndZ=0
    g357: ArcOfCircle CenterX=83.3 CenterY=-26.3 CenterZ=0 NormalX=0 NormalY=0 NormalZ=1 AngleXU=0 Radius=2 StartAngle=4e-16 EndAngle=1.5708
    g358: LineSegment StartX=72 StartY=-24.3 StartZ=0 EndX=83.3 EndY=-24.3 EndZ=0
    g359: ArcOfCircle CenterX=72 CenterY=-28.5 CenterZ=0 NormalX=0 NormalY=0 NormalZ=1 AngleXU=0 Radius=4.2 StartAngle=1.5708 EndAngle=2.77639
    g360: LineSegment StartX=67.7 StartY=-27 StartZ=0 EndX=68.077 EndY=-27 EndZ=0
    g361: ArcOfCircle CenterX=67.7 CenterY=-29 CenterZ=0 NormalX=0 NormalY=0 NormalZ=1 AngleXU=0 Radius=2 StartAngle=1.5708 EndAngle=1.72096
    g362: LineSegment StartX=67.8104 StartY=-34.4 StartZ=0 EndX=68.0335 EndY=-34.4 EndZ=0
    g363: ArcOfCircle CenterX=90 CenterY=-35.4 CenterZ=0 NormalX=0 NormalY=0 NormalZ=1 AngleXU=0 Radius=3.2 StartAngle=3.52599 EndAngle=4.71239
    g364: LineSegment StartX=90 StartY=-38.6 StartZ=0 EndX=92.2797 EndY=-38.6 EndZ=0
    g365: ArcOfCircle CenterX=95 CenterY=-35.4 CenterZ=0 NormalX=0 NormalY=0 NormalZ=1 AngleXU=0 Radius=4.2 StartAngle=4.00784 EndAngle=5.41694
    g366: LineSegment StartX=97.7203 StartY=-38.6 StartZ=0 EndX=99.7586 EndY=-38.6 EndZ=0
    g367: ArcOfCircle CenterX=101.65 CenterY=-37.95 CenterZ=0 NormalX=0 NormalY=0 NormalZ=1 AngleXU=0 Radius=2 StartAngle=3.4726 EndAngle=4.71239
    g368: LineSegment StartX=104 StartY=-39.95 StartZ=0 EndX=101.65 EndY=-39.95 EndZ=0
    g369: ArcOfCircle CenterX=104 CenterY=-37.95 CenterZ=0 NormalX=0 NormalY=0 NormalZ=1 AngleXU=0 Radius=2 StartAngle=4.71239 EndAngle=6.28319
    g370: LineSegment StartX=106 StartY=-32.85 StartZ=0 EndX=106 EndY=-37.95 EndZ=0
    g371: ArcOfCircle CenterX=104 CenterY=-32.85 CenterZ=0 NormalX=0 NormalY=0 NormalZ=1 AngleXU=0 Radius=2 StartAngle=0 EndAngle=1.42023
    g372: LineSegment StartX=104.3 StartY=-28.5 StartZ=0 EndX=104.3 EndY=-30.8726 EndZ=0
    g373: ArcOfCircle CenterX=102.3 CenterY=-28.5 CenterZ=0 NormalX=0 NormalY=0 NormalZ=1 AngleXU=0 Radius=2 StartAngle=4e-16 EndAngle=1.5708
    g374: LineSegment StartX=91 StartY=-26.5 StartZ=0 EndX=102.3 EndY=-26.5 EndZ=0
    g375: ArcOfCircle CenterX=91 CenterY=-30.7 CenterZ=0 NormalX=0 NormalY=0 NormalZ=1 AngleXU=0 Radius=4.2 StartAngle=1.5708 EndAngle=2.77639
    g376: LineSegment StartX=86.7 StartY=-29.2 StartZ=0 EndX=87.077 EndY=-29.2 EndZ=0
    g377: ArcOfCircle CenterX=86.7 CenterY=-31.2 CenterZ=0 NormalX=0 NormalY=0 NormalZ=1 AngleXU=0 Radius=2 StartAngle=1.5708 EndAngle=1.72096
    g378: LineSegment StartX=86.8104 StartY=-36.6 StartZ=0 EndX=87.0335 EndY=-36.6 EndZ=0
    g379: ArcOfCircle CenterX=90 CenterY=-16.4 CenterZ=0 NormalX=0 NormalY=0 NormalZ=1 AngleXU=0 Radius=3.2 StartAngle=3.52599 EndAngle=4.71239
    g380: LineSegment StartX=90 StartY=-19.6 StartZ=0 EndX=92.2797 EndY=-19.6 EndZ=0
    g381: ArcOfCircle CenterX=95 CenterY=-16.4 CenterZ=0 NormalX=0 NormalY=0 NormalZ=1 AngleXU=0 Radius=4.2 StartAngle=4.00784 EndAngle=5.41694
    g382: LineSegment StartX=97.7203 StartY=-19.6 StartZ=0 EndX=99.7586 EndY=-19.6 EndZ=0
    g383: ArcOfCircle CenterX=101.65 CenterY=-18.95 CenterZ=0 NormalX=0 NormalY=0 NormalZ=1 AngleXU=0 Radius=2 StartAngle=3.4726 EndAngle=4.71239
    g384: LineSegment StartX=104 StartY=-20.95 StartZ=0 EndX=101.65 EndY=-20.95 EndZ=0
    g385: ArcOfCircle CenterX=104 CenterY=-18.95 CenterZ=0 NormalX=0 NormalY=0 NormalZ=1 AngleXU=0 Radius=2 StartAngle=4.71239 EndAngle=6.28319
    g386: LineSegment StartX=106 StartY=-13.85 StartZ=0 EndX=106 EndY=-18.95 EndZ=0
    g387: ArcOfCircle CenterX=104 CenterY=-13.85 CenterZ=0 NormalX=0 NormalY=0 NormalZ=1 AngleXU=0 Radius=2 StartAngle=0 EndAngle=1.42023
    g388: LineSegment StartX=104.3 StartY=-9.5 StartZ=0 EndX=104.3 EndY=-11.8726 EndZ=0
    g389: ArcOfCircle CenterX=102.3 CenterY=-9.5 CenterZ=0 NormalX=0 NormalY=0 NormalZ=1 AngleXU=0 Radius=2 StartAngle=4e-16 EndAngle=1.5708
    g390: LineSegment StartX=91 StartY=-7.5 StartZ=0 EndX=102.3 EndY=-7.5 EndZ=0
    g391: ArcOfCircle CenterX=91 CenterY=-11.7 CenterZ=0 NormalX=0 NormalY=0 NormalZ=1 AngleXU=0 Radius=4.2 StartAngle=1.5708 EndAngle=2.77639
    g392: LineSegment StartX=86.7 StartY=-10.2 StartZ=0 EndX=87.077 EndY=-10.2 EndZ=0
    g393: ArcOfCircle CenterX=86.7 CenterY=-12.2 CenterZ=0 NormalX=0 NormalY=0 NormalZ=1 AngleXU=0 Radius=2 StartAngle=1.5708 EndAngle=1.72096
    g394: LineSegment StartX=86.8104 StartY=-17.6 StartZ=0 EndX=87.0335 EndY=-17.6 EndZ=0
    g395: ArcOfCircle CenterX=90 CenterY=2.6 CenterZ=0 NormalX=0 NormalY=0 NormalZ=1 AngleXU=0 Radius=3.2 StartAngle=3.52599 EndAngle=4.71239
    g396: LineSegment StartX=90 StartY=-0.6 StartZ=0 EndX=92.2797 EndY=-0.6 EndZ=0
    g397: ArcOfCircle CenterX=95 CenterY=2.6 CenterZ=0 NormalX=0 NormalY=0 NormalZ=1 AngleXU=0 Radius=4.2 StartAngle=4.00784 EndAngle=5.41694
    g398: LineSegment StartX=97.7203 StartY=-0.6 StartZ=0 EndX=99.7586 EndY=-0.6 EndZ=0
    g399: ArcOfCircle CenterX=101.65 CenterY=0.05 CenterZ=0 NormalX=0 NormalY=0 NormalZ=1 AngleXU=0 Radius=2 StartAngle=3.4726 EndAngle=4.71239
    ... +231 more geometry lines
  constraints (907):
    c: Coincident(g99,g100)
    c: Horizontal(g100)
    c: Coincident(g100,g101)
    c: Coincident(g101,g102)
    c: Horizontal(g102)
    c: Coincident(g102,g103)
    c: Coincident(g103,g104)
    c: Horizontal(g104)
    c: Coincident(g104,g105)
    c: Coincident(g105,g106)
    c: Vertical(g106)
    c: Vertical(g107)
    c: Coincident(g107,g108)
    c: Coincident(g108,g109)
    c: Horizontal(g109)
    c: Coincident(g109,g110)
    c: Coincident(g110,g111)
    c: Horizontal(g111)
    c: Coincident(g111,g112)
    c: Coincident(g112,g113)
    c: Vertical(g113)
    c: Coincident(g113,g114)
    c: Coincident(g114,g115)
    c: Horizontal(g115)
    c: Coincident(g115,g99)
    c: Coincident(g116,g117)
    c: Horizontal(g117)
    c: Coincident(g117,g118)
    c: Coincident(g118,g119)
    c: Horizontal(g119)
    c: Coincident(g119,g120)
    c: Coincident(g120,g121)
    c: Horizontal(g121)
    c: Coincident(g121,g122)
    c: Coincident(g122,g123)
    c: Vertical(g123)
    c: Vertical(g124)
    c: Coincident(g124,g125)
    c: Coincident(g125,g126)
    c: Horizontal(g126)
    c: Coincident(g126,g127)
    c: Coincident(g127,g128)
    c: Horizontal(g128)
    c: Coincident(g128,g129)
    c: Coincident(g129,g130)
    c: Vertical(g130)
    c: Coincident(g130,g131)
    c: Coincident(g131,g132)
    c: Horizontal(g132)
    c: Coincident(g132,g116)
    c: Coincident(g133,g134)
    c: Horizontal(g134)
    c: Coincident(g134,g135)
    c: Coincident(g135,g136)
    c: Horizontal(g136)
    c: Coincident(g136,g137)
    c: Coincident(g137,g138)
    c: Horizontal(g138)
    c: Coincident(g138,g139)
    c: Coincident(g139,g140)
    c: Vertical(g140)
    c: Vertical(g141)
    c: Coincident(g141,g142)
    c: Coincident(g142,g143)
    c: Horizontal(g143)
    c: Coincident(g143,g144)
    c: Coincident(g144,g145)
    c: Horizontal(g145)
    c: Coincident(g145,g146)
    c: Coincident(g146,g147)
    c: Vertical(g147)
    c: Coincident(g147,g148)
    c: Coincident(g148,g149)
    c: Horizontal(g149)
    c: Coincident(g149,g133)
    c: Coincident(g150,g151)
    c: Horizontal(g151)
    c: Coincident(g151,g152)
    c: Coincident(g152,g153)
    c: Horizontal(g153)
    c: Coincident(g153,g154)
    c: Coincident(g154,g155)
    c: Horizontal(g155)
    c: Coincident(g155,g156)
    c: Coincident(g156,g157)
    c: Vertical(g157)
    c: Coincident(g157,g158)
    c: Coincident(g159,g160)
    c: Horizontal(g160)
    c: Coincident(g160,g161)
    c: Coincident(g161,g162)
    c: Horizontal(g162)
    c: Coincident(g162,g163)
    c: Horizontal(g164)
    c: Coincident(g164,g150)
    c: Coincident(g165,g166)
    c: Horizontal(g166)
    c: Coincident(g166,g167)
    c: Coincident(g167,g168)
    c: Horizontal(g168)
    c: Coincident(g168,g169)
    c: Coincident(g169,g170)
    c: Horizontal(g170)
    c: Coincident(g170,g171)
    c: Coincident(g171,g172)
    c: Vertical(g172)
    c: Coincident(g172,g173)
    c: Coincident(g174,g175)
    c: Horizontal(g175)
    c: Coincident(g175,g176)
    c: Coincident(g176,g177)
    c: Horizontal(g177)
    c: Coincident(g177,g178)
    c: Horizontal(g179)
    c: Coincident(g179,g165)
    c: Coincident(g180,g181)
    c: Horizontal(g181)
    c: Coincident(g181,g182)
    c: Coincident(g182,g183)
    c: Horizontal(g183)
    c: Coincident(g183,g184)
    c: Coincident(g184,g185)
    c: Horizontal(g185)
    c: Coincident(g185,g186)
    c: Coincident(g186,g187)
    c: Vertical(g187)
    c: Coincident(g187,g188)
    c: Coincident(g189,g190)
    c: Horizontal(g190)
    c: Coincident(g190,g191)
    c: Coincident(g191,g192)
    c: Horizontal(g192)
    c: Coincident(g192,g193)
    c: Horizontal(g194)
    c: Coincident(g194,g180)
    c: Coincident(g195,g196)
    c: Horizontal(g196)
    c: Coincident(g196,g197)
    c: Coincident(g197,g198)
    c: Horizontal(g198)
    c: Coincident(g198,g199)
    c: Coincident(g199,g200)
    c: Horizontal(g200)
    c: Coincident(g200,g201)
    c: Coincident(g201,g202)
    c: Vertical(g202)
    c: Coincident(g203,g204)
    c: Horizontal(g204)
    c: Coincident(g204,g205)
    c: Coincident(g205,g206)
    c: Horizontal(g206)
    c: Coincident(g206,g207)
    c: Coincident(g207,g208)
    c: Vertical(g208)
    c: Horizontal(g209)
    c: Coincident(g209,g195)
    c: Coincident(g210,g211)
    c: Horizontal(g211)
    c: Coincident(g211,g212)
    c: Coincident(g212,g213)
    c: Horizontal(g213)
    c: Coincident(g213,g214)
    c: Coincident(g214,g215)
    c: Horizontal(g215)
    c: Coincident(g215,g216)
    c: Coincident(g216,g217)
    c: Vertical(g217)
    c: Coincident(g218,g219)
    c: Horizontal(g219)
    c: Coincident(g219,g220)
    c: Coincident(g220,g221)
    c: Horizontal(g221)
    c: Coincident(g221,g222)
    c: Coincident(g222,g223)
    c: Vertical(g223)
    c: Horizontal(g224)
    c: Coincident(g224,g210)
    c: Coincident(g225,g226)
    c: Horizontal(g226)
    c: Coincident(g226,g227)
    c: Coincident(g227,g228)
    c: Horizontal(g228)
    c: Coincident(g228,g229)
    c: Coincident(g229,g230)
    c: Horizontal(g230)
    c: Coincident(g230,g231)
    c: Coincident(g231,g232)
    c: Vertical(g232)
    c: Coincident(g233,g234)
    c: Horizontal(g234)
    c: Coincident(g234,g235)
    c: Coincident(g235,g236)
    c: Horizontal(g236)
    c: Coincident(g236,g237)
    c: Coincident(g237,g238)
    c: Vertical(g238)
    c: Horizontal(g239)
    c: Coincident(g239,g225)
    c: Coincident(g240,g241)
    c: Horizontal(g241)
    c: Coincident(g241,g242)
    c: Coincident(g242,g243)
    c: Horizontal(g243)
    c: Coincident(g243,g244)
    c: Coincident(g244,g245)
    c: Horizontal(g245)
    c: Coincident(g245,g246)
    c: Coincident(g246,g247)
    c: Vertical(g247)
    c: Vertical(g248)
    c: Coincident(g248,g249)
    c: Coincident(g249,g250)
    c: Horizontal(g250)
    c: Coincident(g250,g251)
    c: Coincident(g251,g252)
    c: Horizontal(g252)
    c: Coincident(g252,g253)
    c: Coincident(g253,g254)
    c: Vertical(g254)
    c: Coincident(g254,g255)
    c: Coincident(g255,g256)
    c: Horizontal(g256)
    c: Coincident(g256,g240)
    c: Coincident(g257,g258)
    c: Horizontal(g258)
    c: Coincident(g258,g259)
    c: Coincident(g259,g260)
    c: Horizontal(g260)
    c: Coincident(g260,g261)
    c: Coincident(g261,g262)
    c: Horizontal(g262)
    c: Coincident(g262,g263)
    c: Coincident(g263,g264)
    c: Vertical(g264)
    c: Coincident(g264,g265)
    c: Coincident(g265,g266)
    c: Vertical(g266)
    c: Coincident(g266,g267)
    c: Coincident(g267,g268)
    c: Horizontal(g268)
    c: Coincident(g268,g269)
    c: Coincident(g269,g270)
    c: Horizontal(g270)
    c: Coincident(g270,g271)
    c: Horizontal(g272)
    c: Coincident(g272,g257)
    c: Coincident(g273,g274)
    c: Horizontal(g274)
    c: Coincident(g274,g275)
    c: Coincident(g275,g276)
    c: Horizontal(g276)
    c: Coincident(g276,g277)
    c: Coincident(g277,g278)
    c: Horizontal(g278)
    c: Coincident(g278,g279)
    c: Coincident(g280,g281)
    c: Vertical(g281)
    c: Coincident(g281,g282)
    c: Coincident(g282,g283)
    c: Horizontal(g283)
    c: Coincident(g283,g284)
    c: Coincident(g284,g285)
    c: Horizontal(g285)
    c: Coincident(g285,g286)
    c: Horizontal(g287)
    c: Coincident(g287,g273)
    c: Coincident(g288,g289)
    c: Horizontal(g289)
    c: Coincident(g289,g290)
    c: Coincident(g290,g291)
    c: Horizontal(g291)
    c: Coincident(g291,g292)
    c: Coincident(g292,g293)
    c: Horizontal(g293)
    c: Coincident(g293,g294)
    c: Coincident(g295,g296)
    c: Vertical(g296)
    c: Coincident(g296,g297)
    c: Coincident(g297,g298)
    c: Horizontal(g298)
    c: Coincident(g298,g299)
    c: Coincident(g299,g300)
    c: Horizontal(g300)
    c: Coincident(g300,g301)
    c: Horizontal(g302)
    c: Coincident(g302,g288)
    c: Coincident(g303,g304)
    c: Horizontal(g304)
    c: Coincident(g304,g305)
    c: Coincident(g305,g306)
    c: Horizontal(g306)
    c: Coincident(g306,g307)
    c: Coincident(g307,g308)
    c: Horizontal(g308)
    c: Coincident(g308,g309)
    c: Coincident(g310,g311)
    c: Vertical(g311)
    c: Coincident(g311,g312)
    c: Coincident(g312,g313)
    c: Horizontal(g313)
    c: Coincident(g313,g314)
    c: Coincident(g314,g315)
    c: Horizontal(g315)
    c: Coincident(g315,g316)
    c: Horizontal(g317)
    c: Coincident(g317,g303)
    c: Coincident(g318,g319)
    c: Horizontal(g319)
    c: Coincident(g319,g320)
    c: Coincident(g320,g321)
    c: Horizontal(g321)
    c: Coincident(g321,g322)
    c: Coincident(g322,g323)
    c: Horizontal(g323)
    c: Coincident(g323,g324)
    c: Coincident(g325,g326)
    c: Vertical(g326)
    c: Coincident(g326,g327)
    c: Coincident(g327,g328)
    c: Horizontal(g328)
    c: Coincident(g328,g329)
    c: Coincident(g329,g330)
    c: Horizontal(g330)
    c: Coincident(g330,g331)
    c: Horizontal(g332)
    c: Coincident(g332,g318)
    c: Coincident(g333,g334)
    c: Horizontal(g334)
    c: Coincident(g334,g335)
    c: Coincident(g335,g336)
    c: Horizontal(g336)
    c: Coincident(g336,g337)
    c: Coincident(g337,g338)
    c: Horizontal(g338)
    c: Coincident(g338,g339)
    c: Coincident(g340,g341)
    c: Vertical(g341)
    c: Coincident(g341,g342)
    c: Coincident(g342,g343)
    c: Horizontal(g343)
    c: Coincident(g343,g344)
    c: Coincident(g344,g345)
    c: Horizontal(g345)
    c: Coincident(g345,g346)
    c: Horizontal(g347)
    c: Coincident(g347,g333)
    c: Coincident(g348,g349)
    c: Horizontal(g349)
    c: Coincident(g349,g350)
    c: Coincident(g350,g351)
    c: Horizontal(g351)
    c: Coincident(g351,g352)
    c: Coincident(g352,g353)
    c: Horizontal(g353)
    c: Coincident(g353,g354)
    c: Coincident(g355,g356)
    c: Vertical(g356)
    c: Coincident(g356,g357)
    c: Coincident(g357,g358)
    c: Horizontal(g358)
    c: Coincident(g358,g359)
    c: Coincident(g359,g360)
    c: Horizontal(g360)
    c: Coincident(g360,g361)
    c: Horizontal(g362)
    c: Coincident(g362,g348)
    c: Coincident(g363,g364)
    c: Horizontal(g364)
    c: Coincident(g364,g365)
    c: Coincident(g365,g366)
    c: Horizontal(g366)
    c: Coincident(g366,g367)
    c: Coincident(g367,g368)
    c: Horizontal(g368)
    c: Coincident(g368,g369)
    c: Coincident(g369,g370)
    c: Vertical(g370)
    c: Coincident(g370,g371)
    c: Coincident(g371,g372)
    c: Vertical(g372)
    c: Coincident(g372,g373)
    c: Coincident(g373,g374)
    c: Horizontal(g374)
    c: Coincident(g374,g375)
    c: Coincident(g375,g376)
    c: Horizontal(g376)
    c: Coincident(g376,g377)
    c: Horizontal(g378)
    c: Coincident(g378,g363)
    c: Coincident(g379,g380)
    c: Horizontal(g380)
    c: Coincident(g380,g381)
    c: Coincident(g381,g382)
    c: Horizontal(g382)
    c: Coincident(g382,g383)
    c: Coincident(g383,g384)
    c: Horizontal(g384)
    c: Coincident(g384,g385)
    c: Coincident(g385,g386)
    c: Vertical(g386)
    c: Coincident(g386,g387)
    c: Coincident(g387,g388)
    c: Vertical(g388)
    c: Coincident(g388,g389)
    c: Coincident(g389,g390)
    c: Horizontal(g390)
    c: Coincident(g390,g391)
    c: Coincident(g391,g392)
    c: Horizontal(g392)
    c: Coincident(g392,g393)
    c: Horizontal(g394)
    c: Coincident(g394,g379)
    c: Coincident(g395,g396)
    c: Horizontal(g396)
    c: Coincident(g396,g397)
    c: Coincident(g397,g398)
    c: Horizontal(g398)
    c: Coincident(g398,g399)
    c: Coincident(g399,g400)
    c: Horizontal(g400)
    c: Coincident(g400,g401)
    c: Coincident(g401,g402)
    c: Vertical(g402)
    c: Coincident(g402,g403)
    c: Coincident(g403,g404)
    c: Vertical(g404)
    c: Coincident(g404,g405)
    c: Coincident(g405,g406)
    c: Horizontal(g406)
    c: Coincident(g406,g407)
    c: Coincident(g407,g408)
    c: Horizontal(g408)
    c: Coincident(g408,g409)
    c: Horizontal(g410)
    c: Coincident(g410,g395)
    c: Coincident(g107,g193)
    c: Coincident(g194,g106)
    c: Coincident(g208,g189)
    c: PointOnObject(g188,g209)
    c: Coincident(g316,g203)
    c: Coincident(g317,g202)
    c: Coincident(g310,g331)
    c: Coincident(g332,g309)
    c: Coincident(g325,g409)
    c: Coincident(g410,g324)
    c: Coincident(g340,g393)
    c: Coincident(g339,g394)
    c: Coincident(g294,g347)
    c: Coincident(g295,g346)
    c: Coincident(g217,g302)
    c: Coincident(g218,g301)
    c: PointOnObject(g173,g224)
    c: Coincident(g174,g223)
    c: Coincident(g124,g178)
    c: Coincident(g123,g179)
    c: Coincident(g140,g164)
    c: Coincident(g163,g141)
    c: Coincident(g159,g238)
    c: PointOnObject(g158,g239)
    c: Coincident(g232,g287)
    c: Coincident(g286,g233)
    c: Coincident(g361,g280)
    c: Coincident(g362,g279)
    c: Coincident(g377,g355)
    c: Coincident(g354,g378)
    c: Coincident(g248,g271)
    c: Coincident(g247,g272)
    c: PointOnObject(g25,g110)
    c: PointOnObject(g411,g104)
    c: PointOnObject(g26,g109)
    c: PointOnObject(g412,g105)
    c: PointOnObject(g27,g109)
    c: PointOnObject(g413,g105)
    c: PointOnObject(g24,g110)
    c: PointOnObject(g414,g103)
    c: PointOnObject(g23,g110)
    c: PointOnObject(g415,g102)
    c: PointOnObject(g22,g112)
    c: PointOnObject(g416,g101)
    c: PointOnObject(g21,g112)
    c: PointOnObject(g417,g101)
    c: PointOnObject(g20,g113)
    c: PointOnObject(g418,g100)
    c: PointOnObject(g19,g113)
    c: PointOnObject(g419,g99)
    c: PointOnObject(g28,g109)
    c: PointOnObject(g420,g180)
    c: PointOnObject(g29,g109)
    c: PointOnObject(g421,g181)
    c: PointOnObject(g30,g109)
    c: PointOnObject(g422,g182)
    c: PointOnObject(g630,g193)
    c: PointOnObject(g423,g182)
    c: PointOnObject(g32,g191)
    c: PointOnObject(g424,g183)
    c: PointOnObject(g33,g191)
    c: PointOnObject(g425,g185)
    c: PointOnObject(g34,g191)
    c: PointOnObject(g426,g185)
    c: PointOnObject(g35,g190)
    c: PointOnObject(g427,g186)
    c: PointOnObject(g36,g190)
    c: PointOnObject(g428,g187)
    c: PointOnObject(g37,g190)
    c: PointOnObject(g429,g187)
    c: PointOnObject(g38,g190)
    c: PointOnObject(g430,g187)
    c: PointOnObject(g39,g190)
    c: PointOnObject(g431,g195)
    c: PointOnObject(g40,g189)
    c: PointOnObject(g432,g196)
    c: PointOnObject(g41,g207)
    c: PointOnObject(g433,g197)
    c: PointOnObject(g42,g207)
    c: PointOnObject(g434,g197)
    c: PointOnObject(g43,g205)
    c: PointOnObject(g435,g198)
    c: PointOnObject(g44,g205)
    c: PointOnObject(g436,g199)
    c: PointOnObject(g45,g205)
    c: PointOnObject(g437,g200)
    c: PointOnObject(g46,g204)
    c: PointOnObject(g438,g201)
    c: PointOnObject(g47,g204)
    c: PointOnObject(g439,g201)
    c: PointOnObject(g48,g204)
    c: PointOnObject(g440,g202)
    c: PointOnObject(g49,g204)
    c: PointOnObject(g441,g303)
    c: PointOnObject(g50,g204)
    c: PointOnObject(g442,g304)
    c: PointOnObject(g51,g203)
    c: PointOnObject(g443,g305)
    c: PointOnObject(g52,g316)
    c: PointOnObject(g444,g305)
    c: PointOnObject(g53,g314)
    c: PointOnObject(g445,g306)
    c: PointOnObject(g54,g314)
    c: PointOnObject(g446,g307)
    c: PointOnObject(g55,g314)
    c: PointOnObject(g447,g308)
    c: PointOnObject(g56,g313)
    c: PointOnObject(g448,g309)
    c: PointOnObject(g57,g313)
    c: PointOnObject(g449,g318)
    c: PointOnObject(g58,g313)
    c: PointOnObject(g450,g319)
    c: PointOnObject(g59,g313)
    c: PointOnObject(g451,g320)
    c: PointOnObject(g60,g313)
    c: PointOnObject(g452,g311)
    c: PointOnObject(g452,g331)
    c: PointOnObject(g453,g320)
    c: PointOnObject(g455,g329)
    c: PointOnObject(g454,g321)
    c: PointOnObject(g61,g312)
    c: PointOnObject(g455,g312)
    c: PointOnObject(g62,g329)
    c: PointOnObject(g456,g322)
    c: PointOnObject(g63,g329)
    c: PointOnObject(g457,g323)
    c: PointOnObject(g64,g328)
    c: PointOnObject(g458,g324)
    c: PointOnObject(g65,g328)
    c: PointOnObject(g459,g395)
    c: PointOnObject(g66,g328)
    c: PointOnObject(g460,g396)
    c: PointOnObject(g67,g328)
    c: PointOnObject(g461,g397)
    c: PointOnObject(g68,g328)
    c: PointOnObject(g462,g326)
    c: PointOnObject(g69,g327)
    c: PointOnObject(g463,g327)
    c: PointOnObject(g462,g409)
    c: PointOnObject(g464,g397)
    c: PointOnObject(g463,g407)
    c: PointOnObject(g465,g398)
    c: PointOnObject(g70,g407)
    c: PointOnObject(g466,g399)
    c: PointOnObject(g71,g407)
    c: PointOnObject(g467,g400)
    c: PointOnObject(g72,g406)
    c: PointOnObject(g468,g401)
    c: PointOnObject(g73,g406)
    c: PointOnObject(g469,g401)
    c: PointOnObject(g74,g406)
    c: PointOnObject(g470,g402)
    c: PointOnObject(g75,g406)
    c: PointOnObject(g471,g402)
    c: PointOnObject(g76,g406)
    c: PointOnObject(g472,g404)
    c: PointOnObject(g77,g405)
    c: PointOnObject(g473,g405)
    c: PointOnObject(g10,g130)
    c: PointOnObject(g474,g116)
    c: PointOnObject(g11,g130)
    c: PointOnObject(g475,g117)
    c: PointOnObject(g12,g129)
    c: PointOnObject(g476,g118)
    c: PointOnObject(g13,g129)
    c: PointOnObject(g477,g118)
    c: PointOnObject(g14,g127)
    c: PointOnObject(g478,g119)
    c: PointOnObject(g15,g127)
    c: PointOnObject(g479,g120)
    c: PointOnObject(g16,g127)
    c: PointOnObject(g480,g121)
    c: PointOnObject(g17,g126)
    c: PointOnObject(g481,g122)
    c: PointOnObject(g18,g126)
    c: PointOnObject(g482,g122)
    c: PointOnObject(g419,g126)
    c: PointOnObject(g483,g165)
    c: PointOnObject(g418,g126)
    c: PointOnObject(g484,g166)
    c: PointOnObject(g417,g126)
    c: PointOnObject(g485,g167)
    c: PointOnObject(g490,g178)
    c: PointOnObject(g486,g167)
    c: PointOnObject(g415,g176)
    c: PointOnObject(g487,g168)
    c: PointOnObject(g414,g176)
    c: PointOnObject(g488,g169)
    c: PointOnObject(g411,g176)
    c: PointOnObject(g489,g170)
    c: PointOnObject(g416,g125)
    c: PointOnObject(g490,g125)
    c: PointOnObject(g412,g175)
    c: PointOnObject(g491,g171)
    c: PointOnObject(g413,g175)
    c: PointOnObject(g492,g171)
    c: PointOnObject(g420,g175)
    c: PointOnObject(g493,g172)
    c: PointOnObject(g421,g175)
    c: PointOnObject(g494,g172)
    c: PointOnObject(g422,g175)
    c: PointOnObject(g495,g210)
    c: PointOnObject(g423,g174)
    c: PointOnObject(g496,g211)
    c: PointOnObject(g424,g222)
    c: PointOnObject(g497,g212)
    c: PointOnObject(g425,g222)
    c: PointOnObject(g498,g212)
    c: PointOnObject(g426,g220)
    c: PointOnObject(g499,g212)
    c: PointOnObject(g427,g220)
    c: PointOnObject(g500,g214)
    c: PointOnObject(g428,g220)
    c: PointOnObject(g501,g215)
    c: PointOnObject(g429,g219)
    c: PointOnObject(g502,g216)
    c: PointOnObject(g430,g219)
    c: PointOnObject(g503,g216)
    c: PointOnObject(g431,g219)
    c: PointOnObject(g504,g217)
    c: PointOnObject(g432,g219)
    c: PointOnObject(g505,g288)
    c: PointOnObject(g433,g219)
    c: PointOnObject(g506,g289)
    c: PointOnObject(g434,g218)
    c: PointOnObject(g507,g290)
    c: PointOnObject(g435,g301)
    c: PointOnObject(g508,g290)
    c: PointOnObject(g436,g299)
    c: PointOnObject(g509,g290)
    c: PointOnObject(g437,g299)
    c: PointOnObject(g510,g292)
    c: PointOnObject(g438,g299)
    c: PointOnObject(g511,g293)
    c: PointOnObject(g439,g298)
    c: PointOnObject(g512,g294)
    c: PointOnObject(g440,g298)
    c: PointOnObject(g513,g333)
    c: PointOnObject(g441,g298)
    c: PointOnObject(g514,g334)
    c: PointOnObject(g442,g298)
    c: PointOnObject(g515,g335)
    c: PointOnObject(g443,g298)
    c: PointOnObject(g516,g296)
    c: PointOnObject(g444,g297)
    c: PointOnObject(g517,g297)
    c: PointOnObject(g517,g344)
    c: PointOnObject(g518,g336)
    c: PointOnObject(g516,g295)
    c: PointOnObject(g519,g335)
    c: PointOnObject(g445,g344)
    c: PointOnObject(g520,g337)
    c: PointOnObject(g446,g344)
    c: PointOnObject(g521,g338)
    c: PointOnObject(g447,g343)
    c: PointOnObject(g522,g339)
    c: PointOnObject(g448,g343)
    c: PointOnObject(g523,g379)
    c: PointOnObject(g449,g343)
    c: PointOnObject(g524,g380)
    c: PointOnObject(g450,g343)
    c: PointOnObject(g525,g381)
    c: PointOnObject(g451,g343)
    c: PointOnObject(g526,g341)
    c: PointOnObject(g453,g342)
    c: PointOnObject(g527,g342)
    c: PointOnObject(g464,g389)
    c: PointOnObject(g528,g389)
    c: PointOnObject(g461,g390)
    c: PointOnObject(g529,g388)
    c: PointOnObject(g460,g390)
    c: PointOnObject(g530,g386)
    c: PointOnObject(g459,g390)
    c: PointOnObject(g531,g386)
    c: PointOnObject(g458,g390)
    c: PointOnObject(g532,g385)
    c: PointOnObject(g457,g390)
    c: PointOnObject(g533,g385)
    c: PointOnObject(g456,g391)
    c: PointOnObject(g534,g384)
    c: PointOnObject(g454,g391)
    c: PointOnObject(g535,g383)
    c: PointOnObject(g527,g391)
    c: PointOnObject(g536,g382)
    c: PointOnObject(g526,g393)
    c: PointOnObject(g537,g381)
    c: PointOnObject(g1,g147)
    c: PointOnObject(g538,g133)
    c: PointOnObject(g2,g147)
    c: PointOnObject(g539,g134)
    c: PointOnObject(g3,g146)
    c: PointOnObject(g540,g135)
    c: PointOnObject(g4,g146)
    c: PointOnObject(g541,g135)
    c: PointOnObject(g5,g144)
    c: PointOnObject(g542,g136)
    c: PointOnObject(g6,g144)
    c: PointOnObject(g543,g137)
    c: PointOnObject(g7,g144)
    c: PointOnObject(g544,g138)
    c: PointOnObject(g8,g143)
    c: PointOnObject(g545,g139)
    c: PointOnObject(g9,g143)
    c: PointOnObject(g546,g139)
    c: PointOnObject(g474,g143)
    c: PointOnObject(g547,g150)
    c: PointOnObject(g475,g143)
    c: PointOnObject(g548,g151)
    c: PointOnObject(g476,g143)
    c: PointOnObject(g549,g152)
    c: PointOnObject(g477,g142)
    c: PointOnObject(g550,g142)
    c: PointOnObject(g550,g163)
    c: PointOnObject(g551,g152)
    c: PointOnObject(g478,g161)
    c: PointOnObject(g552,g153)
    c: PointOnObject(g479,g161)
    c: PointOnObject(g553,g154)
    c: PointOnObject(g480,g161)
    c: PointOnObject(g554,g155)
    c: PointOnObject(g481,g160)
    c: PointOnObject(g555,g156)
    c: PointOnObject(g482,g160)
    c: PointOnObject(g556,g156)
    c: PointOnObject(g483,g160)
    c: PointOnObject(g557,g157)
    c: PointOnObject(g484,g160)
    c: PointOnObject(g558,g157)
    c: PointOnObject(g485,g160)
    c: PointOnObject(g559,g225)
    c: PointOnObject(g486,g159)
    c: PointOnObject(g560,g226)
    c: PointOnObject(g487,g237)
    c: PointOnObject(g561,g227)
    c: PointOnObject(g488,g237)
    c: PointOnObject(g562,g227)
    c: PointOnObject(g489,g235)
    c: PointOnObject(g563,g227)
    c: PointOnObject(g491,g235)
    c: PointOnObject(g564,g228)
    c: PointOnObject(g492,g235)
    c: PointOnObject(g565,g230)
    c: PointOnObject(g493,g234)
    c: PointOnObject(g566,g231)
    c: PointOnObject(g494,g234)
    c: PointOnObject(g567,g231)
    c: PointOnObject(g495,g234)
    c: PointOnObject(g568,g232)
    c: PointOnObject(g496,g234)
    c: PointOnObject(g569,g273)
    c: PointOnObject(g497,g234)
    c: PointOnObject(g570,g274)
    c: PointOnObject(g498,g233)
    c: PointOnObject(g571,g275)
    c: PointOnObject(g499,g286)
    c: PointOnObject(g572,g275)
    c: PointOnObject(g500,g284)
    c: PointOnObject(g573,g275)
    c: PointOnObject(g501,g284)
    c: PointOnObject(g574,g276)
    c: PointOnObject(g502,g284)
    c: PointOnObject(g575,g278)
    c: PointOnObject(g503,g283)
    c: PointOnObject(g576,g279)
    c: PointOnObject(g504,g283)
    c: PointOnObject(g577,g348)
    c: PointOnObject(g505,g283)
    c: PointOnObject(g578,g349)
    c: PointOnObject(g508,g282)
    c: PointOnObject(g579,g282)
    c: PointOnObject(g507,g283)
    c: PointOnObject(g580,g281)
    c: PointOnObject(g506,g283)
    c: PointOnObject(g581,g350)
    c: PointOnObject(g580,g280)
    c: PointOnObject(g582,g350)
    c: PointOnObject(g579,g359)
    c: PointOnObject(g583,g351)
    c: PointOnObject(g509,g359)
    c: PointOnObject(g584,g352)
    c: PointOnObject(g510,g359)
    c: PointOnObject(g585,g353)
    c: PointOnObject(g511,g358)
    c: PointOnObject(g586,g354)
    c: PointOnObject(g512,g358)
    c: PointOnObject(g587,g363)
    c: PointOnObject(g513,g358)
    c: PointOnObject(g588,g364)
    c: PointOnObject(g514,g358)
    c: PointOnObject(g589,g365)
    c: PointOnObject(g515,g358)
    c: PointOnObject(g590,g356)
    c: PointOnObject(g519,g357)
    c: PointOnObject(g591,g357)
    c: PointOnObject(g590,g377)
    c: PointOnObject(g592,g365)
    c: PointOnObject(g591,g375)
    c: PointOnObject(g593,g366)
    c: PointOnObject(g518,g375)
    c: PointOnObject(g594,g367)
    c: PointOnObject(g520,g375)
    c: PointOnObject(g595,g368)
    c: PointOnObject(g521,g374)
    c: PointOnObject(g596,g369)
    c: PointOnObject(g522,g374)
    c: PointOnObject(g597,g369)
    c: PointOnObject(g523,g374)
    c: PointOnObject(g598,g370)
    c: PointOnObject(g524,g374)
    c: PointOnObject(g599,g370)
    c: PointOnObject(g525,g374)
    c: PointOnObject(g600,g372)
    c: PointOnObject(g537,g373)
    c: PointOnObject(g601,g373)
    c: PointOnObject(g575,g268)
    c: PointOnObject(g602,g266)
    c: PointOnObject(g604,g265)
    c: PointOnObject(g603,g265)
    c: PointOnObject(g628,g268)
    c: PointOnObject(g604,g266)
    c: PointOnObject(g573,g268)
    c: PointOnObject(g605,g264)
    c: PointOnObject(g572,g268)
    c: PointOnObject(g606,g264)
    c: PointOnObject(g571,g268)
    c: PointOnObject(g607,g263)
    c: PointOnObject(g570,g268)
    c: PointOnObject(g608,g263)
    c: PointOnObject(g569,g269)
    c: PointOnObject(g609,g262)
    c: PointOnObject(g568,g269)
    c: PointOnObject(g610,g260)
    c: PointOnObject(g567,g269)
    c: PointOnObject(g611,g259)
    c: PointOnObject(g625,g271)
    c: PointOnObject(g612,g259)
    c: PointOnObject(g565,g250)
    c: PointOnObject(g613,g259)
    c: PointOnObject(g629,g250)
    c: PointOnObject(g614,g258)
    c: PointOnObject(g563,g250)
    c: PointOnObject(g615,g247)
    c: PointOnObject(g562,g250)
    c: PointOnObject(g616,g246)
    c: PointOnObject(g561,g250)
    c: PointOnObject(g617,g246)
    c: PointOnObject(g560,g251)
    c: PointOnObject(g618,g245)
    c: PointOnObject(g559,g251)
    c: PointOnObject(g619,g243)
    c: PointOnObject(g558,g251)
    c: PointOnObject(g620,g242)
    c: PointOnObject(g557,g253)
    c: PointOnObject(g621,g242)
    c: PointOnObject(g556,g253)
    c: PointOnObject(g622,g242)
    c: PointOnObject(g555,g254)
    c: PointOnObject(g623,g241)
    c: PointOnObject(g554,g255)
    c: PointOnObject(g624,g255)
    c: PointOnObject(g566,g250)
    c: PointOnObject(g625,g248)
    c: PointOnObject(g624,g240)
    c: PointOnObject(g626,g240)
    c: PointOnObject(g615,g257)
    c: PointOnObject(g627,g257)
    c: PointOnObject(g574,g277)
    c: PointOnObject(g628,g277)
    c: PointOnObject(g564,g229)
    c: PointOnObject(g629,g229)
    c: PointOnObject(g31,g108)
    c: PointOnObject(g630,g108)
